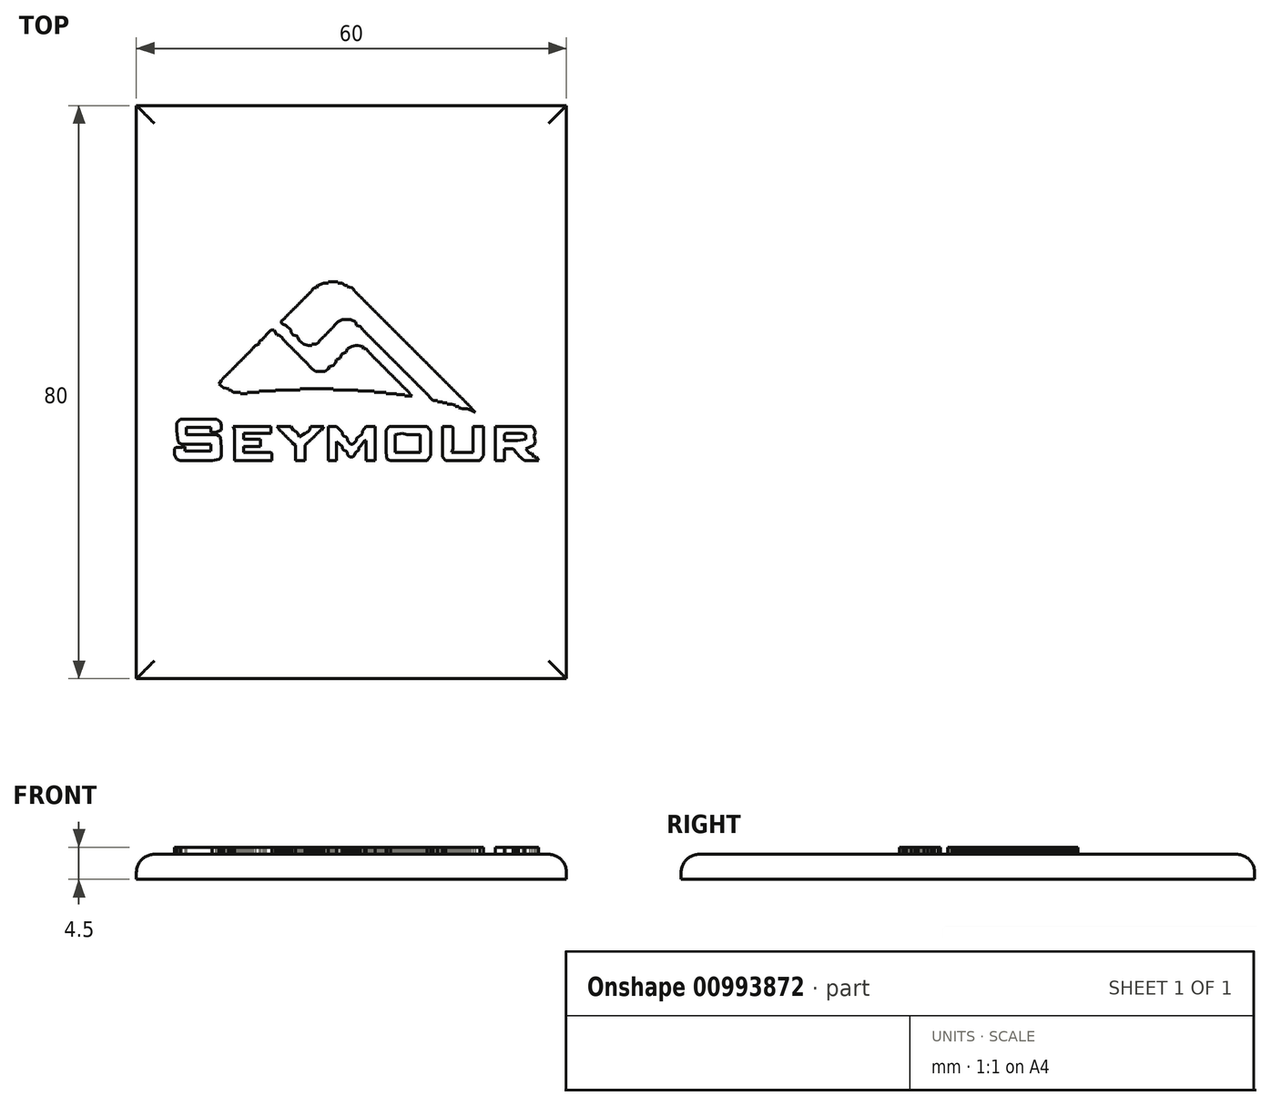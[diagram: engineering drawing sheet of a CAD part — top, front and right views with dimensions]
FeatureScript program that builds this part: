
annotation { "Feature Type Name" : "Feature", "Feature Type Description" : "" }
export const myFeature = defineFeature(function(context is Context, id is Id, definition is map)
    precondition{}
    {
        {
            var Q0;
            Q0=qCreatedBy(makeId("Top.planeOp"),FACE);
            var sketch = newSketch(context, id + "F0", { "sketchPlane" : qUnion([Q0])});
            skLineSegment(sketch, "E0.bottom", {"start": v(-30, 40) * mm, "end": v(30, 40) * mm});
            skLineSegment(sketch, "E0.top", {"start": v(-30, -40) * mm, "end": v(30, -40) * mm});
            skLineSegment(sketch, "E0.left", {"start": v(-30, 40) * mm, "end": v(-30, -40) * mm});
            skLineSegment(sketch, "E0.right", {"start": v(30, 40) * mm, "end": v(30, -40) * mm});
            skLineSegment(sketch, "E1", {"start": v(0, 0) * mm, "end": v(0, 40) * mm});
            skSolve(sketch);
        }
        {
            var Q0;
            Q0 = qSketchRegion(id + "F0", true);
            extrude(context, id + "F1", {"entities" : qUnion([Q0]), "depth" : 3.5 * mm, "offsetDistance" : 25 * mm});
        }
        {
            var Q0;
            Q0=qCreatedBy(makeId("Top.planeOp"),FACE);
            cPlane(context, id + "F2", {"entities" : qUnion([Q0]), "cplaneType" : CPlaneType.OFFSET, "offset" : 3.5 * mm, "width" : 150 * mm, "height" : 150 * mm});
        }
        {
            var Q0;
            Q0=makeQuery(id+"F1.opExtrude","CAP_EDGE",EDGE,{"disambiguationData":[OSD([sQuery(id+"F0.wireOp",EDGE,"E0.left")])],"isStart":false});
            var Q1;
            Q1=makeQuery(id+"F1.opExtrude","CAP_EDGE",EDGE,{"disambiguationData":[OSD([sQuery(id+"F0.wireOp",EDGE,"E0.bottom")])],"isStart":false});
            var Q2;
            Q2=makeQuery(id+"F1.opExtrude","CAP_FACE",FACE,{"disambiguationData":[OSD([sQuery(id+"F0.wireOp",EDGE,"E0.bottom"),sQuery(id+"F0.wireOp",EDGE,"E0.top"),sQuery(id+"F0.wireOp",EDGE,"E0.left"),sQuery(id+"F0.wireOp",EDGE,"E0.right")])],"isStart":false});
            var Q3;
            Q3=makeQuery(id+"F1.opExtrude","CAP_EDGE",EDGE,{"disambiguationData":[OSD([sQuery(id+"F0.wireOp",EDGE,"E0.top")])],"isStart":false});
            fillet(context, id + "F3", {"entities" : qUnion([Q0, Q1, Q2, Q3]), "radius" : 2.5 * mm, "tangentPropagation" : true, "allowEdgeOverflow" : false});
        }
        {
            var Q0;
            Q0=qCreatedBy(id+"F2.planeOp",FACE);
            var sketch = newSketch(context, id + "F4", { "sketchPlane" : qUnion([Q0])});
            skLineSegment(sketch, "E2", {"start": v(-3.22, 15.38) * mm, "end": v(-3.22, 15.21) * mm});
            skLineSegment(sketch, "E3", {"start": v(-3.22, 15.21) * mm, "end": v(-3.87, 15.21) * mm});
            skLineSegment(sketch, "E4", {"start": v(-3.87, 15.21) * mm, "end": v(-4.7, 14.89) * mm});
            skLineSegment(sketch, "E5", {"start": v(-4.7, 14.89) * mm, "end": v(-4.85, 14.56) * mm});
            skLineSegment(sketch, "E6", {"start": v(-4.85, 14.56) * mm, "end": v(-5.18, 14.56) * mm});
            skLineSegment(sketch, "E7", {"start": v(-5.18, 14.56) * mm, "end": v(-5.51, 14.23) * mm});
            skLineSegment(sketch, "E8", {"start": v(-5.51, 14.23) * mm, "end": v(-5.51, 14.07) * mm});
            skLineSegment(sketch, "E9", {"start": v(-5.51, 14.07) * mm, "end": v(-5.67, 14.07) * mm});
            skLineSegment(sketch, "E10", {"start": v(-5.67, 14.07) * mm, "end": v(-5.67, 13.9) * mm});
            skLineSegment(sketch, "E11", {"start": v(-5.67, 13.9) * mm, "end": v(-5.84, 13.9) * mm});
            skLineSegment(sketch, "E12", {"start": v(-5.84, 13.9) * mm, "end": v(-5.84, 13.74) * mm});
            skLineSegment(sketch, "E13", {"start": v(-5.84, 13.74) * mm, "end": v(-6, 13.74) * mm});
            skLineSegment(sketch, "E14", {"start": v(-6, 13.74) * mm, "end": v(-6, 13.57) * mm});
            skLineSegment(sketch, "E15", {"start": v(-6, 13.57) * mm, "end": v(-6.17, 13.57) * mm});
            skLineSegment(sketch, "E16", {"start": v(-6.17, 13.57) * mm, "end": v(-6.17, 13.41) * mm});
            skLineSegment(sketch, "E17", {"start": v(-6.17, 13.41) * mm, "end": v(-6.33, 13.41) * mm});
            skLineSegment(sketch, "E18", {"start": v(-6.33, 13.41) * mm, "end": v(-6.33, 13.25) * mm});
            skLineSegment(sketch, "E19", {"start": v(-6.33, 13.25) * mm, "end": v(-6.5, 13.25) * mm});
            skLineSegment(sketch, "E20", {"start": v(-6.5, 13.25) * mm, "end": v(-6.5, 13.08) * mm});
            skLineSegment(sketch, "E21", {"start": v(-6.5, 13.08) * mm, "end": v(-6.66, 13.08) * mm});
            skLineSegment(sketch, "E22", {"start": v(-6.66, 13.08) * mm, "end": v(-6.66, 12.92) * mm});
            skLineSegment(sketch, "E23", {"start": v(-6.66, 12.92) * mm, "end": v(-6.82, 12.92) * mm});
            skLineSegment(sketch, "E24", {"start": v(-6.82, 12.92) * mm, "end": v(-6.82, 12.76) * mm});
            skLineSegment(sketch, "E25", {"start": v(-6.82, 12.76) * mm, "end": v(-6.99, 12.76) * mm});
            skLineSegment(sketch, "E26", {"start": v(-6.99, 12.76) * mm, "end": v(-6.99, 12.6) * mm});
            skLineSegment(sketch, "E27", {"start": v(-6.99, 12.6) * mm, "end": v(-7.15, 12.6) * mm});
            skLineSegment(sketch, "E28", {"start": v(-7.15, 12.6) * mm, "end": v(-7.15, 12.43) * mm});
            skLineSegment(sketch, "E29", {"start": v(-7.15, 12.43) * mm, "end": v(-7.31, 12.43) * mm});
            skLineSegment(sketch, "E30", {"start": v(-7.31, 12.43) * mm, "end": v(-7.31, 12.26) * mm});
            skLineSegment(sketch, "E31", {"start": v(-7.31, 12.26) * mm, "end": v(-7.48, 12.26) * mm});
            skLineSegment(sketch, "E32", {"start": v(-7.48, 12.26) * mm, "end": v(-7.48, 12.1) * mm});
            skLineSegment(sketch, "E33", {"start": v(-7.48, 12.1) * mm, "end": v(-7.64, 12.1) * mm});
            skLineSegment(sketch, "E34", {"start": v(-7.64, 12.1) * mm, "end": v(-7.64, 11.94) * mm});
            skLineSegment(sketch, "E35", {"start": v(-7.64, 11.94) * mm, "end": v(-7.8, 11.94) * mm});
            skLineSegment(sketch, "E36", {"start": v(-7.8, 11.94) * mm, "end": v(-7.8, 11.77) * mm});
            skLineSegment(sketch, "E37", {"start": v(-7.8, 11.77) * mm, "end": v(-7.97, 11.77) * mm});
            skLineSegment(sketch, "E38", {"start": v(-7.97, 11.77) * mm, "end": v(-7.97, 11.6) * mm});
            skLineSegment(sketch, "E39", {"start": v(-7.97, 11.6) * mm, "end": v(-8.13, 11.6) * mm});
            skLineSegment(sketch, "E40", {"start": v(-8.13, 11.6) * mm, "end": v(-8.13, 11.44) * mm});
            skLineSegment(sketch, "E41", {"start": v(-8.13, 11.44) * mm, "end": v(-8.3, 11.44) * mm});
            skLineSegment(sketch, "E42", {"start": v(-8.3, 11.44) * mm, "end": v(-8.3, 11.28) * mm});
            skLineSegment(sketch, "E43", {"start": v(-8.3, 11.28) * mm, "end": v(-8.46, 11.28) * mm});
            skLineSegment(sketch, "E44", {"start": v(-8.46, 11.28) * mm, "end": v(-8.46, 11.12) * mm});
            skLineSegment(sketch, "E45", {"start": v(-8.46, 11.12) * mm, "end": v(-8.63, 11.12) * mm});
            skLineSegment(sketch, "E46", {"start": v(-8.63, 11.12) * mm, "end": v(-8.63, 10.95) * mm});
            skLineSegment(sketch, "E47", {"start": v(-8.63, 10.95) * mm, "end": v(-8.79, 10.95) * mm});
            skLineSegment(sketch, "E48", {"start": v(-8.79, 10.95) * mm, "end": v(-8.79, 10.79) * mm});
            skLineSegment(sketch, "E49", {"start": v(-8.79, 10.79) * mm, "end": v(-8.95, 10.79) * mm});
            skLineSegment(sketch, "E50", {"start": v(-8.95, 10.79) * mm, "end": v(-8.95, 10.62) * mm});
            skLineSegment(sketch, "E51", {"start": v(-8.95, 10.62) * mm, "end": v(-9.12, 10.62) * mm});
            skLineSegment(sketch, "E52", {"start": v(-9.12, 10.62) * mm, "end": v(-9.12, 10.46) * mm});
            skLineSegment(sketch, "E53", {"start": v(-9.12, 10.46) * mm, "end": v(-9.28, 10.46) * mm});
            skLineSegment(sketch, "E54", {"start": v(-9.28, 10.46) * mm, "end": v(-9.28, 10.3) * mm});
            skLineSegment(sketch, "E55", {"start": v(-9.28, 10.3) * mm, "end": v(-9.77, 9.97) * mm});
            skLineSegment(sketch, "E56", {"start": v(-9.77, 9.97) * mm, "end": v(-9.77, 9.64) * mm});
            skLineSegment(sketch, "E57", {"start": v(-9.77, 9.64) * mm, "end": v(-9.6, 9.48) * mm});
            skLineSegment(sketch, "E58", {"start": v(-9.6, 9.48) * mm, "end": v(-9.12, 9.31) * mm});
            skLineSegment(sketch, "E59", {"start": v(-9.12, 9.31) * mm, "end": v(-8.63, 8.82) * mm});
            skLineSegment(sketch, "E60", {"start": v(-8.63, 8.82) * mm, "end": v(-8.46, 8.66) * mm});
            skLineSegment(sketch, "E61", {"start": v(-8.46, 8.66) * mm, "end": v(-8.46, 8.33) * mm});
            skLineSegment(sketch, "E62", {"start": v(-8.46, 8.33) * mm, "end": v(-8.13, 8) * mm});
            skLineSegment(sketch, "E63", {"start": v(-8.13, 8) * mm, "end": v(-7.64, 7.84) * mm});
            skLineSegment(sketch, "E64", {"start": v(-7.64, 7.84) * mm, "end": v(-7.48, 7.67) * mm});
            skLineSegment(sketch, "E65", {"start": v(-7.48, 7.67) * mm, "end": v(-7.31, 7.18) * mm});
            skLineSegment(sketch, "E66", {"start": v(-7.31, 7.18) * mm, "end": v(-6.66, 6.69) * mm});
            skLineSegment(sketch, "E67", {"start": v(-6.66, 6.69) * mm, "end": v(-6, 6.53) * mm});
            skLineSegment(sketch, "E68", {"start": v(-6, 6.53) * mm, "end": v(-5.51, 6.53) * mm});
            skLineSegment(sketch, "E69", {"start": v(-5.51, 6.53) * mm, "end": v(-5.51, 6.69) * mm});
            skLineSegment(sketch, "E70", {"start": v(-5.51, 6.69) * mm, "end": v(-4.85, 6.69) * mm});
            skLineSegment(sketch, "E71", {"start": v(-4.85, 6.69) * mm, "end": v(-4.53, 7.02) * mm});
            skLineSegment(sketch, "E72", {"start": v(-4.53, 7.02) * mm, "end": v(-4.53, 7.18) * mm});
            skLineSegment(sketch, "E73", {"start": v(-4.53, 7.18) * mm, "end": v(-4.36, 7.18) * mm});
            skLineSegment(sketch, "E74", {"start": v(-4.36, 7.18) * mm, "end": v(-4.36, 7.35) * mm});
            skLineSegment(sketch, "E75", {"start": v(-4.36, 7.35) * mm, "end": v(-4.2, 7.35) * mm});
            skLineSegment(sketch, "E76", {"start": v(-4.2, 7.35) * mm, "end": v(-4.2, 7.5) * mm});
            skLineSegment(sketch, "E77", {"start": v(-4.2, 7.5) * mm, "end": v(-4.04, 7.5) * mm});
            skLineSegment(sketch, "E78", {"start": v(-4.04, 7.5) * mm, "end": v(-4.04, 7.67) * mm});
            skLineSegment(sketch, "E79", {"start": v(-4.04, 7.67) * mm, "end": v(-3.87, 7.67) * mm});
            skLineSegment(sketch, "E80", {"start": v(-3.87, 7.67) * mm, "end": v(-3.87, 7.84) * mm});
            skLineSegment(sketch, "E81", {"start": v(-3.87, 7.84) * mm, "end": v(-3.7, 7.84) * mm});
            skLineSegment(sketch, "E82", {"start": v(-3.7, 7.84) * mm, "end": v(-3.7, 8) * mm});
            skLineSegment(sketch, "E83", {"start": v(-3.7, 8) * mm, "end": v(-3.54, 8) * mm});
            skLineSegment(sketch, "E84", {"start": v(-3.54, 8) * mm, "end": v(-3.54, 8.16) * mm});
            skLineSegment(sketch, "E85", {"start": v(-3.54, 8.16) * mm, "end": v(-3.38, 8.16) * mm});
            skLineSegment(sketch, "E86", {"start": v(-3.38, 8.16) * mm, "end": v(-3.38, 8.33) * mm});
            skLineSegment(sketch, "E87", {"start": v(-3.38, 8.33) * mm, "end": v(-3.22, 8.33) * mm});
            skLineSegment(sketch, "E88", {"start": v(-3.22, 8.33) * mm, "end": v(-3.22, 8.5) * mm});
            skLineSegment(sketch, "E89", {"start": v(-3.22, 8.5) * mm, "end": v(-3.05, 8.5) * mm});
            skLineSegment(sketch, "E90", {"start": v(-3.05, 8.5) * mm, "end": v(-3.05, 8.66) * mm});
            skLineSegment(sketch, "E91", {"start": v(-3.05, 8.66) * mm, "end": v(-2.89, 8.66) * mm});
            skLineSegment(sketch, "E92", {"start": v(-2.89, 8.66) * mm, "end": v(-2.89, 8.82) * mm});
            skLineSegment(sketch, "E93", {"start": v(-2.89, 8.82) * mm, "end": v(-2.72, 8.82) * mm});
            skLineSegment(sketch, "E94", {"start": v(-2.72, 8.82) * mm, "end": v(-2.72, 8.98) * mm});
            skLineSegment(sketch, "E95", {"start": v(-2.72, 8.98) * mm, "end": v(-2.56, 8.98) * mm});
            skLineSegment(sketch, "E96", {"start": v(-2.56, 8.98) * mm, "end": v(-2.56, 9.15) * mm});
            skLineSegment(sketch, "E97", {"start": v(-2.56, 9.15) * mm, "end": v(-2.4, 9.15) * mm});
            skLineSegment(sketch, "E98", {"start": v(-2.4, 9.15) * mm, "end": v(-2.4, 9.31) * mm});
            skLineSegment(sketch, "E99", {"start": v(-2.4, 9.31) * mm, "end": v(-1.9, 9.8) * mm});
            skLineSegment(sketch, "E100", {"start": v(-1.9, 9.8) * mm, "end": v(-1.25, 10.13) * mm});
            skLineSegment(sketch, "E101", {"start": v(-1.25, 10.13) * mm, "end": v(-0.1, 10.13) * mm});
            skLineSegment(sketch, "E102", {"start": v(-0.1, 10.13) * mm, "end": v(0.55, 9.8) * mm});
            skLineSegment(sketch, "E103", {"start": v(0.55, 9.8) * mm, "end": v(0.72, 9.31) * mm});
            skLineSegment(sketch, "E104", {"start": v(0.72, 9.31) * mm, "end": v(1.21, 9.15) * mm});
            skLineSegment(sketch, "E105", {"start": v(1.21, 9.15) * mm, "end": v(1.54, 8.82) * mm});
            skLineSegment(sketch, "E106", {"start": v(1.54, 8.82) * mm, "end": v(1.54, 8.66) * mm});
            skLineSegment(sketch, "E107", {"start": v(1.54, 8.66) * mm, "end": v(1.7, 8.66) * mm});
            skLineSegment(sketch, "E108", {"start": v(1.7, 8.66) * mm, "end": v(1.7, 8.5) * mm});
            skLineSegment(sketch, "E109", {"start": v(1.7, 8.5) * mm, "end": v(1.87, 8.5) * mm});
            skLineSegment(sketch, "E110", {"start": v(1.87, 8.5) * mm, "end": v(1.87, 8.33) * mm});
            skLineSegment(sketch, "E111", {"start": v(1.87, 8.33) * mm, "end": v(2.03, 8.33) * mm});
            skLineSegment(sketch, "E112", {"start": v(2.03, 8.33) * mm, "end": v(2.03, 8.16) * mm});
            skLineSegment(sketch, "E113", {"start": v(2.03, 8.16) * mm, "end": v(2.2, 8.16) * mm});
            skLineSegment(sketch, "E114", {"start": v(2.2, 8.16) * mm, "end": v(2.2, 8) * mm});
            skLineSegment(sketch, "E115", {"start": v(2.2, 8) * mm, "end": v(2.36, 8) * mm});
            skLineSegment(sketch, "E116", {"start": v(2.36, 8) * mm, "end": v(2.36, 7.84) * mm});
            skLineSegment(sketch, "E117", {"start": v(2.36, 7.84) * mm, "end": v(2.52, 7.84) * mm});
            skLineSegment(sketch, "E118", {"start": v(2.52, 7.84) * mm, "end": v(2.52, 7.67) * mm});
            skLineSegment(sketch, "E119", {"start": v(2.52, 7.67) * mm, "end": v(2.69, 7.67) * mm});
            skLineSegment(sketch, "E120", {"start": v(2.69, 7.67) * mm, "end": v(2.69, 7.5) * mm});
            skLineSegment(sketch, "E121", {"start": v(2.69, 7.5) * mm, "end": v(2.85, 7.5) * mm});
            skLineSegment(sketch, "E122", {"start": v(2.85, 7.5) * mm, "end": v(2.85, 7.35) * mm});
            skLineSegment(sketch, "E123", {"start": v(2.85, 7.35) * mm, "end": v(3.01, 7.35) * mm});
            skLineSegment(sketch, "E124", {"start": v(3.01, 7.35) * mm, "end": v(3.01, 7.18) * mm});
            skLineSegment(sketch, "E125", {"start": v(3.01, 7.18) * mm, "end": v(3.18, 7.18) * mm});
            skLineSegment(sketch, "E126", {"start": v(3.18, 7.18) * mm, "end": v(3.18, 7.02) * mm});
            skLineSegment(sketch, "E127", {"start": v(3.18, 7.02) * mm, "end": v(3.34, 7.02) * mm});
            skLineSegment(sketch, "E128", {"start": v(3.34, 7.02) * mm, "end": v(3.34, 6.85) * mm});
            skLineSegment(sketch, "E129", {"start": v(3.34, 6.85) * mm, "end": v(3.5, 6.85) * mm});
            skLineSegment(sketch, "E130", {"start": v(3.5, 6.85) * mm, "end": v(3.5, 6.69) * mm});
            skLineSegment(sketch, "E131", {"start": v(3.5, 6.69) * mm, "end": v(3.67, 6.69) * mm});
            skLineSegment(sketch, "E132", {"start": v(3.67, 6.69) * mm, "end": v(3.67, 6.53) * mm});
            skLineSegment(sketch, "E133", {"start": v(3.67, 6.53) * mm, "end": v(3.83, 6.53) * mm});
            skLineSegment(sketch, "E134", {"start": v(3.83, 6.53) * mm, "end": v(3.83, 6.36) * mm});
            skLineSegment(sketch, "E135", {"start": v(3.83, 6.36) * mm, "end": v(4, 6.36) * mm});
            skLineSegment(sketch, "E136", {"start": v(4, 6.36) * mm, "end": v(4, 6.2) * mm});
            skLineSegment(sketch, "E137", {"start": v(4, 6.2) * mm, "end": v(4.16, 6.2) * mm});
            skLineSegment(sketch, "E138", {"start": v(4.16, 6.2) * mm, "end": v(4.16, 6.03) * mm});
            skLineSegment(sketch, "E139", {"start": v(4.16, 6.03) * mm, "end": v(4.33, 6.03) * mm});
            skLineSegment(sketch, "E140", {"start": v(4.33, 6.03) * mm, "end": v(4.33, 5.87) * mm});
            skLineSegment(sketch, "E141", {"start": v(4.33, 5.87) * mm, "end": v(4.49, 5.87) * mm});
            skLineSegment(sketch, "E142", {"start": v(4.49, 5.87) * mm, "end": v(4.49, 5.7) * mm});
            skLineSegment(sketch, "E143", {"start": v(4.49, 5.7) * mm, "end": v(4.65, 5.7) * mm});
            skLineSegment(sketch, "E144", {"start": v(4.65, 5.7) * mm, "end": v(4.65, 5.54) * mm});
            skLineSegment(sketch, "E145", {"start": v(4.65, 5.54) * mm, "end": v(4.82, 5.54) * mm});
            skLineSegment(sketch, "E146", {"start": v(4.82, 5.54) * mm, "end": v(4.82, 5.38) * mm});
            skLineSegment(sketch, "E147", {"start": v(4.82, 5.38) * mm, "end": v(4.98, 5.38) * mm});
            skLineSegment(sketch, "E148", {"start": v(4.98, 5.38) * mm, "end": v(4.98, 5.21) * mm});
            skLineSegment(sketch, "E149", {"start": v(4.98, 5.21) * mm, "end": v(5.15, 5.21) * mm});
            skLineSegment(sketch, "E150", {"start": v(5.15, 5.21) * mm, "end": v(5.15, 5.05) * mm});
            skLineSegment(sketch, "E151", {"start": v(5.15, 5.05) * mm, "end": v(5.3, 5.05) * mm});
            skLineSegment(sketch, "E152", {"start": v(5.3, 5.05) * mm, "end": v(5.3, 4.89) * mm});
            skLineSegment(sketch, "E153", {"start": v(5.3, 4.89) * mm, "end": v(5.47, 4.89) * mm});
            skLineSegment(sketch, "E154", {"start": v(5.47, 4.89) * mm, "end": v(5.47, 4.72) * mm});
            skLineSegment(sketch, "E155", {"start": v(5.47, 4.72) * mm, "end": v(5.64, 4.72) * mm});
            skLineSegment(sketch, "E156", {"start": v(5.64, 4.72) * mm, "end": v(5.64, 4.56) * mm});
            skLineSegment(sketch, "E157", {"start": v(5.64, 4.56) * mm, "end": v(5.8, 4.56) * mm});
            skLineSegment(sketch, "E158", {"start": v(5.8, 4.56) * mm, "end": v(5.8, 4.4) * mm});
            skLineSegment(sketch, "E159", {"start": v(5.8, 4.4) * mm, "end": v(5.96, 4.4) * mm});
            skLineSegment(sketch, "E160", {"start": v(5.96, 4.4) * mm, "end": v(5.96, 4.23) * mm});
            skLineSegment(sketch, "E161", {"start": v(5.96, 4.23) * mm, "end": v(6.13, 4.23) * mm});
            skLineSegment(sketch, "E162", {"start": v(6.13, 4.23) * mm, "end": v(6.13, 4.07) * mm});
            skLineSegment(sketch, "E163", {"start": v(6.13, 4.07) * mm, "end": v(6.3, 4.07) * mm});
            skLineSegment(sketch, "E164", {"start": v(6.3, 4.07) * mm, "end": v(6.3, 3.9) * mm});
            skLineSegment(sketch, "E165", {"start": v(6.3, 3.9) * mm, "end": v(6.46, 3.9) * mm});
            skLineSegment(sketch, "E166", {"start": v(6.46, 3.9) * mm, "end": v(6.46, 3.74) * mm});
            skLineSegment(sketch, "E167", {"start": v(6.46, 3.74) * mm, "end": v(6.62, 3.74) * mm});
            skLineSegment(sketch, "E168", {"start": v(6.62, 3.74) * mm, "end": v(6.62, 3.57) * mm});
            skLineSegment(sketch, "E169", {"start": v(6.62, 3.57) * mm, "end": v(6.78, 3.57) * mm});
            skLineSegment(sketch, "E170", {"start": v(6.78, 3.57) * mm, "end": v(6.78, 3.41) * mm});
            skLineSegment(sketch, "E171", {"start": v(6.78, 3.41) * mm, "end": v(6.95, 3.41) * mm});
            skLineSegment(sketch, "E172", {"start": v(6.95, 3.41) * mm, "end": v(6.95, 3.25) * mm});
            skLineSegment(sketch, "E173", {"start": v(6.95, 3.25) * mm, "end": v(7.11, 3.25) * mm});
            skLineSegment(sketch, "E174", {"start": v(7.11, 3.25) * mm, "end": v(7.11, 3.08) * mm});
            skLineSegment(sketch, "E175", {"start": v(7.11, 3.08) * mm, "end": v(7.28, 3.08) * mm});
            skLineSegment(sketch, "E176", {"start": v(7.28, 3.08) * mm, "end": v(7.28, 2.92) * mm});
            skLineSegment(sketch, "E177", {"start": v(7.28, 2.92) * mm, "end": v(7.44, 2.92) * mm});
            skLineSegment(sketch, "E178", {"start": v(7.44, 2.92) * mm, "end": v(7.44, 2.76) * mm});
            skLineSegment(sketch, "E179", {"start": v(7.44, 2.76) * mm, "end": v(7.6, 2.76) * mm});
            skLineSegment(sketch, "E180", {"start": v(7.6, 2.76) * mm, "end": v(7.6, 2.6) * mm});
            skLineSegment(sketch, "E181", {"start": v(7.6, 2.6) * mm, "end": v(7.77, 2.6) * mm});
            skLineSegment(sketch, "E182", {"start": v(7.77, 2.6) * mm, "end": v(7.77, 2.43) * mm});
            skLineSegment(sketch, "E183", {"start": v(7.77, 2.43) * mm, "end": v(7.93, 2.43) * mm});
            skLineSegment(sketch, "E184", {"start": v(7.93, 2.43) * mm, "end": v(7.93, 2.26) * mm});
            skLineSegment(sketch, "E185", {"start": v(7.93, 2.26) * mm, "end": v(8.1, 2.26) * mm});
            skLineSegment(sketch, "E186", {"start": v(8.1, 2.26) * mm, "end": v(8.1, 2.1) * mm});
            skLineSegment(sketch, "E187", {"start": v(8.1, 2.1) * mm, "end": v(8.26, 2.1) * mm});
            skLineSegment(sketch, "E188", {"start": v(8.26, 2.1) * mm, "end": v(8.26, 1.94) * mm});
            skLineSegment(sketch, "E189", {"start": v(8.26, 1.94) * mm, "end": v(8.42, 1.94) * mm});
            skLineSegment(sketch, "E190", {"start": v(8.42, 1.94) * mm, "end": v(8.42, 1.77) * mm});
            skLineSegment(sketch, "E191", {"start": v(8.42, 1.77) * mm, "end": v(8.59, 1.77) * mm});
            skLineSegment(sketch, "E192", {"start": v(8.59, 1.77) * mm, "end": v(8.59, 1.6) * mm});
            skLineSegment(sketch, "E193", {"start": v(8.59, 1.6) * mm, "end": v(8.75, 1.6) * mm});
            skLineSegment(sketch, "E194", {"start": v(8.75, 1.6) * mm, "end": v(8.75, 1.44) * mm});
            skLineSegment(sketch, "E195", {"start": v(8.75, 1.44) * mm, "end": v(8.92, 1.44) * mm});
            skLineSegment(sketch, "E196", {"start": v(8.92, 1.44) * mm, "end": v(8.92, 1.28) * mm});
            skLineSegment(sketch, "E197", {"start": v(8.92, 1.28) * mm, "end": v(9.08, 1.28) * mm});
            skLineSegment(sketch, "E198", {"start": v(9.08, 1.28) * mm, "end": v(9.08, 1.12) * mm});
            skLineSegment(sketch, "E199", {"start": v(9.08, 1.12) * mm, "end": v(9.24, 1.12) * mm});
            skLineSegment(sketch, "E200", {"start": v(9.24, 1.12) * mm, "end": v(9.24, 0.95) * mm});
            skLineSegment(sketch, "E201", {"start": v(9.24, 0.95) * mm, "end": v(9.4, 0.95) * mm});
            skLineSegment(sketch, "E202", {"start": v(9.4, 0.95) * mm, "end": v(9.4, 0.79) * mm});
            skLineSegment(sketch, "E203", {"start": v(9.4, 0.79) * mm, "end": v(9.57, 0.79) * mm});
            skLineSegment(sketch, "E204", {"start": v(9.57, 0.79) * mm, "end": v(9.57, 0.62) * mm});
            skLineSegment(sketch, "E205", {"start": v(9.57, 0.62) * mm, "end": v(9.74, 0.62) * mm});
            skLineSegment(sketch, "E206", {"start": v(9.74, 0.62) * mm, "end": v(9.74, 0.46) * mm});
            skLineSegment(sketch, "E207", {"start": v(9.74, 0.46) * mm, "end": v(9.9, 0.46) * mm});
            skLineSegment(sketch, "E208", {"start": v(9.9, 0.46) * mm, "end": v(9.9, 0.3) * mm});
            skLineSegment(sketch, "E209", {"start": v(9.9, 0.3) * mm, "end": v(10.06, 0.3) * mm});
            skLineSegment(sketch, "E210", {"start": v(10.06, 0.3) * mm, "end": v(10.06, 0.13) * mm});
            skLineSegment(sketch, "E211", {"start": v(10.06, 0.13) * mm, "end": v(10.23, 0.13) * mm});
            skLineSegment(sketch, "E212", {"start": v(10.23, 0.13) * mm, "end": v(10.23, -0.03) * mm});
            skLineSegment(sketch, "E213", {"start": v(10.23, -0.03) * mm, "end": v(10.4, -0.03) * mm});
            skLineSegment(sketch, "E214", {"start": v(10.4, -0.03) * mm, "end": v(10.4, -0.2) * mm});
            skLineSegment(sketch, "E215", {"start": v(10.4, -0.2) * mm, "end": v(10.55, -0.2) * mm});
            skLineSegment(sketch, "E216", {"start": v(10.55, -0.2) * mm, "end": v(10.55, -0.36) * mm});
            skLineSegment(sketch, "E217", {"start": v(10.55, -0.36) * mm, "end": v(10.72, -0.36) * mm});
            skLineSegment(sketch, "E218", {"start": v(10.72, -0.36) * mm, "end": v(10.72, -0.52) * mm});
            skLineSegment(sketch, "E219", {"start": v(10.72, -0.52) * mm, "end": v(10.88, -0.52) * mm});
            skLineSegment(sketch, "E220", {"start": v(10.88, -0.52) * mm, "end": v(10.88, -0.69) * mm});
            skLineSegment(sketch, "E221", {"start": v(10.88, -0.69) * mm, "end": v(11.37, -1.18) * mm});
            skLineSegment(sketch, "E222", {"start": v(11.37, -1.18) * mm, "end": v(12.03, -1.18) * mm});
            skLineSegment(sketch, "E223", {"start": v(12.03, -1.18) * mm, "end": v(12.03, -1.34) * mm});
            skLineSegment(sketch, "E224", {"start": v(12.03, -1.34) * mm, "end": v(12.69, -1.34) * mm});
            skLineSegment(sketch, "E225", {"start": v(12.69, -1.34) * mm, "end": v(12.69, -1.5) * mm});
            skLineSegment(sketch, "E226", {"start": v(12.69, -1.5) * mm, "end": v(13.34, -1.5) * mm});
            skLineSegment(sketch, "E227", {"start": v(13.34, -1.5) * mm, "end": v(13.34, -1.67) * mm});
            skLineSegment(sketch, "E228", {"start": v(13.34, -1.67) * mm, "end": v(14, -1.67) * mm});
            skLineSegment(sketch, "E229", {"start": v(14, -1.67) * mm, "end": v(14.49, -1.84) * mm});
            skLineSegment(sketch, "E230", {"start": v(14.49, -1.84) * mm, "end": v(14.49, -2) * mm});
            skLineSegment(sketch, "E231", {"start": v(14.49, -2) * mm, "end": v(14.98, -2) * mm});
            skLineSegment(sketch, "E232", {"start": v(14.98, -2) * mm, "end": v(14.98, -2.16) * mm});
            skLineSegment(sketch, "E233", {"start": v(14.98, -2.16) * mm, "end": v(15.47, -2.33) * mm});
            skLineSegment(sketch, "E234", {"start": v(15.47, -2.33) * mm, "end": v(16.13, -2.33) * mm});
            skLineSegment(sketch, "E235", {"start": v(16.13, -2.33) * mm, "end": v(16.62, -2.5) * mm});
            skLineSegment(sketch, "E236", {"start": v(16.62, -2.5) * mm, "end": v(17.28, -2.82) * mm});
            skLineSegment(sketch, "E237", {"start": v(17.28, -2.82) * mm, "end": v(16.95, -2.5) * mm});
            skLineSegment(sketch, "E238", {"start": v(16.95, -2.5) * mm, "end": v(16.78, -2.33) * mm});
            skLineSegment(sketch, "E239", {"start": v(16.78, -2.33) * mm, "end": v(16.62, -2.16) * mm});
            skLineSegment(sketch, "E240", {"start": v(16.62, -2.16) * mm, "end": v(16.62, -2) * mm});
            skLineSegment(sketch, "E241", {"start": v(16.62, -2) * mm, "end": v(16.46, -2) * mm});
            skLineSegment(sketch, "E242", {"start": v(16.46, -2) * mm, "end": v(16.46, -1.84) * mm});
            skLineSegment(sketch, "E243", {"start": v(16.46, -1.84) * mm, "end": v(16.3, -1.84) * mm});
            skLineSegment(sketch, "E244", {"start": v(16.3, -1.84) * mm, "end": v(16.3, -1.67) * mm});
            skLineSegment(sketch, "E245", {"start": v(16.3, -1.67) * mm, "end": v(16.13, -1.67) * mm});
            skLineSegment(sketch, "E246", {"start": v(16.13, -1.67) * mm, "end": v(16.13, -1.5) * mm});
            skLineSegment(sketch, "E247", {"start": v(16.13, -1.5) * mm, "end": v(15.96, -1.5) * mm});
            skLineSegment(sketch, "E248", {"start": v(15.96, -1.5) * mm, "end": v(15.96, -1.34) * mm});
            skLineSegment(sketch, "E249", {"start": v(15.96, -1.34) * mm, "end": v(15.8, -1.34) * mm});
            skLineSegment(sketch, "E250", {"start": v(15.8, -1.34) * mm, "end": v(15.8, -1.18) * mm});
            skLineSegment(sketch, "E251", {"start": v(15.8, -1.18) * mm, "end": v(15.64, -1.18) * mm});
            skLineSegment(sketch, "E252", {"start": v(15.64, -1.18) * mm, "end": v(15.64, -1.02) * mm});
            skLineSegment(sketch, "E253", {"start": v(15.64, -1.02) * mm, "end": v(15.47, -1.02) * mm});
            skLineSegment(sketch, "E254", {"start": v(15.47, -1.02) * mm, "end": v(15.47, -0.85) * mm});
            skLineSegment(sketch, "E255", {"start": v(15.47, -0.85) * mm, "end": v(15.3, -0.85) * mm});
            skLineSegment(sketch, "E256", {"start": v(15.3, -0.85) * mm, "end": v(15.3, -0.69) * mm});
            skLineSegment(sketch, "E257", {"start": v(15.3, -0.69) * mm, "end": v(15.15, -0.69) * mm});
            skLineSegment(sketch, "E258", {"start": v(15.15, -0.69) * mm, "end": v(15.15, -0.52) * mm});
            skLineSegment(sketch, "E259", {"start": v(15.15, -0.52) * mm, "end": v(14.98, -0.52) * mm});
            skLineSegment(sketch, "E260", {"start": v(14.98, -0.52) * mm, "end": v(14.98, -0.36) * mm});
            skLineSegment(sketch, "E261", {"start": v(14.98, -0.36) * mm, "end": v(14.82, -0.36) * mm});
            skLineSegment(sketch, "E262", {"start": v(14.82, -0.36) * mm, "end": v(14.82, -0.2) * mm});
            skLineSegment(sketch, "E263", {"start": v(14.82, -0.2) * mm, "end": v(14.65, -0.2) * mm});
            skLineSegment(sketch, "E264", {"start": v(14.65, -0.2) * mm, "end": v(14.65, -0.03) * mm});
            skLineSegment(sketch, "E265", {"start": v(14.65, -0.03) * mm, "end": v(14.49, -0.03) * mm});
            skLineSegment(sketch, "E266", {"start": v(14.49, -0.03) * mm, "end": v(14.49, 0.13) * mm});
            skLineSegment(sketch, "E267", {"start": v(14.49, 0.13) * mm, "end": v(14.33, 0.13) * mm});
            skLineSegment(sketch, "E268", {"start": v(14.33, 0.13) * mm, "end": v(14.33, 0.3) * mm});
            skLineSegment(sketch, "E269", {"start": v(14.33, 0.3) * mm, "end": v(14.16, 0.3) * mm});
            skLineSegment(sketch, "E270", {"start": v(14.16, 0.3) * mm, "end": v(14.16, 0.46) * mm});
            skLineSegment(sketch, "E271", {"start": v(14.16, 0.46) * mm, "end": v(14, 0.46) * mm});
            skLineSegment(sketch, "E272", {"start": v(14, 0.46) * mm, "end": v(14, 0.62) * mm});
            skLineSegment(sketch, "E273", {"start": v(14, 0.62) * mm, "end": v(13.83, 0.62) * mm});
            skLineSegment(sketch, "E274", {"start": v(13.83, 0.62) * mm, "end": v(13.83, 0.79) * mm});
            skLineSegment(sketch, "E275", {"start": v(13.83, 0.79) * mm, "end": v(13.67, 0.79) * mm});
            skLineSegment(sketch, "E276", {"start": v(13.67, 0.79) * mm, "end": v(13.67, 0.95) * mm});
            skLineSegment(sketch, "E277", {"start": v(13.67, 0.95) * mm, "end": v(13.5, 0.95) * mm});
            skLineSegment(sketch, "E278", {"start": v(13.5, 0.95) * mm, "end": v(13.5, 1.12) * mm});
            skLineSegment(sketch, "E279", {"start": v(13.5, 1.12) * mm, "end": v(13.34, 1.12) * mm});
            skLineSegment(sketch, "E280", {"start": v(13.34, 1.12) * mm, "end": v(13.34, 1.28) * mm});
            skLineSegment(sketch, "E281", {"start": v(13.34, 1.28) * mm, "end": v(13.18, 1.28) * mm});
            skLineSegment(sketch, "E282", {"start": v(13.18, 1.28) * mm, "end": v(13.18, 1.44) * mm});
            skLineSegment(sketch, "E283", {"start": v(13.18, 1.44) * mm, "end": v(13.01, 1.44) * mm});
            skLineSegment(sketch, "E284", {"start": v(13.01, 1.44) * mm, "end": v(13.01, 1.6) * mm});
            skLineSegment(sketch, "E285", {"start": v(13.01, 1.6) * mm, "end": v(12.85, 1.6) * mm});
            skLineSegment(sketch, "E286", {"start": v(12.85, 1.6) * mm, "end": v(12.85, 1.77) * mm});
            skLineSegment(sketch, "E287", {"start": v(12.85, 1.77) * mm, "end": v(12.69, 1.77) * mm});
            skLineSegment(sketch, "E288", {"start": v(12.69, 1.77) * mm, "end": v(12.69, 1.94) * mm});
            skLineSegment(sketch, "E289", {"start": v(12.69, 1.94) * mm, "end": v(12.52, 1.94) * mm});
            skLineSegment(sketch, "E290", {"start": v(12.52, 1.94) * mm, "end": v(12.52, 2.1) * mm});
            skLineSegment(sketch, "E291", {"start": v(12.52, 2.1) * mm, "end": v(12.36, 2.1) * mm});
            skLineSegment(sketch, "E292", {"start": v(12.36, 2.1) * mm, "end": v(12.36, 2.26) * mm});
            skLineSegment(sketch, "E293", {"start": v(12.36, 2.26) * mm, "end": v(12.2, 2.26) * mm});
            skLineSegment(sketch, "E294", {"start": v(12.2, 2.26) * mm, "end": v(12.2, 2.43) * mm});
            skLineSegment(sketch, "E295", {"start": v(12.2, 2.43) * mm, "end": v(12.03, 2.43) * mm});
            skLineSegment(sketch, "E296", {"start": v(12.03, 2.43) * mm, "end": v(12.03, 2.6) * mm});
            skLineSegment(sketch, "E297", {"start": v(12.03, 2.6) * mm, "end": v(11.87, 2.6) * mm});
            skLineSegment(sketch, "E298", {"start": v(11.87, 2.6) * mm, "end": v(11.87, 2.76) * mm});
            skLineSegment(sketch, "E299", {"start": v(11.87, 2.76) * mm, "end": v(11.7, 2.76) * mm});
            skLineSegment(sketch, "E300", {"start": v(11.7, 2.76) * mm, "end": v(11.7, 2.92) * mm});
            skLineSegment(sketch, "E301", {"start": v(11.7, 2.92) * mm, "end": v(11.54, 2.92) * mm});
            skLineSegment(sketch, "E302", {"start": v(11.54, 2.92) * mm, "end": v(11.54, 3.08) * mm});
            skLineSegment(sketch, "E303", {"start": v(11.54, 3.08) * mm, "end": v(11.37, 3.08) * mm});
            skLineSegment(sketch, "E304", {"start": v(11.37, 3.08) * mm, "end": v(11.37, 3.25) * mm});
            skLineSegment(sketch, "E305", {"start": v(11.37, 3.25) * mm, "end": v(11.21, 3.25) * mm});
            skLineSegment(sketch, "E306", {"start": v(11.21, 3.25) * mm, "end": v(11.21, 3.41) * mm});
            skLineSegment(sketch, "E307", {"start": v(11.21, 3.41) * mm, "end": v(11.05, 3.41) * mm});
            skLineSegment(sketch, "E308", {"start": v(11.05, 3.41) * mm, "end": v(11.05, 3.57) * mm});
            skLineSegment(sketch, "E309", {"start": v(11.05, 3.57) * mm, "end": v(10.88, 3.57) * mm});
            skLineSegment(sketch, "E310", {"start": v(10.88, 3.57) * mm, "end": v(10.88, 3.74) * mm});
            skLineSegment(sketch, "E311", {"start": v(10.88, 3.74) * mm, "end": v(10.72, 3.74) * mm});
            skLineSegment(sketch, "E312", {"start": v(10.72, 3.74) * mm, "end": v(10.72, 3.9) * mm});
            skLineSegment(sketch, "E313", {"start": v(10.72, 3.9) * mm, "end": v(10.55, 3.9) * mm});
            skLineSegment(sketch, "E314", {"start": v(10.55, 3.9) * mm, "end": v(10.55, 4.07) * mm});
            skLineSegment(sketch, "E315", {"start": v(10.55, 4.07) * mm, "end": v(10.4, 4.07) * mm});
            skLineSegment(sketch, "E316", {"start": v(10.4, 4.07) * mm, "end": v(10.4, 4.23) * mm});
            skLineSegment(sketch, "E317", {"start": v(10.4, 4.23) * mm, "end": v(10.23, 4.23) * mm});
            skLineSegment(sketch, "E318", {"start": v(10.23, 4.23) * mm, "end": v(10.23, 4.4) * mm});
            skLineSegment(sketch, "E319", {"start": v(10.23, 4.4) * mm, "end": v(10.06, 4.4) * mm});
            skLineSegment(sketch, "E320", {"start": v(10.06, 4.4) * mm, "end": v(10.06, 4.56) * mm});
            skLineSegment(sketch, "E321", {"start": v(10.06, 4.56) * mm, "end": v(9.9, 4.56) * mm});
            skLineSegment(sketch, "E322", {"start": v(9.9, 4.56) * mm, "end": v(9.9, 4.72) * mm});
            skLineSegment(sketch, "E323", {"start": v(9.9, 4.72) * mm, "end": v(9.74, 4.72) * mm});
            skLineSegment(sketch, "E324", {"start": v(9.74, 4.72) * mm, "end": v(9.74, 4.89) * mm});
            skLineSegment(sketch, "E325", {"start": v(9.74, 4.89) * mm, "end": v(9.57, 4.89) * mm});
            skLineSegment(sketch, "E326", {"start": v(9.57, 4.89) * mm, "end": v(9.57, 5.05) * mm});
            skLineSegment(sketch, "E327", {"start": v(9.57, 5.05) * mm, "end": v(9.4, 5.05) * mm});
            skLineSegment(sketch, "E328", {"start": v(9.4, 5.05) * mm, "end": v(9.4, 5.21) * mm});
            skLineSegment(sketch, "E329", {"start": v(9.4, 5.21) * mm, "end": v(9.24, 5.21) * mm});
            skLineSegment(sketch, "E330", {"start": v(9.24, 5.21) * mm, "end": v(9.24, 5.38) * mm});
            skLineSegment(sketch, "E331", {"start": v(9.24, 5.38) * mm, "end": v(9.08, 5.38) * mm});
            skLineSegment(sketch, "E332", {"start": v(9.08, 5.38) * mm, "end": v(9.08, 5.54) * mm});
            skLineSegment(sketch, "E333", {"start": v(9.08, 5.54) * mm, "end": v(8.92, 5.54) * mm});
            skLineSegment(sketch, "E334", {"start": v(8.92, 5.54) * mm, "end": v(8.92, 5.7) * mm});
            skLineSegment(sketch, "E335", {"start": v(8.92, 5.7) * mm, "end": v(8.75, 5.7) * mm});
            skLineSegment(sketch, "E336", {"start": v(8.75, 5.7) * mm, "end": v(8.75, 5.87) * mm});
            skLineSegment(sketch, "E337", {"start": v(8.75, 5.87) * mm, "end": v(8.59, 5.87) * mm});
            skLineSegment(sketch, "E338", {"start": v(8.59, 5.87) * mm, "end": v(8.59, 6.03) * mm});
            skLineSegment(sketch, "E339", {"start": v(8.59, 6.03) * mm, "end": v(8.42, 6.03) * mm});
            skLineSegment(sketch, "E340", {"start": v(8.42, 6.03) * mm, "end": v(8.42, 6.2) * mm});
            skLineSegment(sketch, "E341", {"start": v(8.42, 6.2) * mm, "end": v(8.26, 6.2) * mm});
            skLineSegment(sketch, "E342", {"start": v(8.26, 6.2) * mm, "end": v(8.26, 6.36) * mm});
            skLineSegment(sketch, "E343", {"start": v(8.26, 6.36) * mm, "end": v(8.1, 6.36) * mm});
            skLineSegment(sketch, "E344", {"start": v(8.1, 6.36) * mm, "end": v(8.1, 6.53) * mm});
            skLineSegment(sketch, "E345", {"start": v(8.1, 6.53) * mm, "end": v(7.93, 6.53) * mm});
            skLineSegment(sketch, "E346", {"start": v(7.93, 6.53) * mm, "end": v(7.93, 6.69) * mm});
            skLineSegment(sketch, "E347", {"start": v(7.93, 6.69) * mm, "end": v(7.77, 6.69) * mm});
            skLineSegment(sketch, "E348", {"start": v(7.77, 6.69) * mm, "end": v(7.77, 6.85) * mm});
            skLineSegment(sketch, "E349", {"start": v(7.77, 6.85) * mm, "end": v(7.6, 6.85) * mm});
            skLineSegment(sketch, "E350", {"start": v(7.6, 6.85) * mm, "end": v(7.6, 7.02) * mm});
            skLineSegment(sketch, "E351", {"start": v(7.6, 7.02) * mm, "end": v(7.44, 7.02) * mm});
            skLineSegment(sketch, "E352", {"start": v(7.44, 7.02) * mm, "end": v(7.44, 7.18) * mm});
            skLineSegment(sketch, "E353", {"start": v(7.44, 7.18) * mm, "end": v(7.28, 7.18) * mm});
            skLineSegment(sketch, "E354", {"start": v(7.28, 7.18) * mm, "end": v(7.28, 7.35) * mm});
            skLineSegment(sketch, "E355", {"start": v(7.28, 7.35) * mm, "end": v(7.11, 7.35) * mm});
            skLineSegment(sketch, "E356", {"start": v(7.11, 7.35) * mm, "end": v(7.11, 7.5) * mm});
            skLineSegment(sketch, "E357", {"start": v(7.11, 7.5) * mm, "end": v(6.95, 7.5) * mm});
            skLineSegment(sketch, "E358", {"start": v(6.95, 7.5) * mm, "end": v(6.95, 7.67) * mm});
            skLineSegment(sketch, "E359", {"start": v(6.95, 7.67) * mm, "end": v(6.78, 7.67) * mm});
            skLineSegment(sketch, "E360", {"start": v(6.78, 7.67) * mm, "end": v(6.78, 7.84) * mm});
            skLineSegment(sketch, "E361", {"start": v(6.78, 7.84) * mm, "end": v(6.62, 7.84) * mm});
            skLineSegment(sketch, "E362", {"start": v(6.62, 7.84) * mm, "end": v(6.62, 8) * mm});
            skLineSegment(sketch, "E363", {"start": v(6.62, 8) * mm, "end": v(6.46, 8) * mm});
            skLineSegment(sketch, "E364", {"start": v(6.46, 8) * mm, "end": v(6.46, 8.16) * mm});
            skLineSegment(sketch, "E365", {"start": v(6.46, 8.16) * mm, "end": v(6.3, 8.16) * mm});
            skLineSegment(sketch, "E366", {"start": v(6.3, 8.16) * mm, "end": v(6.3, 8.33) * mm});
            skLineSegment(sketch, "E367", {"start": v(6.3, 8.33) * mm, "end": v(6.13, 8.33) * mm});
            skLineSegment(sketch, "E368", {"start": v(6.13, 8.33) * mm, "end": v(6.13, 8.5) * mm});
            skLineSegment(sketch, "E369", {"start": v(6.13, 8.5) * mm, "end": v(5.96, 8.5) * mm});
            skLineSegment(sketch, "E370", {"start": v(5.96, 8.5) * mm, "end": v(5.96, 8.66) * mm});
            skLineSegment(sketch, "E371", {"start": v(5.96, 8.66) * mm, "end": v(5.8, 8.66) * mm});
            skLineSegment(sketch, "E372", {"start": v(5.8, 8.66) * mm, "end": v(5.8, 8.82) * mm});
            skLineSegment(sketch, "E373", {"start": v(5.8, 8.82) * mm, "end": v(5.64, 8.82) * mm});
            skLineSegment(sketch, "E374", {"start": v(5.64, 8.82) * mm, "end": v(5.64, 8.98) * mm});
            skLineSegment(sketch, "E375", {"start": v(5.64, 8.98) * mm, "end": v(5.47, 8.98) * mm});
            skLineSegment(sketch, "E376", {"start": v(5.47, 8.98) * mm, "end": v(5.47, 9.15) * mm});
            skLineSegment(sketch, "E377", {"start": v(5.47, 9.15) * mm, "end": v(5.3, 9.15) * mm});
            skLineSegment(sketch, "E378", {"start": v(5.3, 9.15) * mm, "end": v(5.3, 9.31) * mm});
            skLineSegment(sketch, "E379", {"start": v(5.3, 9.31) * mm, "end": v(5.15, 9.31) * mm});
            skLineSegment(sketch, "E380", {"start": v(5.15, 9.31) * mm, "end": v(5.15, 9.48) * mm});
            skLineSegment(sketch, "E381", {"start": v(5.15, 9.48) * mm, "end": v(4.98, 9.48) * mm});
            skLineSegment(sketch, "E382", {"start": v(4.98, 9.48) * mm, "end": v(4.98, 9.64) * mm});
            skLineSegment(sketch, "E383", {"start": v(4.98, 9.64) * mm, "end": v(4.82, 9.64) * mm});
            skLineSegment(sketch, "E384", {"start": v(4.82, 9.64) * mm, "end": v(4.82, 9.8) * mm});
            skLineSegment(sketch, "E385", {"start": v(4.82, 9.8) * mm, "end": v(4.65, 9.8) * mm});
            skLineSegment(sketch, "E386", {"start": v(4.65, 9.8) * mm, "end": v(4.65, 9.97) * mm});
            skLineSegment(sketch, "E387", {"start": v(4.65, 9.97) * mm, "end": v(4.49, 9.97) * mm});
            skLineSegment(sketch, "E388", {"start": v(4.49, 9.97) * mm, "end": v(4.49, 10.13) * mm});
            skLineSegment(sketch, "E389", {"start": v(4.49, 10.13) * mm, "end": v(4.33, 10.13) * mm});
            skLineSegment(sketch, "E390", {"start": v(4.33, 10.13) * mm, "end": v(4.33, 10.3) * mm});
            skLineSegment(sketch, "E391", {"start": v(4.33, 10.3) * mm, "end": v(4.16, 10.3) * mm});
            skLineSegment(sketch, "E392", {"start": v(4.16, 10.3) * mm, "end": v(4.16, 10.46) * mm});
            skLineSegment(sketch, "E393", {"start": v(4.16, 10.46) * mm, "end": v(4, 10.46) * mm});
            skLineSegment(sketch, "E394", {"start": v(4, 10.46) * mm, "end": v(4, 10.62) * mm});
            skLineSegment(sketch, "E395", {"start": v(4, 10.62) * mm, "end": v(3.83, 10.62) * mm});
            skLineSegment(sketch, "E396", {"start": v(3.83, 10.62) * mm, "end": v(3.83, 10.79) * mm});
            skLineSegment(sketch, "E397", {"start": v(3.83, 10.79) * mm, "end": v(3.67, 10.79) * mm});
            skLineSegment(sketch, "E398", {"start": v(3.67, 10.79) * mm, "end": v(3.67, 10.95) * mm});
            skLineSegment(sketch, "E399", {"start": v(3.67, 10.95) * mm, "end": v(3.5, 10.95) * mm});
            skLineSegment(sketch, "E400", {"start": v(3.5, 10.95) * mm, "end": v(3.5, 11.12) * mm});
            skLineSegment(sketch, "E401", {"start": v(3.5, 11.12) * mm, "end": v(3.34, 11.12) * mm});
            skLineSegment(sketch, "E402", {"start": v(3.34, 11.12) * mm, "end": v(3.34, 11.28) * mm});
            skLineSegment(sketch, "E403", {"start": v(3.34, 11.28) * mm, "end": v(3.18, 11.28) * mm});
            skLineSegment(sketch, "E404", {"start": v(3.18, 11.28) * mm, "end": v(3.18, 11.44) * mm});
            skLineSegment(sketch, "E405", {"start": v(3.18, 11.44) * mm, "end": v(3.01, 11.44) * mm});
            skLineSegment(sketch, "E406", {"start": v(3.01, 11.44) * mm, "end": v(3.01, 11.6) * mm});
            skLineSegment(sketch, "E407", {"start": v(3.01, 11.6) * mm, "end": v(2.85, 11.6) * mm});
            skLineSegment(sketch, "E408", {"start": v(2.85, 11.6) * mm, "end": v(2.85, 11.77) * mm});
            skLineSegment(sketch, "E409", {"start": v(2.85, 11.77) * mm, "end": v(2.69, 11.77) * mm});
            skLineSegment(sketch, "E410", {"start": v(2.69, 11.77) * mm, "end": v(2.69, 11.94) * mm});
            skLineSegment(sketch, "E411", {"start": v(2.69, 11.94) * mm, "end": v(2.52, 11.94) * mm});
            skLineSegment(sketch, "E412", {"start": v(2.52, 11.94) * mm, "end": v(2.52, 12.1) * mm});
            skLineSegment(sketch, "E413", {"start": v(2.52, 12.1) * mm, "end": v(2.36, 12.1) * mm});
            skLineSegment(sketch, "E414", {"start": v(2.36, 12.1) * mm, "end": v(2.36, 12.26) * mm});
            skLineSegment(sketch, "E415", {"start": v(2.36, 12.26) * mm, "end": v(2.2, 12.26) * mm});
            skLineSegment(sketch, "E416", {"start": v(2.2, 12.26) * mm, "end": v(2.2, 12.43) * mm});
            skLineSegment(sketch, "E417", {"start": v(2.2, 12.43) * mm, "end": v(2.03, 12.43) * mm});
            skLineSegment(sketch, "E418", {"start": v(2.03, 12.43) * mm, "end": v(2.03, 12.6) * mm});
            skLineSegment(sketch, "E419", {"start": v(2.03, 12.6) * mm, "end": v(1.87, 12.6) * mm});
            skLineSegment(sketch, "E420", {"start": v(1.87, 12.6) * mm, "end": v(1.87, 12.76) * mm});
            skLineSegment(sketch, "E421", {"start": v(1.87, 12.76) * mm, "end": v(1.7, 12.76) * mm});
            skLineSegment(sketch, "E422", {"start": v(1.7, 12.76) * mm, "end": v(1.7, 12.92) * mm});
            skLineSegment(sketch, "E423", {"start": v(1.7, 12.92) * mm, "end": v(1.54, 12.92) * mm});
            skLineSegment(sketch, "E424", {"start": v(1.54, 12.92) * mm, "end": v(1.54, 13.08) * mm});
            skLineSegment(sketch, "E425", {"start": v(1.54, 13.08) * mm, "end": v(1.37, 13.08) * mm});
            skLineSegment(sketch, "E426", {"start": v(1.37, 13.08) * mm, "end": v(1.37, 13.25) * mm});
            skLineSegment(sketch, "E427", {"start": v(1.37, 13.25) * mm, "end": v(1.21, 13.25) * mm});
            skLineSegment(sketch, "E428", {"start": v(1.21, 13.25) * mm, "end": v(1.21, 13.41) * mm});
            skLineSegment(sketch, "E429", {"start": v(1.21, 13.41) * mm, "end": v(1.05, 13.41) * mm});
            skLineSegment(sketch, "E430", {"start": v(1.05, 13.41) * mm, "end": v(1.05, 13.57) * mm});
            skLineSegment(sketch, "E431", {"start": v(1.05, 13.57) * mm, "end": v(0.88, 13.57) * mm});
            skLineSegment(sketch, "E432", {"start": v(0.88, 13.57) * mm, "end": v(0.88, 13.74) * mm});
            skLineSegment(sketch, "E433", {"start": v(0.88, 13.74) * mm, "end": v(0.72, 13.74) * mm});
            skLineSegment(sketch, "E434", {"start": v(0.72, 13.74) * mm, "end": v(0.72, 13.9) * mm});
            skLineSegment(sketch, "E435", {"start": v(0.72, 13.9) * mm, "end": v(0.55, 13.9) * mm});
            skLineSegment(sketch, "E436", {"start": v(0.55, 13.9) * mm, "end": v(0.55, 14.07) * mm});
            skLineSegment(sketch, "E437", {"start": v(0.55, 14.07) * mm, "end": v(0.4, 14.07) * mm});
            skLineSegment(sketch, "E438", {"start": v(0.4, 14.07) * mm, "end": v(0.4, 14.23) * mm});
            skLineSegment(sketch, "E439", {"start": v(0.4, 14.23) * mm, "end": v(0.06, 14.56) * mm});
            skLineSegment(sketch, "E440", {"start": v(0.06, 14.56) * mm, "end": v(-0.6, 14.72) * mm});
            skLineSegment(sketch, "E441", {"start": v(-0.6, 14.72) * mm, "end": v(-0.6, 14.89) * mm});
            skLineSegment(sketch, "E442", {"start": v(-0.6, 14.89) * mm, "end": v(-0.92, 14.89) * mm});
            skLineSegment(sketch, "E443", {"start": v(-0.92, 14.89) * mm, "end": v(-1.25, 15.21) * mm});
            skLineSegment(sketch, "E444", {"start": v(-1.25, 15.21) * mm, "end": v(-1.9, 15.21) * mm});
            skLineSegment(sketch, "E445", {"start": v(-1.9, 15.21) * mm, "end": v(-1.9, 15.38) * mm});
            skLineSegment(sketch, "E446", {"start": v(-1.9, 15.38) * mm, "end": v(-3.22, 15.38) * mm});
            skLineSegment(sketch, "E447", {"start": v(-11.25, 8.66) * mm, "end": v(-11.58, 8.33) * mm});
            skLineSegment(sketch, "E448", {"start": v(-11.58, 8.33) * mm, "end": v(-11.74, 8.16) * mm});
            skLineSegment(sketch, "E449", {"start": v(-11.74, 8.16) * mm, "end": v(-11.9, 8) * mm});
            skLineSegment(sketch, "E450", {"start": v(-11.9, 8) * mm, "end": v(-11.9, 7.84) * mm});
            skLineSegment(sketch, "E451", {"start": v(-11.9, 7.84) * mm, "end": v(-12.07, 7.84) * mm});
            skLineSegment(sketch, "E452", {"start": v(-12.07, 7.84) * mm, "end": v(-12.07, 7.67) * mm});
            skLineSegment(sketch, "E453", {"start": v(-12.07, 7.67) * mm, "end": v(-12.23, 7.67) * mm});
            skLineSegment(sketch, "E454", {"start": v(-12.23, 7.67) * mm, "end": v(-12.23, 7.5) * mm});
            skLineSegment(sketch, "E455", {"start": v(-12.23, 7.5) * mm, "end": v(-12.4, 7.5) * mm});
            skLineSegment(sketch, "E456", {"start": v(-12.4, 7.5) * mm, "end": v(-12.4, 7.35) * mm});
            skLineSegment(sketch, "E457", {"start": v(-12.4, 7.35) * mm, "end": v(-12.72, 7.18) * mm});
            skLineSegment(sketch, "E458", {"start": v(-12.72, 7.18) * mm, "end": v(-12.89, 7.02) * mm});
            skLineSegment(sketch, "E459", {"start": v(-12.89, 7.02) * mm, "end": v(-12.89, 6.69) * mm});
            skLineSegment(sketch, "E460", {"start": v(-12.89, 6.69) * mm, "end": v(-13.38, 6.53) * mm});
            skLineSegment(sketch, "E461", {"start": v(-13.38, 6.53) * mm, "end": v(-13.7, 6.2) * mm});
            skLineSegment(sketch, "E462", {"start": v(-13.7, 6.2) * mm, "end": v(-13.7, 6.03) * mm});
            skLineSegment(sketch, "E463", {"start": v(-13.7, 6.03) * mm, "end": v(-13.87, 6.03) * mm});
            skLineSegment(sketch, "E464", {"start": v(-13.87, 6.03) * mm, "end": v(-13.87, 5.87) * mm});
            skLineSegment(sketch, "E465", {"start": v(-13.87, 5.87) * mm, "end": v(-14.04, 5.87) * mm});
            skLineSegment(sketch, "E466", {"start": v(-14.04, 5.87) * mm, "end": v(-14.04, 5.7) * mm});
            skLineSegment(sketch, "E467", {"start": v(-14.04, 5.7) * mm, "end": v(-14.2, 5.7) * mm});
            skLineSegment(sketch, "E468", {"start": v(-14.2, 5.7) * mm, "end": v(-14.2, 5.54) * mm});
            skLineSegment(sketch, "E469", {"start": v(-14.2, 5.54) * mm, "end": v(-14.36, 5.54) * mm});
            skLineSegment(sketch, "E470", {"start": v(-14.36, 5.54) * mm, "end": v(-14.36, 5.38) * mm});
            skLineSegment(sketch, "E471", {"start": v(-14.36, 5.38) * mm, "end": v(-14.53, 5.38) * mm});
            skLineSegment(sketch, "E472", {"start": v(-14.53, 5.38) * mm, "end": v(-14.53, 5.21) * mm});
            skLineSegment(sketch, "E473", {"start": v(-14.53, 5.21) * mm, "end": v(-14.7, 5.21) * mm});
            skLineSegment(sketch, "E474", {"start": v(-14.7, 5.21) * mm, "end": v(-14.7, 5.05) * mm});
            skLineSegment(sketch, "E475", {"start": v(-14.7, 5.05) * mm, "end": v(-14.85, 5.05) * mm});
            skLineSegment(sketch, "E476", {"start": v(-14.85, 5.05) * mm, "end": v(-14.85, 4.89) * mm});
            skLineSegment(sketch, "E477", {"start": v(-14.85, 4.89) * mm, "end": v(-15.02, 4.89) * mm});
            skLineSegment(sketch, "E478", {"start": v(-15.02, 4.89) * mm, "end": v(-15.02, 4.72) * mm});
            skLineSegment(sketch, "E479", {"start": v(-15.02, 4.72) * mm, "end": v(-15.18, 4.72) * mm});
            skLineSegment(sketch, "E480", {"start": v(-15.18, 4.72) * mm, "end": v(-15.18, 4.56) * mm});
            skLineSegment(sketch, "E481", {"start": v(-15.18, 4.56) * mm, "end": v(-15.35, 4.56) * mm});
            skLineSegment(sketch, "E482", {"start": v(-15.35, 4.56) * mm, "end": v(-15.35, 4.4) * mm});
            skLineSegment(sketch, "E483", {"start": v(-15.35, 4.4) * mm, "end": v(-15.51, 4.4) * mm});
            skLineSegment(sketch, "E484", {"start": v(-15.51, 4.4) * mm, "end": v(-15.51, 4.23) * mm});
            skLineSegment(sketch, "E485", {"start": v(-15.51, 4.23) * mm, "end": v(-15.67, 4.23) * mm});
            skLineSegment(sketch, "E486", {"start": v(-15.67, 4.23) * mm, "end": v(-15.67, 4.07) * mm});
            skLineSegment(sketch, "E487", {"start": v(-15.67, 4.07) * mm, "end": v(-15.84, 4.07) * mm});
            skLineSegment(sketch, "E488", {"start": v(-15.84, 4.07) * mm, "end": v(-15.84, 3.9) * mm});
            skLineSegment(sketch, "E489", {"start": v(-15.84, 3.9) * mm, "end": v(-16, 3.9) * mm});
            skLineSegment(sketch, "E490", {"start": v(-16, 3.9) * mm, "end": v(-16, 3.74) * mm});
            skLineSegment(sketch, "E491", {"start": v(-16, 3.74) * mm, "end": v(-16.17, 3.74) * mm});
            skLineSegment(sketch, "E492", {"start": v(-16.17, 3.74) * mm, "end": v(-16.17, 3.57) * mm});
            skLineSegment(sketch, "E493", {"start": v(-16.17, 3.57) * mm, "end": v(-16.33, 3.57) * mm});
            skLineSegment(sketch, "E494", {"start": v(-16.33, 3.57) * mm, "end": v(-16.33, 3.41) * mm});
            skLineSegment(sketch, "E495", {"start": v(-16.33, 3.41) * mm, "end": v(-16.5, 3.41) * mm});
            skLineSegment(sketch, "E496", {"start": v(-16.5, 3.41) * mm, "end": v(-16.5, 3.25) * mm});
            skLineSegment(sketch, "E497", {"start": v(-16.5, 3.25) * mm, "end": v(-16.66, 3.25) * mm});
            skLineSegment(sketch, "E498", {"start": v(-16.66, 3.25) * mm, "end": v(-16.66, 3.08) * mm});
            skLineSegment(sketch, "E499", {"start": v(-16.66, 3.08) * mm, "end": v(-16.82, 3.08) * mm});
            skLineSegment(sketch, "E500", {"start": v(-16.82, 3.08) * mm, "end": v(-16.82, 2.92) * mm});
            skLineSegment(sketch, "E501", {"start": v(-16.82, 2.92) * mm, "end": v(-16.99, 2.92) * mm});
            skLineSegment(sketch, "E502", {"start": v(-16.99, 2.92) * mm, "end": v(-16.99, 2.76) * mm});
            skLineSegment(sketch, "E503", {"start": v(-16.99, 2.76) * mm, "end": v(-17.15, 2.76) * mm});
            skLineSegment(sketch, "E504", {"start": v(-17.15, 2.76) * mm, "end": v(-17.15, 2.6) * mm});
            skLineSegment(sketch, "E505", {"start": v(-17.15, 2.6) * mm, "end": v(-17.31, 2.6) * mm});
            skLineSegment(sketch, "E506", {"start": v(-17.31, 2.6) * mm, "end": v(-17.31, 2.43) * mm});
            skLineSegment(sketch, "E507", {"start": v(-17.31, 2.43) * mm, "end": v(-17.48, 2.43) * mm});
            skLineSegment(sketch, "E508", {"start": v(-17.48, 2.43) * mm, "end": v(-17.48, 2.26) * mm});
            skLineSegment(sketch, "E509", {"start": v(-17.48, 2.26) * mm, "end": v(-17.64, 2.26) * mm});
            skLineSegment(sketch, "E510", {"start": v(-17.64, 2.26) * mm, "end": v(-17.64, 2.1) * mm});
            skLineSegment(sketch, "E511", {"start": v(-17.64, 2.1) * mm, "end": v(-17.8, 2.1) * mm});
            skLineSegment(sketch, "E512", {"start": v(-17.8, 2.1) * mm, "end": v(-17.8, 1.94) * mm});
            skLineSegment(sketch, "E513", {"start": v(-17.8, 1.94) * mm, "end": v(-17.97, 1.94) * mm});
            skLineSegment(sketch, "E514", {"start": v(-17.97, 1.94) * mm, "end": v(-17.97, 1.77) * mm});
            skLineSegment(sketch, "E515", {"start": v(-17.97, 1.77) * mm, "end": v(-18.13, 1.77) * mm});
            skLineSegment(sketch, "E516", {"start": v(-18.13, 1.77) * mm, "end": v(-18.13, 1.6) * mm});
            skLineSegment(sketch, "E517", {"start": v(-18.13, 1.6) * mm, "end": v(-18.46, 1.12) * mm});
            skLineSegment(sketch, "E518", {"start": v(-18.46, 1.12) * mm, "end": v(-17.8, 0.62) * mm});
            skLineSegment(sketch, "E519", {"start": v(-17.8, 0.62) * mm, "end": v(-17.15, 0.46) * mm});
            skLineSegment(sketch, "E520", {"start": v(-17.15, 0.46) * mm, "end": v(-17.15, 0.3) * mm});
            skLineSegment(sketch, "E521", {"start": v(-17.15, 0.3) * mm, "end": v(-16.82, 0.3) * mm});
            skLineSegment(sketch, "E522", {"start": v(-16.82, 0.3) * mm, "end": v(-16.5, -0.03) * mm});
            skLineSegment(sketch, "E523", {"start": v(-16.5, -0.03) * mm, "end": v(-15.51, -0.03) * mm});
            skLineSegment(sketch, "E524", {"start": v(-15.51, -0.03) * mm, "end": v(-15.51, -0.2) * mm});
            skLineSegment(sketch, "E525", {"start": v(-15.51, -0.2) * mm, "end": v(-14.53, -0.2) * mm});
            skLineSegment(sketch, "E526", {"start": v(-14.53, -0.2) * mm, "end": v(-14.53, -0.03) * mm});
            skLineSegment(sketch, "E527", {"start": v(-14.53, -0.03) * mm, "end": v(-14.04, -0.03) * mm});
            skLineSegment(sketch, "E528", {"start": v(-14.04, -0.03) * mm, "end": v(-12.89, -0.03) * mm});
            skLineSegment(sketch, "E529", {"start": v(-12.89, -0.03) * mm, "end": v(-12.89, 0.13) * mm});
            skLineSegment(sketch, "E530", {"start": v(-12.89, 0.13) * mm, "end": v(-12.4, 0.13) * mm});
            skLineSegment(sketch, "E531", {"start": v(-12.4, 0.13) * mm, "end": v(-11.74, 0.13) * mm});
            skLineSegment(sketch, "E532", {"start": v(-11.74, 0.13) * mm, "end": v(-11.58, 0.13) * mm});
            skLineSegment(sketch, "E533", {"start": v(-11.58, 0.13) * mm, "end": v(-11.41, 0.13) * mm});
            skLineSegment(sketch, "E534", {"start": v(-11.41, 0.13) * mm, "end": v(-11.25, 0.13) * mm});
            skLineSegment(sketch, "E535", {"start": v(-11.25, 0.13) * mm, "end": v(-10.6, 0.13) * mm});
            skLineSegment(sketch, "E536", {"start": v(-10.6, 0.13) * mm, "end": v(-10.6, 0.3) * mm});
            skLineSegment(sketch, "E537", {"start": v(-10.6, 0.3) * mm, "end": v(-10.1, 0.3) * mm});
            skLineSegment(sketch, "E538", {"start": v(-10.1, 0.3) * mm, "end": v(-9.45, 0.3) * mm});
            skLineSegment(sketch, "E539", {"start": v(-9.45, 0.3) * mm, "end": v(-9.28, 0.3) * mm});
            skLineSegment(sketch, "E540", {"start": v(-9.28, 0.3) * mm, "end": v(-9.12, 0.3) * mm});
            skLineSegment(sketch, "E541", {"start": v(-9.12, 0.3) * mm, "end": v(-8.95, 0.3) * mm});
            skLineSegment(sketch, "E542", {"start": v(-8.95, 0.3) * mm, "end": v(-8.79, 0.3) * mm});
            skLineSegment(sketch, "E543", {"start": v(-8.79, 0.3) * mm, "end": v(-8.63, 0.3) * mm});
            skLineSegment(sketch, "E544", {"start": v(-8.63, 0.3) * mm, "end": v(-8.46, 0.3) * mm});
            skLineSegment(sketch, "E545", {"start": v(-8.46, 0.3) * mm, "end": v(-8.3, 0.3) * mm});
            skLineSegment(sketch, "E546", {"start": v(-8.3, 0.3) * mm, "end": v(-7.15, 0.3) * mm});
            skLineSegment(sketch, "E547", {"start": v(-7.15, 0.3) * mm, "end": v(-7.15, 0.46) * mm});
            skLineSegment(sketch, "E548", {"start": v(-7.15, 0.46) * mm, "end": v(-6.66, 0.46) * mm});
            skLineSegment(sketch, "E549", {"start": v(-6.66, 0.46) * mm, "end": v(-6, 0.46) * mm});
            skLineSegment(sketch, "E550", {"start": v(-6, 0.46) * mm, "end": v(-5.84, 0.46) * mm});
            skLineSegment(sketch, "E551", {"start": v(-5.84, 0.46) * mm, "end": v(-5.67, 0.46) * mm});
            skLineSegment(sketch, "E552", {"start": v(-5.67, 0.46) * mm, "end": v(-5.51, 0.46) * mm});
            skLineSegment(sketch, "E553", {"start": v(-5.51, 0.46) * mm, "end": v(-5.35, 0.46) * mm});
            skLineSegment(sketch, "E554", {"start": v(-5.35, 0.46) * mm, "end": v(-5.18, 0.46) * mm});
            skLineSegment(sketch, "E555", {"start": v(-5.18, 0.46) * mm, "end": v(-5.02, 0.46) * mm});
            skLineSegment(sketch, "E556", {"start": v(-5.02, 0.46) * mm, "end": v(-4.85, 0.46) * mm});
            skLineSegment(sketch, "E557", {"start": v(-4.85, 0.46) * mm, "end": v(-4.7, 0.46) * mm});
            skLineSegment(sketch, "E558", {"start": v(-4.7, 0.46) * mm, "end": v(-4.53, 0.46) * mm});
            skLineSegment(sketch, "E559", {"start": v(-4.53, 0.46) * mm, "end": v(-4.36, 0.46) * mm});
            skLineSegment(sketch, "E560", {"start": v(-4.36, 0.46) * mm, "end": v(-4.2, 0.46) * mm});
            skLineSegment(sketch, "E561", {"start": v(-4.2, 0.46) * mm, "end": v(-4.04, 0.46) * mm});
            skLineSegment(sketch, "E562", {"start": v(-4.04, 0.46) * mm, "end": v(-3.87, 0.46) * mm});
            skLineSegment(sketch, "E563", {"start": v(-3.87, 0.46) * mm, "end": v(-3.7, 0.46) * mm});
            skLineSegment(sketch, "E564", {"start": v(-3.7, 0.46) * mm, "end": v(-3.54, 0.46) * mm});
            skLineSegment(sketch, "E565", {"start": v(-3.54, 0.46) * mm, "end": v(-2.56, 0.46) * mm});
            skLineSegment(sketch, "E566", {"start": v(-2.56, 0.46) * mm, "end": v(-2.56, 0.3) * mm});
            skLineSegment(sketch, "E567", {"start": v(-2.56, 0.3) * mm, "end": v(-2.07, 0.3) * mm});
            skLineSegment(sketch, "E568", {"start": v(-2.07, 0.3) * mm, "end": v(-1.41, 0.3) * mm});
            skLineSegment(sketch, "E569", {"start": v(-1.41, 0.3) * mm, "end": v(-1.25, 0.3) * mm});
            skLineSegment(sketch, "E570", {"start": v(-1.25, 0.3) * mm, "end": v(-1.08, 0.3) * mm});
            skLineSegment(sketch, "E571", {"start": v(-1.08, 0.3) * mm, "end": v(-0.92, 0.3) * mm});
            skLineSegment(sketch, "E572", {"start": v(-0.92, 0.3) * mm, "end": v(-0.76, 0.3) * mm});
            skLineSegment(sketch, "E573", {"start": v(-0.76, 0.3) * mm, "end": v(-0.6, 0.3) * mm});
            skLineSegment(sketch, "E574", {"start": v(-0.6, 0.3) * mm, "end": v(-0.43, 0.3) * mm});
            skLineSegment(sketch, "E575", {"start": v(-0.43, 0.3) * mm, "end": v(-0.26, 0.3) * mm});
            skLineSegment(sketch, "E576", {"start": v(-0.26, 0.3) * mm, "end": v(0.88, 0.3) * mm});
            skLineSegment(sketch, "E577", {"start": v(0.88, 0.3) * mm, "end": v(0.88, 0.13) * mm});
            skLineSegment(sketch, "E578", {"start": v(0.88, 0.13) * mm, "end": v(1.37, 0.13) * mm});
            skLineSegment(sketch, "E579", {"start": v(1.37, 0.13) * mm, "end": v(2.03, 0.13) * mm});
            skLineSegment(sketch, "E580", {"start": v(2.03, 0.13) * mm, "end": v(2.2, 0.13) * mm});
            skLineSegment(sketch, "E581", {"start": v(2.2, 0.13) * mm, "end": v(2.36, 0.13) * mm});
            skLineSegment(sketch, "E582", {"start": v(2.36, 0.13) * mm, "end": v(2.52, 0.13) * mm});
            skLineSegment(sketch, "E583", {"start": v(2.52, 0.13) * mm, "end": v(3.18, 0.13) * mm});
            skLineSegment(sketch, "E584", {"start": v(3.18, 0.13) * mm, "end": v(3.18, -0.03) * mm});
            skLineSegment(sketch, "E585", {"start": v(3.18, -0.03) * mm, "end": v(3.67, -0.03) * mm});
            skLineSegment(sketch, "E586", {"start": v(3.67, -0.03) * mm, "end": v(4.82, -0.03) * mm});
            skLineSegment(sketch, "E587", {"start": v(4.82, -0.03) * mm, "end": v(4.82, -0.2) * mm});
            skLineSegment(sketch, "E588", {"start": v(4.82, -0.2) * mm, "end": v(5.3, -0.2) * mm});
            skLineSegment(sketch, "E589", {"start": v(5.3, -0.2) * mm, "end": v(5.8, -0.2) * mm});
            skLineSegment(sketch, "E590", {"start": v(5.8, -0.2) * mm, "end": v(6.3, -0.2) * mm});
            skLineSegment(sketch, "E591", {"start": v(6.3, -0.2) * mm, "end": v(6.3, -0.36) * mm});
            skLineSegment(sketch, "E592", {"start": v(6.3, -0.36) * mm, "end": v(7.44, -0.36) * mm});
            skLineSegment(sketch, "E593", {"start": v(7.44, -0.36) * mm, "end": v(7.44, -0.52) * mm});
            skLineSegment(sketch, "E594", {"start": v(7.44, -0.52) * mm, "end": v(8.42, -0.52) * mm});
            skLineSegment(sketch, "E595", {"start": v(8.42, -0.52) * mm, "end": v(8.1, -0.2) * mm});
            skLineSegment(sketch, "E596", {"start": v(8.1, -0.2) * mm, "end": v(8.1, -0.03) * mm});
            skLineSegment(sketch, "E597", {"start": v(8.1, -0.03) * mm, "end": v(7.93, -0.03) * mm});
            skLineSegment(sketch, "E598", {"start": v(7.93, -0.03) * mm, "end": v(7.93, 0.13) * mm});
            skLineSegment(sketch, "E599", {"start": v(7.93, 0.13) * mm, "end": v(7.77, 0.13) * mm});
            skLineSegment(sketch, "E600", {"start": v(7.77, 0.13) * mm, "end": v(7.77, 0.3) * mm});
            skLineSegment(sketch, "E601", {"start": v(7.77, 0.3) * mm, "end": v(7.6, 0.3) * mm});
            skLineSegment(sketch, "E602", {"start": v(7.6, 0.3) * mm, "end": v(7.6, 0.46) * mm});
            skLineSegment(sketch, "E603", {"start": v(7.6, 0.46) * mm, "end": v(7.44, 0.46) * mm});
            skLineSegment(sketch, "E604", {"start": v(7.44, 0.46) * mm, "end": v(7.44, 0.62) * mm});
            skLineSegment(sketch, "E605", {"start": v(7.44, 0.62) * mm, "end": v(7.28, 0.62) * mm});
            skLineSegment(sketch, "E606", {"start": v(7.28, 0.62) * mm, "end": v(7.28, 0.79) * mm});
            skLineSegment(sketch, "E607", {"start": v(7.28, 0.79) * mm, "end": v(7.11, 0.79) * mm});
            skLineSegment(sketch, "E608", {"start": v(7.11, 0.79) * mm, "end": v(7.11, 0.95) * mm});
            skLineSegment(sketch, "E609", {"start": v(7.11, 0.95) * mm, "end": v(6.95, 0.95) * mm});
            skLineSegment(sketch, "E610", {"start": v(6.95, 0.95) * mm, "end": v(6.95, 1.12) * mm});
            skLineSegment(sketch, "E611", {"start": v(6.95, 1.12) * mm, "end": v(6.78, 1.12) * mm});
            skLineSegment(sketch, "E612", {"start": v(6.78, 1.12) * mm, "end": v(6.78, 1.28) * mm});
            skLineSegment(sketch, "E613", {"start": v(6.78, 1.28) * mm, "end": v(6.62, 1.28) * mm});
            skLineSegment(sketch, "E614", {"start": v(6.62, 1.28) * mm, "end": v(6.62, 1.44) * mm});
            skLineSegment(sketch, "E615", {"start": v(6.62, 1.44) * mm, "end": v(6.46, 1.44) * mm});
            skLineSegment(sketch, "E616", {"start": v(6.46, 1.44) * mm, "end": v(6.46, 1.6) * mm});
            skLineSegment(sketch, "E617", {"start": v(6.46, 1.6) * mm, "end": v(6.3, 1.6) * mm});
            skLineSegment(sketch, "E618", {"start": v(6.3, 1.6) * mm, "end": v(6.3, 1.77) * mm});
            skLineSegment(sketch, "E619", {"start": v(6.3, 1.77) * mm, "end": v(6.13, 1.77) * mm});
            skLineSegment(sketch, "E620", {"start": v(6.13, 1.77) * mm, "end": v(6.13, 1.94) * mm});
            skLineSegment(sketch, "E621", {"start": v(6.13, 1.94) * mm, "end": v(5.96, 1.94) * mm});
            skLineSegment(sketch, "E622", {"start": v(5.96, 1.94) * mm, "end": v(5.96, 2.1) * mm});
            skLineSegment(sketch, "E623", {"start": v(5.96, 2.1) * mm, "end": v(5.8, 2.1) * mm});
            skLineSegment(sketch, "E624", {"start": v(5.8, 2.1) * mm, "end": v(5.8, 2.26) * mm});
            skLineSegment(sketch, "E625", {"start": v(5.8, 2.26) * mm, "end": v(5.64, 2.26) * mm});
            skLineSegment(sketch, "E626", {"start": v(5.64, 2.26) * mm, "end": v(5.64, 2.43) * mm});
            skLineSegment(sketch, "E627", {"start": v(5.64, 2.43) * mm, "end": v(5.47, 2.43) * mm});
            skLineSegment(sketch, "E628", {"start": v(5.47, 2.43) * mm, "end": v(5.47, 2.6) * mm});
            skLineSegment(sketch, "E629", {"start": v(5.47, 2.6) * mm, "end": v(5.3, 2.6) * mm});
            skLineSegment(sketch, "E630", {"start": v(5.3, 2.6) * mm, "end": v(5.3, 2.76) * mm});
            skLineSegment(sketch, "E631", {"start": v(5.3, 2.76) * mm, "end": v(5.15, 2.76) * mm});
            skLineSegment(sketch, "E632", {"start": v(5.15, 2.76) * mm, "end": v(5.15, 2.92) * mm});
            skLineSegment(sketch, "E633", {"start": v(5.15, 2.92) * mm, "end": v(4.98, 2.92) * mm});
            skLineSegment(sketch, "E634", {"start": v(4.98, 2.92) * mm, "end": v(4.98, 3.08) * mm});
            skLineSegment(sketch, "E635", {"start": v(4.98, 3.08) * mm, "end": v(4.82, 3.08) * mm});
            skLineSegment(sketch, "E636", {"start": v(4.82, 3.08) * mm, "end": v(4.82, 3.25) * mm});
            skLineSegment(sketch, "E637", {"start": v(4.82, 3.25) * mm, "end": v(4.65, 3.25) * mm});
            skLineSegment(sketch, "E638", {"start": v(4.65, 3.25) * mm, "end": v(4.65, 3.41) * mm});
            skLineSegment(sketch, "E639", {"start": v(4.65, 3.41) * mm, "end": v(4.49, 3.41) * mm});
            skLineSegment(sketch, "E640", {"start": v(4.49, 3.41) * mm, "end": v(4.49, 3.57) * mm});
            skLineSegment(sketch, "E641", {"start": v(4.49, 3.57) * mm, "end": v(4.33, 3.57) * mm});
            skLineSegment(sketch, "E642", {"start": v(4.33, 3.57) * mm, "end": v(4.33, 3.74) * mm});
            skLineSegment(sketch, "E643", {"start": v(4.33, 3.74) * mm, "end": v(4.16, 3.74) * mm});
            skLineSegment(sketch, "E644", {"start": v(4.16, 3.74) * mm, "end": v(4.16, 3.9) * mm});
            skLineSegment(sketch, "E645", {"start": v(4.16, 3.9) * mm, "end": v(4, 3.9) * mm});
            skLineSegment(sketch, "E646", {"start": v(4, 3.9) * mm, "end": v(4, 4.07) * mm});
            skLineSegment(sketch, "E647", {"start": v(4, 4.07) * mm, "end": v(3.83, 4.07) * mm});
            skLineSegment(sketch, "E648", {"start": v(3.83, 4.07) * mm, "end": v(3.83, 4.23) * mm});
            skLineSegment(sketch, "E649", {"start": v(3.83, 4.23) * mm, "end": v(3.67, 4.23) * mm});
            skLineSegment(sketch, "E650", {"start": v(3.67, 4.23) * mm, "end": v(3.67, 4.4) * mm});
            skLineSegment(sketch, "E651", {"start": v(3.67, 4.4) * mm, "end": v(3.5, 4.4) * mm});
            skLineSegment(sketch, "E652", {"start": v(3.5, 4.4) * mm, "end": v(3.5, 4.56) * mm});
            skLineSegment(sketch, "E653", {"start": v(3.5, 4.56) * mm, "end": v(3.34, 4.56) * mm});
            skLineSegment(sketch, "E654", {"start": v(3.34, 4.56) * mm, "end": v(3.34, 4.72) * mm});
            skLineSegment(sketch, "E655", {"start": v(3.34, 4.72) * mm, "end": v(3.18, 4.72) * mm});
            skLineSegment(sketch, "E656", {"start": v(3.18, 4.72) * mm, "end": v(3.18, 4.89) * mm});
            skLineSegment(sketch, "E657", {"start": v(3.18, 4.89) * mm, "end": v(3.01, 4.89) * mm});
            skLineSegment(sketch, "E658", {"start": v(3.01, 4.89) * mm, "end": v(3.01, 5.05) * mm});
            skLineSegment(sketch, "E659", {"start": v(3.01, 5.05) * mm, "end": v(2.85, 5.05) * mm});
            skLineSegment(sketch, "E660", {"start": v(2.85, 5.05) * mm, "end": v(2.85, 5.21) * mm});
            skLineSegment(sketch, "E661", {"start": v(2.85, 5.21) * mm, "end": v(2.69, 5.21) * mm});
            skLineSegment(sketch, "E662", {"start": v(2.69, 5.21) * mm, "end": v(2.69, 5.38) * mm});
            skLineSegment(sketch, "E663", {"start": v(2.69, 5.38) * mm, "end": v(2.52, 5.38) * mm});
            skLineSegment(sketch, "E664", {"start": v(2.52, 5.38) * mm, "end": v(2.52, 5.54) * mm});
            skLineSegment(sketch, "E665", {"start": v(2.52, 5.54) * mm, "end": v(2.36, 5.54) * mm});
            skLineSegment(sketch, "E666", {"start": v(2.36, 5.54) * mm, "end": v(2.36, 5.7) * mm});
            skLineSegment(sketch, "E667", {"start": v(2.36, 5.7) * mm, "end": v(2.03, 6.03) * mm});
            skLineSegment(sketch, "E668", {"start": v(2.03, 6.03) * mm, "end": v(1.7, 6.03) * mm});
            skLineSegment(sketch, "E669", {"start": v(1.7, 6.03) * mm, "end": v(1.54, 6.36) * mm});
            skLineSegment(sketch, "E670", {"start": v(1.54, 6.36) * mm, "end": v(0.88, 6.53) * mm});
            skLineSegment(sketch, "E671", {"start": v(0.88, 6.53) * mm, "end": v(0.55, 6.53) * mm});
            skLineSegment(sketch, "E672", {"start": v(0.55, 6.53) * mm, "end": v(0.06, 6.36) * mm});
            skLineSegment(sketch, "E673", {"start": v(0.06, 6.36) * mm, "end": v(-0.6, 6.03) * mm});
            skLineSegment(sketch, "E674", {"start": v(-0.6, 6.03) * mm, "end": v(-0.76, 5.54) * mm});
            skLineSegment(sketch, "E675", {"start": v(-0.76, 5.54) * mm, "end": v(-1.25, 5.38) * mm});
            skLineSegment(sketch, "E676", {"start": v(-1.25, 5.38) * mm, "end": v(-1.41, 5.21) * mm});
            skLineSegment(sketch, "E677", {"start": v(-1.41, 5.21) * mm, "end": v(-1.58, 4.72) * mm});
            skLineSegment(sketch, "E678", {"start": v(-1.58, 4.72) * mm, "end": v(-2.07, 4.56) * mm});
            skLineSegment(sketch, "E679", {"start": v(-2.07, 4.56) * mm, "end": v(-2.23, 4.07) * mm});
            skLineSegment(sketch, "E680", {"start": v(-2.23, 4.07) * mm, "end": v(-2.56, 3.74) * mm});
            skLineSegment(sketch, "E681", {"start": v(-2.56, 3.74) * mm, "end": v(-3.05, 3.57) * mm});
            skLineSegment(sketch, "E682", {"start": v(-3.05, 3.57) * mm, "end": v(-3.22, 3.25) * mm});
            skLineSegment(sketch, "E683", {"start": v(-3.22, 3.25) * mm, "end": v(-3.7, 2.92) * mm});
            skLineSegment(sketch, "E684", {"start": v(-3.7, 2.92) * mm, "end": v(-5.02, 2.92) * mm});
            skLineSegment(sketch, "E685", {"start": v(-5.02, 2.92) * mm, "end": v(-5.51, 3.25) * mm});
            skLineSegment(sketch, "E686", {"start": v(-5.51, 3.25) * mm, "end": v(-5.84, 3.57) * mm});
            skLineSegment(sketch, "E687", {"start": v(-5.84, 3.57) * mm, "end": v(-5.84, 3.74) * mm});
            skLineSegment(sketch, "E688", {"start": v(-5.84, 3.74) * mm, "end": v(-6, 3.74) * mm});
            skLineSegment(sketch, "E689", {"start": v(-6, 3.74) * mm, "end": v(-6, 3.9) * mm});
            skLineSegment(sketch, "E690", {"start": v(-6, 3.9) * mm, "end": v(-6.17, 3.9) * mm});
            skLineSegment(sketch, "E691", {"start": v(-6.17, 3.9) * mm, "end": v(-6.17, 4.07) * mm});
            skLineSegment(sketch, "E692", {"start": v(-6.17, 4.07) * mm, "end": v(-6.33, 4.07) * mm});
            skLineSegment(sketch, "E693", {"start": v(-6.33, 4.07) * mm, "end": v(-6.33, 4.23) * mm});
            skLineSegment(sketch, "E694", {"start": v(-6.33, 4.23) * mm, "end": v(-6.5, 4.23) * mm});
            skLineSegment(sketch, "E695", {"start": v(-6.5, 4.23) * mm, "end": v(-6.5, 4.4) * mm});
            skLineSegment(sketch, "E696", {"start": v(-6.5, 4.4) * mm, "end": v(-6.66, 4.4) * mm});
            skLineSegment(sketch, "E697", {"start": v(-6.66, 4.4) * mm, "end": v(-6.66, 4.56) * mm});
            skLineSegment(sketch, "E698", {"start": v(-6.66, 4.56) * mm, "end": v(-6.82, 4.56) * mm});
            skLineSegment(sketch, "E699", {"start": v(-6.82, 4.56) * mm, "end": v(-6.82, 4.72) * mm});
            skLineSegment(sketch, "E700", {"start": v(-6.82, 4.72) * mm, "end": v(-6.99, 4.72) * mm});
            skLineSegment(sketch, "E701", {"start": v(-6.99, 4.72) * mm, "end": v(-6.99, 4.89) * mm});
            skLineSegment(sketch, "E702", {"start": v(-6.99, 4.89) * mm, "end": v(-7.15, 4.89) * mm});
            skLineSegment(sketch, "E703", {"start": v(-7.15, 4.89) * mm, "end": v(-7.15, 5.05) * mm});
            skLineSegment(sketch, "E704", {"start": v(-7.15, 5.05) * mm, "end": v(-7.31, 5.05) * mm});
            skLineSegment(sketch, "E705", {"start": v(-7.31, 5.05) * mm, "end": v(-7.31, 5.21) * mm});
            skLineSegment(sketch, "E706", {"start": v(-7.31, 5.21) * mm, "end": v(-7.48, 5.21) * mm});
            skLineSegment(sketch, "E707", {"start": v(-7.48, 5.21) * mm, "end": v(-7.48, 5.38) * mm});
            skLineSegment(sketch, "E708", {"start": v(-7.48, 5.38) * mm, "end": v(-7.64, 5.38) * mm});
            skLineSegment(sketch, "E709", {"start": v(-7.64, 5.38) * mm, "end": v(-7.64, 5.54) * mm});
            skLineSegment(sketch, "E710", {"start": v(-7.64, 5.54) * mm, "end": v(-7.8, 5.54) * mm});
            skLineSegment(sketch, "E711", {"start": v(-7.8, 5.54) * mm, "end": v(-7.8, 5.7) * mm});
            skLineSegment(sketch, "E712", {"start": v(-7.8, 5.7) * mm, "end": v(-7.97, 5.7) * mm});
            skLineSegment(sketch, "E713", {"start": v(-7.97, 5.7) * mm, "end": v(-7.97, 5.87) * mm});
            skLineSegment(sketch, "E714", {"start": v(-7.97, 5.87) * mm, "end": v(-8.13, 5.87) * mm});
            skLineSegment(sketch, "E715", {"start": v(-8.13, 5.87) * mm, "end": v(-8.13, 6.03) * mm});
            skLineSegment(sketch, "E716", {"start": v(-8.13, 6.03) * mm, "end": v(-8.3, 6.03) * mm});
            skLineSegment(sketch, "E717", {"start": v(-8.3, 6.03) * mm, "end": v(-8.3, 6.2) * mm});
            skLineSegment(sketch, "E718", {"start": v(-8.3, 6.2) * mm, "end": v(-8.46, 6.2) * mm});
            skLineSegment(sketch, "E719", {"start": v(-8.46, 6.2) * mm, "end": v(-8.46, 6.36) * mm});
            skLineSegment(sketch, "E720", {"start": v(-8.46, 6.36) * mm, "end": v(-8.63, 6.36) * mm});
            skLineSegment(sketch, "E721", {"start": v(-8.63, 6.36) * mm, "end": v(-8.63, 6.53) * mm});
            skLineSegment(sketch, "E722", {"start": v(-8.63, 6.53) * mm, "end": v(-8.79, 6.53) * mm});
            skLineSegment(sketch, "E723", {"start": v(-8.79, 6.53) * mm, "end": v(-8.79, 6.69) * mm});
            skLineSegment(sketch, "E724", {"start": v(-8.79, 6.69) * mm, "end": v(-8.95, 6.69) * mm});
            skLineSegment(sketch, "E725", {"start": v(-8.95, 6.69) * mm, "end": v(-8.95, 6.85) * mm});
            skLineSegment(sketch, "E726", {"start": v(-8.95, 6.85) * mm, "end": v(-9.12, 6.85) * mm});
            skLineSegment(sketch, "E727", {"start": v(-9.12, 6.85) * mm, "end": v(-9.12, 7.02) * mm});
            skLineSegment(sketch, "E728", {"start": v(-9.12, 7.02) * mm, "end": v(-9.28, 7.02) * mm});
            skLineSegment(sketch, "E729", {"start": v(-9.28, 7.02) * mm, "end": v(-9.28, 7.18) * mm});
            skLineSegment(sketch, "E730", {"start": v(-9.28, 7.18) * mm, "end": v(-9.45, 7.18) * mm});
            skLineSegment(sketch, "E731", {"start": v(-9.45, 7.18) * mm, "end": v(-9.45, 7.35) * mm});
            skLineSegment(sketch, "E732", {"start": v(-9.45, 7.35) * mm, "end": v(-9.6, 7.35) * mm});
            skLineSegment(sketch, "E733", {"start": v(-9.6, 7.35) * mm, "end": v(-9.6, 7.5) * mm});
            skLineSegment(sketch, "E734", {"start": v(-9.6, 7.5) * mm, "end": v(-9.94, 7.84) * mm});
            skLineSegment(sketch, "E735", {"start": v(-9.94, 7.84) * mm, "end": v(-10.1, 8) * mm});
            skLineSegment(sketch, "E736", {"start": v(-10.1, 8) * mm, "end": v(-10.43, 8) * mm});
            skLineSegment(sketch, "E737", {"start": v(-10.43, 8) * mm, "end": v(-10.76, 8.66) * mm});
            skLineSegment(sketch, "E738", {"start": v(-10.76, 8.66) * mm, "end": v(-11.25, 8.66) * mm});
            skLineSegment(sketch, "E739", {"start": v(-23.87, -3.8) * mm, "end": v(-24.36, -4.3) * mm});
            skLineSegment(sketch, "E740", {"start": v(-24.36, -4.3) * mm, "end": v(-24.36, -4.95) * mm});
            skLineSegment(sketch, "E741", {"start": v(-24.36, -4.95) * mm, "end": v(-24.36, -5.11) * mm});
            skLineSegment(sketch, "E742", {"start": v(-24.36, -5.11) * mm, "end": v(-24.36, -5.28) * mm});
            skLineSegment(sketch, "E743", {"start": v(-24.36, -5.28) * mm, "end": v(-24.36, -5.44) * mm});
            skLineSegment(sketch, "E744", {"start": v(-24.36, -5.44) * mm, "end": v(-24.2, -6.92) * mm});
            skLineSegment(sketch, "E745", {"start": v(-24.2, -6.92) * mm, "end": v(-24.04, -7.08) * mm});
            skLineSegment(sketch, "E746", {"start": v(-24.04, -7.08) * mm, "end": v(-23.7, -7.24) * mm});
            skLineSegment(sketch, "E747", {"start": v(-23.7, -7.24) * mm, "end": v(-23.05, -7.24) * mm});
            skLineSegment(sketch, "E748", {"start": v(-23.05, -7.24) * mm, "end": v(-22.89, -7.24) * mm});
            skLineSegment(sketch, "E749", {"start": v(-22.89, -7.24) * mm, "end": v(-22.72, -7.24) * mm});
            skLineSegment(sketch, "E750", {"start": v(-22.72, -7.24) * mm, "end": v(-22.56, -7.24) * mm});
            skLineSegment(sketch, "E751", {"start": v(-22.56, -7.24) * mm, "end": v(-22.4, -7.24) * mm});
            skLineSegment(sketch, "E752", {"start": v(-22.4, -7.24) * mm, "end": v(-22.23, -7.24) * mm});
            skLineSegment(sketch, "E753", {"start": v(-22.23, -7.24) * mm, "end": v(-22.07, -7.24) * mm});
            skLineSegment(sketch, "E754", {"start": v(-22.07, -7.24) * mm, "end": v(-21.9, -7.24) * mm});
            skLineSegment(sketch, "E755", {"start": v(-21.9, -7.24) * mm, "end": v(-21.74, -7.24) * mm});
            skLineSegment(sketch, "E756", {"start": v(-21.74, -7.24) * mm, "end": v(-21.58, -7.24) * mm});
            skLineSegment(sketch, "E757", {"start": v(-21.58, -7.24) * mm, "end": v(-21.41, -7.24) * mm});
            skLineSegment(sketch, "E758", {"start": v(-21.41, -7.24) * mm, "end": v(-21.25, -7.24) * mm});
            skLineSegment(sketch, "E759", {"start": v(-21.25, -7.24) * mm, "end": v(-21.08, -7.24) * mm});
            skLineSegment(sketch, "E760", {"start": v(-21.08, -7.24) * mm, "end": v(-20.92, -7.24) * mm});
            skLineSegment(sketch, "E761", {"start": v(-20.92, -7.24) * mm, "end": v(-20.76, -7.24) * mm});
            skLineSegment(sketch, "E762", {"start": v(-20.76, -7.24) * mm, "end": v(-20.6, -7.24) * mm});
            skLineSegment(sketch, "E763", {"start": v(-20.6, -7.24) * mm, "end": v(-19.6, -7.24) * mm});
            skLineSegment(sketch, "E764", {"start": v(-19.6, -7.24) * mm, "end": v(-19.6, -8.23) * mm});
            skLineSegment(sketch, "E765", {"start": v(-19.6, -8.23) * mm, "end": v(-20.26, -8.23) * mm});
            skLineSegment(sketch, "E766", {"start": v(-20.26, -8.23) * mm, "end": v(-20.43, -8.23) * mm});
            skLineSegment(sketch, "E767", {"start": v(-20.43, -8.23) * mm, "end": v(-20.6, -8.23) * mm});
            skLineSegment(sketch, "E768", {"start": v(-20.6, -8.23) * mm, "end": v(-20.76, -8.23) * mm});
            skLineSegment(sketch, "E769", {"start": v(-20.76, -8.23) * mm, "end": v(-20.92, -8.23) * mm});
            skLineSegment(sketch, "E770", {"start": v(-20.92, -8.23) * mm, "end": v(-21.08, -8.23) * mm});
            skLineSegment(sketch, "E771", {"start": v(-21.08, -8.23) * mm, "end": v(-21.25, -8.23) * mm});
            skLineSegment(sketch, "E772", {"start": v(-21.25, -8.23) * mm, "end": v(-21.41, -8.23) * mm});
            skLineSegment(sketch, "E773", {"start": v(-21.41, -8.23) * mm, "end": v(-21.58, -8.23) * mm});
            skLineSegment(sketch, "E774", {"start": v(-21.58, -8.23) * mm, "end": v(-21.74, -8.23) * mm});
            skLineSegment(sketch, "E775", {"start": v(-21.74, -8.23) * mm, "end": v(-21.9, -8.23) * mm});
            skLineSegment(sketch, "E776", {"start": v(-21.9, -8.23) * mm, "end": v(-22.07, -8.23) * mm});
            skLineSegment(sketch, "E777", {"start": v(-22.07, -8.23) * mm, "end": v(-23.22, -8.23) * mm});
            skLineSegment(sketch, "E778", {"start": v(-23.22, -8.23) * mm, "end": v(-23.22, -7.57) * mm});
            skLineSegment(sketch, "E779", {"start": v(-23.22, -7.57) * mm, "end": v(-23.7, -7.74) * mm});
            skLineSegment(sketch, "E780", {"start": v(-23.7, -7.74) * mm, "end": v(-24.53, -7.74) * mm});
            skLineSegment(sketch, "E781", {"start": v(-24.53, -7.74) * mm, "end": v(-24.7, -7.9) * mm});
            skLineSegment(sketch, "E782", {"start": v(-24.7, -7.9) * mm, "end": v(-24.7, -8.72) * mm});
            skLineSegment(sketch, "E783", {"start": v(-24.7, -8.72) * mm, "end": v(-24.36, -9.38) * mm});
            skLineSegment(sketch, "E784", {"start": v(-24.36, -9.38) * mm, "end": v(-23.87, -9.54) * mm});
            skLineSegment(sketch, "E785", {"start": v(-23.87, -9.54) * mm, "end": v(-23.22, -9.54) * mm});
            skLineSegment(sketch, "E786", {"start": v(-23.22, -9.54) * mm, "end": v(-23.05, -9.54) * mm});
            skLineSegment(sketch, "E787", {"start": v(-23.05, -9.54) * mm, "end": v(-22.89, -9.54) * mm});
            skLineSegment(sketch, "E788", {"start": v(-22.89, -9.54) * mm, "end": v(-22.72, -9.54) * mm});
            skLineSegment(sketch, "E789", {"start": v(-22.72, -9.54) * mm, "end": v(-22.56, -9.54) * mm});
            skLineSegment(sketch, "E790", {"start": v(-22.56, -9.54) * mm, "end": v(-22.4, -9.54) * mm});
            skLineSegment(sketch, "E791", {"start": v(-22.4, -9.54) * mm, "end": v(-22.23, -9.54) * mm});
            skLineSegment(sketch, "E792", {"start": v(-22.23, -9.54) * mm, "end": v(-22.07, -9.54) * mm});
            skLineSegment(sketch, "E793", {"start": v(-22.07, -9.54) * mm, "end": v(-21.9, -9.54) * mm});
            skLineSegment(sketch, "E794", {"start": v(-21.9, -9.54) * mm, "end": v(-21.74, -9.54) * mm});
            skLineSegment(sketch, "E795", {"start": v(-21.74, -9.54) * mm, "end": v(-21.58, -9.54) * mm});
            skLineSegment(sketch, "E796", {"start": v(-21.58, -9.54) * mm, "end": v(-21.41, -9.54) * mm});
            skLineSegment(sketch, "E797", {"start": v(-21.41, -9.54) * mm, "end": v(-21.25, -9.54) * mm});
            skLineSegment(sketch, "E798", {"start": v(-21.25, -9.54) * mm, "end": v(-21.08, -9.54) * mm});
            skLineSegment(sketch, "E799", {"start": v(-21.08, -9.54) * mm, "end": v(-20.92, -9.54) * mm});
            skLineSegment(sketch, "E800", {"start": v(-20.92, -9.54) * mm, "end": v(-20.76, -9.54) * mm});
            skLineSegment(sketch, "E801", {"start": v(-20.76, -9.54) * mm, "end": v(-20.6, -9.54) * mm});
            skLineSegment(sketch, "E802", {"start": v(-20.6, -9.54) * mm, "end": v(-20.43, -9.54) * mm});
            skLineSegment(sketch, "E803", {"start": v(-20.43, -9.54) * mm, "end": v(-20.26, -9.54) * mm});
            skLineSegment(sketch, "E804", {"start": v(-20.26, -9.54) * mm, "end": v(-20.1, -9.54) * mm});
            skLineSegment(sketch, "E805", {"start": v(-20.1, -9.54) * mm, "end": v(-19.94, -9.54) * mm});
            skLineSegment(sketch, "E806", {"start": v(-19.94, -9.54) * mm, "end": v(-19.77, -9.54) * mm});
            skLineSegment(sketch, "E807", {"start": v(-19.77, -9.54) * mm, "end": v(-19.6, -9.54) * mm});
            skLineSegment(sketch, "E808", {"start": v(-19.6, -9.54) * mm, "end": v(-19.45, -9.54) * mm});
            skLineSegment(sketch, "E809", {"start": v(-19.45, -9.54) * mm, "end": v(-18.46, -9.38) * mm});
            skLineSegment(sketch, "E810", {"start": v(-18.46, -9.38) * mm, "end": v(-18.3, -9.21) * mm});
            skLineSegment(sketch, "E811", {"start": v(-18.3, -9.21) * mm, "end": v(-18.13, -8.88) * mm});
            skLineSegment(sketch, "E812", {"start": v(-18.13, -8.88) * mm, "end": v(-18.13, -8.23) * mm});
            skLineSegment(sketch, "E813", {"start": v(-18.13, -8.23) * mm, "end": v(-18.13, -8.06) * mm});
            skLineSegment(sketch, "E814", {"start": v(-18.13, -8.06) * mm, "end": v(-18.13, -7.9) * mm});
            skLineSegment(sketch, "E815", {"start": v(-18.13, -7.9) * mm, "end": v(-18.13, -7.74) * mm});
            skLineSegment(sketch, "E816", {"start": v(-18.13, -7.74) * mm, "end": v(-18.3, -6.26) * mm});
            skLineSegment(sketch, "E817", {"start": v(-18.3, -6.26) * mm, "end": v(-18.46, -6.1) * mm});
            skLineSegment(sketch, "E818", {"start": v(-18.46, -6.1) * mm, "end": v(-18.79, -5.93) * mm});
            skLineSegment(sketch, "E819", {"start": v(-18.79, -5.93) * mm, "end": v(-19.45, -5.93) * mm});
            skLineSegment(sketch, "E820", {"start": v(-19.45, -5.93) * mm, "end": v(-19.6, -5.93) * mm});
            skLineSegment(sketch, "E821", {"start": v(-19.6, -5.93) * mm, "end": v(-19.77, -5.93) * mm});
            skLineSegment(sketch, "E822", {"start": v(-19.77, -5.93) * mm, "end": v(-19.94, -5.93) * mm});
            skLineSegment(sketch, "E823", {"start": v(-19.94, -5.93) * mm, "end": v(-20.1, -5.93) * mm});
            skLineSegment(sketch, "E824", {"start": v(-20.1, -5.93) * mm, "end": v(-20.26, -5.93) * mm});
            skLineSegment(sketch, "E825", {"start": v(-20.26, -5.93) * mm, "end": v(-20.43, -5.93) * mm});
            skLineSegment(sketch, "E826", {"start": v(-20.43, -5.93) * mm, "end": v(-20.6, -5.93) * mm});
            skLineSegment(sketch, "E827", {"start": v(-20.6, -5.93) * mm, "end": v(-20.76, -5.93) * mm});
            skLineSegment(sketch, "E828", {"start": v(-20.76, -5.93) * mm, "end": v(-20.92, -5.93) * mm});
            skLineSegment(sketch, "E829", {"start": v(-20.92, -5.93) * mm, "end": v(-21.08, -5.93) * mm});
            skLineSegment(sketch, "E830", {"start": v(-21.08, -5.93) * mm, "end": v(-21.25, -5.93) * mm});
            skLineSegment(sketch, "E831", {"start": v(-21.25, -5.93) * mm, "end": v(-21.41, -5.93) * mm});
            skLineSegment(sketch, "E832", {"start": v(-21.41, -5.93) * mm, "end": v(-21.58, -5.93) * mm});
            skLineSegment(sketch, "E833", {"start": v(-21.58, -5.93) * mm, "end": v(-21.74, -5.93) * mm});
            skLineSegment(sketch, "E834", {"start": v(-21.74, -5.93) * mm, "end": v(-21.9, -5.93) * mm});
            skLineSegment(sketch, "E835", {"start": v(-21.9, -5.93) * mm, "end": v(-23.05, -5.93) * mm});
            skLineSegment(sketch, "E836", {"start": v(-23.05, -5.93) * mm, "end": v(-23.05, -4.95) * mm});
            skLineSegment(sketch, "E837", {"start": v(-23.05, -4.95) * mm, "end": v(-22.4, -4.95) * mm});
            skLineSegment(sketch, "E838", {"start": v(-22.4, -4.95) * mm, "end": v(-22.23, -4.95) * mm});
            skLineSegment(sketch, "E839", {"start": v(-22.23, -4.95) * mm, "end": v(-22.07, -4.95) * mm});
            skLineSegment(sketch, "E840", {"start": v(-22.07, -4.95) * mm, "end": v(-21.9, -4.95) * mm});
            skLineSegment(sketch, "E841", {"start": v(-21.9, -4.95) * mm, "end": v(-21.74, -4.95) * mm});
            skLineSegment(sketch, "E842", {"start": v(-21.74, -4.95) * mm, "end": v(-21.58, -4.95) * mm});
            skLineSegment(sketch, "E843", {"start": v(-21.58, -4.95) * mm, "end": v(-21.41, -4.95) * mm});
            skLineSegment(sketch, "E844", {"start": v(-21.41, -4.95) * mm, "end": v(-21.25, -4.95) * mm});
            skLineSegment(sketch, "E845", {"start": v(-21.25, -4.95) * mm, "end": v(-21.08, -4.95) * mm});
            skLineSegment(sketch, "E846", {"start": v(-21.08, -4.95) * mm, "end": v(-20.92, -4.95) * mm});
            skLineSegment(sketch, "E847", {"start": v(-20.92, -4.95) * mm, "end": v(-20.76, -4.95) * mm});
            skLineSegment(sketch, "E848", {"start": v(-20.76, -4.95) * mm, "end": v(-20.6, -4.95) * mm});
            skLineSegment(sketch, "E849", {"start": v(-20.6, -4.95) * mm, "end": v(-19.6, -4.95) * mm});
            skLineSegment(sketch, "E850", {"start": v(-19.6, -4.95) * mm, "end": v(-19.6, -5.6) * mm});
            skLineSegment(sketch, "E851", {"start": v(-19.6, -5.6) * mm, "end": v(-18.95, -5.6) * mm});
            skLineSegment(sketch, "E852", {"start": v(-18.95, -5.6) * mm, "end": v(-18.13, -5.28) * mm});
            skLineSegment(sketch, "E853", {"start": v(-18.13, -5.28) * mm, "end": v(-18.13, -4.62) * mm});
            skLineSegment(sketch, "E854", {"start": v(-18.13, -4.62) * mm, "end": v(-18.3, -4.13) * mm});
            skLineSegment(sketch, "E855", {"start": v(-18.3, -4.13) * mm, "end": v(-18.79, -3.8) * mm});
            skLineSegment(sketch, "E856", {"start": v(-18.79, -3.8) * mm, "end": v(-19.45, -3.8) * mm});
            skLineSegment(sketch, "E857", {"start": v(-19.45, -3.8) * mm, "end": v(-19.6, -3.8) * mm});
            skLineSegment(sketch, "E858", {"start": v(-19.6, -3.8) * mm, "end": v(-19.77, -3.8) * mm});
            skLineSegment(sketch, "E859", {"start": v(-19.77, -3.8) * mm, "end": v(-19.94, -3.8) * mm});
            skLineSegment(sketch, "E860", {"start": v(-19.94, -3.8) * mm, "end": v(-20.1, -3.8) * mm});
            skLineSegment(sketch, "E861", {"start": v(-20.1, -3.8) * mm, "end": v(-20.26, -3.8) * mm});
            skLineSegment(sketch, "E862", {"start": v(-20.26, -3.8) * mm, "end": v(-20.43, -3.8) * mm});
            skLineSegment(sketch, "E863", {"start": v(-20.43, -3.8) * mm, "end": v(-20.6, -3.8) * mm});
            skLineSegment(sketch, "E864", {"start": v(-20.6, -3.8) * mm, "end": v(-20.76, -3.8) * mm});
            skLineSegment(sketch, "E865", {"start": v(-20.76, -3.8) * mm, "end": v(-20.92, -3.8) * mm});
            skLineSegment(sketch, "E866", {"start": v(-20.92, -3.8) * mm, "end": v(-21.08, -3.8) * mm});
            skLineSegment(sketch, "E867", {"start": v(-21.08, -3.8) * mm, "end": v(-21.25, -3.8) * mm});
            skLineSegment(sketch, "E868", {"start": v(-21.25, -3.8) * mm, "end": v(-21.41, -3.8) * mm});
            skLineSegment(sketch, "E869", {"start": v(-21.41, -3.8) * mm, "end": v(-21.58, -3.8) * mm});
            skLineSegment(sketch, "E870", {"start": v(-21.58, -3.8) * mm, "end": v(-21.74, -3.8) * mm});
            skLineSegment(sketch, "E871", {"start": v(-21.74, -3.8) * mm, "end": v(-21.9, -3.8) * mm});
            skLineSegment(sketch, "E872", {"start": v(-21.9, -3.8) * mm, "end": v(-22.07, -3.8) * mm});
            skLineSegment(sketch, "E873", {"start": v(-22.07, -3.8) * mm, "end": v(-22.23, -3.8) * mm});
            skLineSegment(sketch, "E874", {"start": v(-22.23, -3.8) * mm, "end": v(-22.4, -3.8) * mm});
            skLineSegment(sketch, "E875", {"start": v(-22.4, -3.8) * mm, "end": v(-22.56, -3.8) * mm});
            skLineSegment(sketch, "E876", {"start": v(-22.56, -3.8) * mm, "end": v(-22.72, -3.8) * mm});
            skLineSegment(sketch, "E877", {"start": v(-22.72, -3.8) * mm, "end": v(-22.89, -3.8) * mm});
            skLineSegment(sketch, "E878", {"start": v(-22.89, -3.8) * mm, "end": v(-23.05, -3.8) * mm});
            skLineSegment(sketch, "E879", {"start": v(-23.05, -3.8) * mm, "end": v(-23.22, -3.8) * mm});
            skLineSegment(sketch, "E880", {"start": v(-23.22, -3.8) * mm, "end": v(-23.87, -3.8) * mm});
            skLineSegment(sketch, "E881", {"start": v(-16.5, -4.79) * mm, "end": v(-16.33, -5.28) * mm});
            skLineSegment(sketch, "E882", {"start": v(-16.33, -5.28) * mm, "end": v(-16.33, -5.93) * mm});
            skLineSegment(sketch, "E883", {"start": v(-16.33, -5.93) * mm, "end": v(-16.33, -6.1) * mm});
            skLineSegment(sketch, "E884", {"start": v(-16.33, -6.1) * mm, "end": v(-16.33, -6.26) * mm});
            skLineSegment(sketch, "E885", {"start": v(-16.33, -6.26) * mm, "end": v(-16.33, -6.43) * mm});
            skLineSegment(sketch, "E886", {"start": v(-16.33, -6.43) * mm, "end": v(-16.33, -6.59) * mm});
            skLineSegment(sketch, "E887", {"start": v(-16.33, -6.59) * mm, "end": v(-16.33, -6.75) * mm});
            skLineSegment(sketch, "E888", {"start": v(-16.33, -6.75) * mm, "end": v(-16.33, -6.92) * mm});
            skLineSegment(sketch, "E889", {"start": v(-16.33, -6.92) * mm, "end": v(-16.33, -7.08) * mm});
            skLineSegment(sketch, "E890", {"start": v(-16.33, -7.08) * mm, "end": v(-16.33, -7.24) * mm});
            skLineSegment(sketch, "E891", {"start": v(-16.33, -7.24) * mm, "end": v(-16.33, -7.4) * mm});
            skLineSegment(sketch, "E892", {"start": v(-16.33, -7.4) * mm, "end": v(-16.33, -7.57) * mm});
            skLineSegment(sketch, "E893", {"start": v(-16.33, -7.57) * mm, "end": v(-16.33, -7.74) * mm});
            skLineSegment(sketch, "E894", {"start": v(-16.33, -7.74) * mm, "end": v(-16.33, -7.9) * mm});
            skLineSegment(sketch, "E895", {"start": v(-16.33, -7.9) * mm, "end": v(-16.33, -8.06) * mm});
            skLineSegment(sketch, "E896", {"start": v(-16.33, -8.06) * mm, "end": v(-16.33, -8.23) * mm});
            skLineSegment(sketch, "E897", {"start": v(-16.33, -8.23) * mm, "end": v(-16.33, -8.4) * mm});
            skLineSegment(sketch, "E898", {"start": v(-16.33, -8.4) * mm, "end": v(-16.33, -9.54) * mm});
            skLineSegment(sketch, "E899", {"start": v(-16.33, -9.54) * mm, "end": v(-15.67, -9.54) * mm});
            skLineSegment(sketch, "E900", {"start": v(-15.67, -9.54) * mm, "end": v(-15.51, -9.54) * mm});
            skLineSegment(sketch, "E901", {"start": v(-15.51, -9.54) * mm, "end": v(-15.35, -9.54) * mm});
            skLineSegment(sketch, "E902", {"start": v(-15.35, -9.54) * mm, "end": v(-15.18, -9.54) * mm});
            skLineSegment(sketch, "E903", {"start": v(-15.18, -9.54) * mm, "end": v(-15.02, -9.54) * mm});
            skLineSegment(sketch, "E904", {"start": v(-15.02, -9.54) * mm, "end": v(-14.85, -9.54) * mm});
            skLineSegment(sketch, "E905", {"start": v(-14.85, -9.54) * mm, "end": v(-14.7, -9.54) * mm});
            skLineSegment(sketch, "E906", {"start": v(-14.7, -9.54) * mm, "end": v(-14.53, -9.54) * mm});
            skLineSegment(sketch, "E907", {"start": v(-14.53, -9.54) * mm, "end": v(-14.36, -9.54) * mm});
            skLineSegment(sketch, "E908", {"start": v(-14.36, -9.54) * mm, "end": v(-14.2, -9.54) * mm});
            skLineSegment(sketch, "E909", {"start": v(-14.2, -9.54) * mm, "end": v(-14.04, -9.54) * mm});
            skLineSegment(sketch, "E910", {"start": v(-14.04, -9.54) * mm, "end": v(-13.87, -9.54) * mm});
            skLineSegment(sketch, "E911", {"start": v(-13.87, -9.54) * mm, "end": v(-13.7, -9.54) * mm});
            skLineSegment(sketch, "E912", {"start": v(-13.7, -9.54) * mm, "end": v(-13.54, -9.54) * mm});
            skLineSegment(sketch, "E913", {"start": v(-13.54, -9.54) * mm, "end": v(-13.38, -9.54) * mm});
            skLineSegment(sketch, "E914", {"start": v(-13.38, -9.54) * mm, "end": v(-13.22, -9.54) * mm});
            skLineSegment(sketch, "E915", {"start": v(-13.22, -9.54) * mm, "end": v(-13.05, -9.54) * mm});
            skLineSegment(sketch, "E916", {"start": v(-13.05, -9.54) * mm, "end": v(-12.89, -9.54) * mm});
            skLineSegment(sketch, "E917", {"start": v(-12.89, -9.54) * mm, "end": v(-12.72, -9.54) * mm});
            skLineSegment(sketch, "E918", {"start": v(-12.72, -9.54) * mm, "end": v(-12.56, -9.54) * mm});
            skLineSegment(sketch, "E919", {"start": v(-12.56, -9.54) * mm, "end": v(-12.4, -9.54) * mm});
            skLineSegment(sketch, "E920", {"start": v(-12.4, -9.54) * mm, "end": v(-12.23, -9.54) * mm});
            skLineSegment(sketch, "E921", {"start": v(-12.23, -9.54) * mm, "end": v(-12.07, -9.54) * mm});
            skLineSegment(sketch, "E922", {"start": v(-12.07, -9.54) * mm, "end": v(-11.9, -9.54) * mm});
            skLineSegment(sketch, "E923", {"start": v(-11.9, -9.54) * mm, "end": v(-11.08, -9.54) * mm});
            skLineSegment(sketch, "E924", {"start": v(-11.08, -9.54) * mm, "end": v(-11.08, -8.56) * mm});
            skLineSegment(sketch, "E925", {"start": v(-11.08, -8.56) * mm, "end": v(-11.25, -8.4) * mm});
            skLineSegment(sketch, "E926", {"start": v(-11.25, -8.4) * mm, "end": v(-11.58, -8.4) * mm});
            skLineSegment(sketch, "E927", {"start": v(-11.58, -8.4) * mm, "end": v(-12.23, -8.4) * mm});
            skLineSegment(sketch, "E928", {"start": v(-12.23, -8.4) * mm, "end": v(-12.4, -8.4) * mm});
            skLineSegment(sketch, "E929", {"start": v(-12.4, -8.4) * mm, "end": v(-12.56, -8.4) * mm});
            skLineSegment(sketch, "E930", {"start": v(-12.56, -8.4) * mm, "end": v(-12.72, -8.4) * mm});
            skLineSegment(sketch, "E931", {"start": v(-12.72, -8.4) * mm, "end": v(-12.89, -8.4) * mm});
            skLineSegment(sketch, "E932", {"start": v(-12.89, -8.4) * mm, "end": v(-13.05, -8.4) * mm});
            skLineSegment(sketch, "E933", {"start": v(-13.05, -8.4) * mm, "end": v(-13.22, -8.4) * mm});
            skLineSegment(sketch, "E934", {"start": v(-13.22, -8.4) * mm, "end": v(-13.38, -8.4) * mm});
            skLineSegment(sketch, "E935", {"start": v(-13.38, -8.4) * mm, "end": v(-13.54, -8.4) * mm});
            skLineSegment(sketch, "E936", {"start": v(-13.54, -8.4) * mm, "end": v(-13.7, -8.4) * mm});
            skLineSegment(sketch, "E937", {"start": v(-13.7, -8.4) * mm, "end": v(-13.87, -8.4) * mm});
            skLineSegment(sketch, "E938", {"start": v(-13.87, -8.4) * mm, "end": v(-14.04, -8.4) * mm});
            skLineSegment(sketch, "E939", {"start": v(-14.04, -8.4) * mm, "end": v(-15.02, -8.4) * mm});
            skLineSegment(sketch, "E940", {"start": v(-15.02, -8.4) * mm, "end": v(-15.02, -7.57) * mm});
            skLineSegment(sketch, "E941", {"start": v(-15.02, -7.57) * mm, "end": v(-14.36, -7.57) * mm});
            skLineSegment(sketch, "E942", {"start": v(-14.36, -7.57) * mm, "end": v(-14.2, -7.57) * mm});
            skLineSegment(sketch, "E943", {"start": v(-14.2, -7.57) * mm, "end": v(-14.04, -7.57) * mm});
            skLineSegment(sketch, "E944", {"start": v(-14.04, -7.57) * mm, "end": v(-13.87, -7.57) * mm});
            skLineSegment(sketch, "E945", {"start": v(-13.87, -7.57) * mm, "end": v(-12.72, -7.57) * mm});
            skLineSegment(sketch, "E946", {"start": v(-12.72, -7.57) * mm, "end": v(-12.72, -6.59) * mm});
            skLineSegment(sketch, "E947", {"start": v(-12.72, -6.59) * mm, "end": v(-13.38, -6.59) * mm});
            skLineSegment(sketch, "E948", {"start": v(-13.38, -6.59) * mm, "end": v(-13.54, -6.59) * mm});
            skLineSegment(sketch, "E949", {"start": v(-13.54, -6.59) * mm, "end": v(-13.7, -6.59) * mm});
            skLineSegment(sketch, "E950", {"start": v(-13.7, -6.59) * mm, "end": v(-13.87, -6.59) * mm});
            skLineSegment(sketch, "E951", {"start": v(-13.87, -6.59) * mm, "end": v(-15.02, -6.59) * mm});
            skLineSegment(sketch, "E952", {"start": v(-15.02, -6.59) * mm, "end": v(-15.02, -5.77) * mm});
            skLineSegment(sketch, "E953", {"start": v(-15.02, -5.77) * mm, "end": v(-14.36, -5.77) * mm});
            skLineSegment(sketch, "E954", {"start": v(-14.36, -5.77) * mm, "end": v(-14.2, -5.77) * mm});
            skLineSegment(sketch, "E955", {"start": v(-14.2, -5.77) * mm, "end": v(-14.04, -5.77) * mm});
            skLineSegment(sketch, "E956", {"start": v(-14.04, -5.77) * mm, "end": v(-13.87, -5.77) * mm});
            skLineSegment(sketch, "E957", {"start": v(-13.87, -5.77) * mm, "end": v(-13.7, -5.77) * mm});
            skLineSegment(sketch, "E958", {"start": v(-13.7, -5.77) * mm, "end": v(-13.54, -5.77) * mm});
            skLineSegment(sketch, "E959", {"start": v(-13.54, -5.77) * mm, "end": v(-13.38, -5.77) * mm});
            skLineSegment(sketch, "E960", {"start": v(-13.38, -5.77) * mm, "end": v(-13.22, -5.77) * mm});
            skLineSegment(sketch, "E961", {"start": v(-13.22, -5.77) * mm, "end": v(-13.05, -5.77) * mm});
            skLineSegment(sketch, "E962", {"start": v(-13.05, -5.77) * mm, "end": v(-12.89, -5.77) * mm});
            skLineSegment(sketch, "E963", {"start": v(-12.89, -5.77) * mm, "end": v(-12.72, -5.77) * mm});
            skLineSegment(sketch, "E964", {"start": v(-12.72, -5.77) * mm, "end": v(-12.56, -5.77) * mm});
            skLineSegment(sketch, "E965", {"start": v(-12.56, -5.77) * mm, "end": v(-12.4, -5.77) * mm});
            skLineSegment(sketch, "E966", {"start": v(-12.4, -5.77) * mm, "end": v(-12.23, -5.77) * mm});
            skLineSegment(sketch, "E967", {"start": v(-12.23, -5.77) * mm, "end": v(-12.07, -5.77) * mm});
            skLineSegment(sketch, "E968", {"start": v(-12.07, -5.77) * mm, "end": v(-11.9, -5.77) * mm});
            skLineSegment(sketch, "E969", {"start": v(-11.9, -5.77) * mm, "end": v(-11.25, -5.77) * mm});
            skLineSegment(sketch, "E970", {"start": v(-11.25, -5.77) * mm, "end": v(-11.25, -4.79) * mm});
            skLineSegment(sketch, "E971", {"start": v(-11.25, -4.79) * mm, "end": v(-11.9, -4.79) * mm});
            skLineSegment(sketch, "E972", {"start": v(-11.9, -4.79) * mm, "end": v(-12.07, -4.79) * mm});
            skLineSegment(sketch, "E973", {"start": v(-12.07, -4.79) * mm, "end": v(-12.23, -4.79) * mm});
            skLineSegment(sketch, "E974", {"start": v(-12.23, -4.79) * mm, "end": v(-12.4, -4.79) * mm});
            skLineSegment(sketch, "E975", {"start": v(-12.4, -4.79) * mm, "end": v(-12.56, -4.79) * mm});
            skLineSegment(sketch, "E976", {"start": v(-12.56, -4.79) * mm, "end": v(-12.72, -4.79) * mm});
            skLineSegment(sketch, "E977", {"start": v(-12.72, -4.79) * mm, "end": v(-12.89, -4.79) * mm});
            skLineSegment(sketch, "E978", {"start": v(-12.89, -4.79) * mm, "end": v(-13.05, -4.79) * mm});
            skLineSegment(sketch, "E979", {"start": v(-13.05, -4.79) * mm, "end": v(-13.22, -4.79) * mm});
            skLineSegment(sketch, "E980", {"start": v(-13.22, -4.79) * mm, "end": v(-13.38, -4.79) * mm});
            skLineSegment(sketch, "E981", {"start": v(-13.38, -4.79) * mm, "end": v(-13.54, -4.79) * mm});
            skLineSegment(sketch, "E982", {"start": v(-13.54, -4.79) * mm, "end": v(-13.7, -4.79) * mm});
            skLineSegment(sketch, "E983", {"start": v(-13.7, -4.79) * mm, "end": v(-13.87, -4.79) * mm});
            skLineSegment(sketch, "E984", {"start": v(-13.87, -4.79) * mm, "end": v(-14.04, -4.79) * mm});
            skLineSegment(sketch, "E985", {"start": v(-14.04, -4.79) * mm, "end": v(-14.2, -4.79) * mm});
            skLineSegment(sketch, "E986", {"start": v(-14.2, -4.79) * mm, "end": v(-14.36, -4.79) * mm});
            skLineSegment(sketch, "E987", {"start": v(-14.36, -4.79) * mm, "end": v(-14.53, -4.79) * mm});
            skLineSegment(sketch, "E988", {"start": v(-14.53, -4.79) * mm, "end": v(-14.7, -4.79) * mm});
            skLineSegment(sketch, "E989", {"start": v(-14.7, -4.79) * mm, "end": v(-14.85, -4.79) * mm});
            skLineSegment(sketch, "E990", {"start": v(-14.85, -4.79) * mm, "end": v(-15.02, -4.79) * mm});
            skLineSegment(sketch, "E991", {"start": v(-15.02, -4.79) * mm, "end": v(-15.18, -4.79) * mm});
            skLineSegment(sketch, "E992", {"start": v(-15.18, -4.79) * mm, "end": v(-15.35, -4.79) * mm});
            skLineSegment(sketch, "E993", {"start": v(-15.35, -4.79) * mm, "end": v(-15.51, -4.79) * mm});
            skLineSegment(sketch, "E994", {"start": v(-15.51, -4.79) * mm, "end": v(-15.67, -4.79) * mm});
            skLineSegment(sketch, "E995", {"start": v(-15.67, -4.79) * mm, "end": v(-16.5, -4.79) * mm});
            skLineSegment(sketch, "E996", {"start": v(-10.43, -4.79) * mm, "end": v(-10.1, -5.11) * mm});
            skLineSegment(sketch, "E997", {"start": v(-10.1, -5.11) * mm, "end": v(-10.1, -5.28) * mm});
            skLineSegment(sketch, "E998", {"start": v(-10.1, -5.28) * mm, "end": v(-9.94, -5.28) * mm});
            skLineSegment(sketch, "E999", {"start": v(-9.94, -5.28) * mm, "end": v(-9.94, -5.44) * mm});
            skLineSegment(sketch, "E1000", {"start": v(-9.94, -5.44) * mm, "end": v(-9.77, -5.44) * mm});
            skLineSegment(sketch, "E1001", {"start": v(-9.77, -5.44) * mm, "end": v(-9.77, -5.6) * mm});
            skLineSegment(sketch, "E1002", {"start": v(-9.77, -5.6) * mm, "end": v(-9.6, -5.6) * mm});
            skLineSegment(sketch, "E1003", {"start": v(-9.6, -5.6) * mm, "end": v(-9.6, -5.77) * mm});
            skLineSegment(sketch, "E1004", {"start": v(-9.6, -5.77) * mm, "end": v(-9.45, -5.77) * mm});
            skLineSegment(sketch, "E1005", {"start": v(-9.45, -5.77) * mm, "end": v(-9.45, -5.93) * mm});
            skLineSegment(sketch, "E1006", {"start": v(-9.45, -5.93) * mm, "end": v(-9.28, -5.93) * mm});
            skLineSegment(sketch, "E1007", {"start": v(-9.28, -5.93) * mm, "end": v(-9.28, -6.1) * mm});
            skLineSegment(sketch, "E1008", {"start": v(-9.28, -6.1) * mm, "end": v(-9.12, -6.1) * mm});
            skLineSegment(sketch, "E1009", {"start": v(-9.12, -6.1) * mm, "end": v(-9.12, -6.26) * mm});
            skLineSegment(sketch, "E1010", {"start": v(-9.12, -6.26) * mm, "end": v(-8.95, -6.26) * mm});
            skLineSegment(sketch, "E1011", {"start": v(-8.95, -6.26) * mm, "end": v(-8.95, -6.43) * mm});
            skLineSegment(sketch, "E1012", {"start": v(-8.95, -6.43) * mm, "end": v(-8.79, -6.43) * mm});
            skLineSegment(sketch, "E1013", {"start": v(-8.79, -6.43) * mm, "end": v(-8.79, -6.59) * mm});
            skLineSegment(sketch, "E1014", {"start": v(-8.79, -6.59) * mm, "end": v(-8.63, -6.59) * mm});
            skLineSegment(sketch, "E1015", {"start": v(-8.63, -6.59) * mm, "end": v(-8.63, -6.75) * mm});
            skLineSegment(sketch, "E1016", {"start": v(-8.63, -6.75) * mm, "end": v(-8.46, -6.75) * mm});
            skLineSegment(sketch, "E1017", {"start": v(-8.46, -6.75) * mm, "end": v(-8.46, -6.92) * mm});
            skLineSegment(sketch, "E1018", {"start": v(-8.46, -6.92) * mm, "end": v(-8.3, -6.92) * mm});
            skLineSegment(sketch, "E1019", {"start": v(-8.3, -6.92) * mm, "end": v(-8.3, -7.08) * mm});
            skLineSegment(sketch, "E1020", {"start": v(-8.3, -7.08) * mm, "end": v(-7.8, -7.4) * mm});
            skLineSegment(sketch, "E1021", {"start": v(-7.8, -7.4) * mm, "end": v(-7.8, -8.06) * mm});
            skLineSegment(sketch, "E1022", {"start": v(-7.8, -8.06) * mm, "end": v(-7.8, -8.23) * mm});
            skLineSegment(sketch, "E1023", {"start": v(-7.8, -8.23) * mm, "end": v(-7.8, -8.4) * mm});
            skLineSegment(sketch, "E1024", {"start": v(-7.8, -8.4) * mm, "end": v(-7.8, -8.56) * mm});
            skLineSegment(sketch, "E1025", {"start": v(-7.8, -8.56) * mm, "end": v(-7.8, -9.54) * mm});
            skLineSegment(sketch, "E1026", {"start": v(-7.8, -9.54) * mm, "end": v(-6.5, -9.54) * mm});
            skLineSegment(sketch, "E1027", {"start": v(-6.5, -9.54) * mm, "end": v(-6.5, -8.88) * mm});
            skLineSegment(sketch, "E1028", {"start": v(-6.5, -8.88) * mm, "end": v(-6.5, -8.72) * mm});
            skLineSegment(sketch, "E1029", {"start": v(-6.5, -8.72) * mm, "end": v(-6.5, -8.56) * mm});
            skLineSegment(sketch, "E1030", {"start": v(-6.5, -8.56) * mm, "end": v(-6.5, -8.4) * mm});
            skLineSegment(sketch, "E1031", {"start": v(-6.5, -8.4) * mm, "end": v(-6.5, -7.4) * mm});
            skLineSegment(sketch, "E1032", {"start": v(-6.5, -7.4) * mm, "end": v(-6.17, -7.08) * mm});
            skLineSegment(sketch, "E1033", {"start": v(-6.17, -7.08) * mm, "end": v(-6, -7.08) * mm});
            skLineSegment(sketch, "E1034", {"start": v(-6, -7.08) * mm, "end": v(-6, -6.92) * mm});
            skLineSegment(sketch, "E1035", {"start": v(-6, -6.92) * mm, "end": v(-5.84, -6.92) * mm});
            skLineSegment(sketch, "E1036", {"start": v(-5.84, -6.92) * mm, "end": v(-5.84, -6.75) * mm});
            skLineSegment(sketch, "E1037", {"start": v(-5.84, -6.75) * mm, "end": v(-5.67, -6.75) * mm});
            skLineSegment(sketch, "E1038", {"start": v(-5.67, -6.75) * mm, "end": v(-5.67, -6.59) * mm});
            skLineSegment(sketch, "E1039", {"start": v(-5.67, -6.59) * mm, "end": v(-5.51, -6.59) * mm});
            skLineSegment(sketch, "E1040", {"start": v(-5.51, -6.59) * mm, "end": v(-5.51, -6.43) * mm});
            skLineSegment(sketch, "E1041", {"start": v(-5.51, -6.43) * mm, "end": v(-5.35, -6.43) * mm});
            skLineSegment(sketch, "E1042", {"start": v(-5.35, -6.43) * mm, "end": v(-5.35, -6.26) * mm});
            skLineSegment(sketch, "E1043", {"start": v(-5.35, -6.26) * mm, "end": v(-5.18, -6.26) * mm});
            skLineSegment(sketch, "E1044", {"start": v(-5.18, -6.26) * mm, "end": v(-5.18, -6.1) * mm});
            skLineSegment(sketch, "E1045", {"start": v(-5.18, -6.1) * mm, "end": v(-5.02, -6.1) * mm});
            skLineSegment(sketch, "E1046", {"start": v(-5.02, -6.1) * mm, "end": v(-5.02, -5.93) * mm});
            skLineSegment(sketch, "E1047", {"start": v(-5.02, -5.93) * mm, "end": v(-4.85, -5.93) * mm});
            skLineSegment(sketch, "E1048", {"start": v(-4.85, -5.93) * mm, "end": v(-4.85, -5.77) * mm});
            skLineSegment(sketch, "E1049", {"start": v(-4.85, -5.77) * mm, "end": v(-4.7, -5.77) * mm});
            skLineSegment(sketch, "E1050", {"start": v(-4.7, -5.77) * mm, "end": v(-4.7, -5.6) * mm});
            skLineSegment(sketch, "E1051", {"start": v(-4.7, -5.6) * mm, "end": v(-4.53, -5.6) * mm});
            skLineSegment(sketch, "E1052", {"start": v(-4.53, -5.6) * mm, "end": v(-4.53, -5.44) * mm});
            skLineSegment(sketch, "E1053", {"start": v(-4.53, -5.44) * mm, "end": v(-4.36, -5.44) * mm});
            skLineSegment(sketch, "E1054", {"start": v(-4.36, -5.44) * mm, "end": v(-4.36, -5.28) * mm});
            skLineSegment(sketch, "E1055", {"start": v(-4.36, -5.28) * mm, "end": v(-4.2, -5.28) * mm});
            skLineSegment(sketch, "E1056", {"start": v(-4.2, -5.28) * mm, "end": v(-3.87, -4.79) * mm});
            skLineSegment(sketch, "E1057", {"start": v(-3.87, -4.79) * mm, "end": v(-4.53, -4.79) * mm});
            skLineSegment(sketch, "E1058", {"start": v(-4.53, -4.79) * mm, "end": v(-4.7, -4.79) * mm});
            skLineSegment(sketch, "E1059", {"start": v(-4.7, -4.79) * mm, "end": v(-4.85, -4.79) * mm});
            skLineSegment(sketch, "E1060", {"start": v(-4.85, -4.79) * mm, "end": v(-5.02, -4.79) * mm});
            skLineSegment(sketch, "E1061", {"start": v(-5.02, -4.79) * mm, "end": v(-5.67, -4.79) * mm});
            skLineSegment(sketch, "E1062", {"start": v(-5.67, -4.79) * mm, "end": v(-5.84, -5.28) * mm});
            skLineSegment(sketch, "E1063", {"start": v(-5.84, -5.28) * mm, "end": v(-6.17, -5.6) * mm});
            skLineSegment(sketch, "E1064", {"start": v(-6.17, -5.6) * mm, "end": v(-6.33, -5.6) * mm});
            skLineSegment(sketch, "E1065", {"start": v(-6.33, -5.6) * mm, "end": v(-6.33, -5.77) * mm});
            skLineSegment(sketch, "E1066", {"start": v(-6.33, -5.77) * mm, "end": v(-6.5, -5.77) * mm});
            skLineSegment(sketch, "E1067", {"start": v(-6.5, -5.77) * mm, "end": v(-7.31, -6.26) * mm});
            skLineSegment(sketch, "E1068", {"start": v(-7.31, -6.26) * mm, "end": v(-7.48, -5.77) * mm});
            skLineSegment(sketch, "E1069", {"start": v(-7.48, -5.77) * mm, "end": v(-7.8, -5.44) * mm});
            skLineSegment(sketch, "E1070", {"start": v(-7.8, -5.44) * mm, "end": v(-7.97, -5.44) * mm});
            skLineSegment(sketch, "E1071", {"start": v(-7.97, -5.44) * mm, "end": v(-7.97, -5.28) * mm});
            skLineSegment(sketch, "E1072", {"start": v(-7.97, -5.28) * mm, "end": v(-8.13, -5.28) * mm});
            skLineSegment(sketch, "E1073", {"start": v(-8.13, -5.28) * mm, "end": v(-8.46, -4.79) * mm});
            skLineSegment(sketch, "E1074", {"start": v(-8.46, -4.79) * mm, "end": v(-9.12, -4.79) * mm});
            skLineSegment(sketch, "E1075", {"start": v(-9.12, -4.79) * mm, "end": v(-9.28, -4.79) * mm});
            skLineSegment(sketch, "E1076", {"start": v(-9.28, -4.79) * mm, "end": v(-9.45, -4.79) * mm});
            skLineSegment(sketch, "E1077", {"start": v(-9.45, -4.79) * mm, "end": v(-9.6, -4.79) * mm});
            skLineSegment(sketch, "E1078", {"start": v(-9.6, -4.79) * mm, "end": v(-10.43, -4.79) * mm});
            skLineSegment(sketch, "E1079", {"start": v(-3.22, -4.79) * mm, "end": v(-3.22, -5.44) * mm});
            skLineSegment(sketch, "E1080", {"start": v(-3.22, -5.44) * mm, "end": v(-3.22, -5.6) * mm});
            skLineSegment(sketch, "E1081", {"start": v(-3.22, -5.6) * mm, "end": v(-3.22, -5.77) * mm});
            skLineSegment(sketch, "E1082", {"start": v(-3.22, -5.77) * mm, "end": v(-3.22, -5.93) * mm});
            skLineSegment(sketch, "E1083", {"start": v(-3.22, -5.93) * mm, "end": v(-3.22, -6.1) * mm});
            skLineSegment(sketch, "E1084", {"start": v(-3.22, -6.1) * mm, "end": v(-3.22, -6.26) * mm});
            skLineSegment(sketch, "E1085", {"start": v(-3.22, -6.26) * mm, "end": v(-3.22, -6.43) * mm});
            skLineSegment(sketch, "E1086", {"start": v(-3.22, -6.43) * mm, "end": v(-3.22, -6.59) * mm});
            skLineSegment(sketch, "E1087", {"start": v(-3.22, -6.59) * mm, "end": v(-3.22, -6.75) * mm});
            skLineSegment(sketch, "E1088", {"start": v(-3.22, -6.75) * mm, "end": v(-3.22, -6.92) * mm});
            skLineSegment(sketch, "E1089", {"start": v(-3.22, -6.92) * mm, "end": v(-3.22, -7.08) * mm});
            skLineSegment(sketch, "E1090", {"start": v(-3.22, -7.08) * mm, "end": v(-3.22, -7.24) * mm});
            skLineSegment(sketch, "E1091", {"start": v(-3.22, -7.24) * mm, "end": v(-3.22, -7.4) * mm});
            skLineSegment(sketch, "E1092", {"start": v(-3.22, -7.4) * mm, "end": v(-3.22, -7.57) * mm});
            skLineSegment(sketch, "E1093", {"start": v(-3.22, -7.57) * mm, "end": v(-3.22, -7.74) * mm});
            skLineSegment(sketch, "E1094", {"start": v(-3.22, -7.74) * mm, "end": v(-3.22, -7.9) * mm});
            skLineSegment(sketch, "E1095", {"start": v(-3.22, -7.9) * mm, "end": v(-3.22, -8.06) * mm});
            skLineSegment(sketch, "E1096", {"start": v(-3.22, -8.06) * mm, "end": v(-3.22, -8.23) * mm});
            skLineSegment(sketch, "E1097", {"start": v(-3.22, -8.23) * mm, "end": v(-3.22, -8.4) * mm});
            skLineSegment(sketch, "E1098", {"start": v(-3.22, -8.4) * mm, "end": v(-3.22, -8.56) * mm});
            skLineSegment(sketch, "E1099", {"start": v(-3.22, -8.56) * mm, "end": v(-3.22, -9.54) * mm});
            skLineSegment(sketch, "E1100", {"start": v(-3.22, -9.54) * mm, "end": v(-2.07, -9.54) * mm});
            skLineSegment(sketch, "E1101", {"start": v(-2.07, -9.54) * mm, "end": v(-2.07, -8.88) * mm});
            skLineSegment(sketch, "E1102", {"start": v(-2.07, -8.88) * mm, "end": v(-2.07, -8.72) * mm});
            skLineSegment(sketch, "E1103", {"start": v(-2.07, -8.72) * mm, "end": v(-2.07, -8.56) * mm});
            skLineSegment(sketch, "E1104", {"start": v(-2.07, -8.56) * mm, "end": v(-2.07, -8.4) * mm});
            skLineSegment(sketch, "E1105", {"start": v(-2.07, -8.4) * mm, "end": v(-2.07, -8.23) * mm});
            skLineSegment(sketch, "E1106", {"start": v(-2.07, -8.23) * mm, "end": v(-2.07, -8.06) * mm});
            skLineSegment(sketch, "E1107", {"start": v(-2.07, -8.06) * mm, "end": v(-2.07, -7.9) * mm});
            skLineSegment(sketch, "E1108", {"start": v(-2.07, -7.9) * mm, "end": v(-2.07, -7.74) * mm});
            skLineSegment(sketch, "E1109", {"start": v(-2.07, -7.74) * mm, "end": v(-2.07, -6.92) * mm});
            skLineSegment(sketch, "E1110", {"start": v(-2.07, -6.92) * mm, "end": v(-1.25, -7.57) * mm});
            skLineSegment(sketch, "E1111", {"start": v(-1.25, -7.57) * mm, "end": v(-1.25, -7.9) * mm});
            skLineSegment(sketch, "E1112", {"start": v(-1.25, -7.9) * mm, "end": v(-1.08, -8.06) * mm});
            skLineSegment(sketch, "E1113", {"start": v(-1.08, -8.06) * mm, "end": v(-0.76, -8.23) * mm});
            skLineSegment(sketch, "E1114", {"start": v(-0.76, -8.23) * mm, "end": v(-0.6, -8.4) * mm});
            skLineSegment(sketch, "E1115", {"start": v(-0.6, -8.4) * mm, "end": v(-0.6, -8.72) * mm});
            skLineSegment(sketch, "E1116", {"start": v(-0.6, -8.72) * mm, "end": v(-0.26, -9.05) * mm});
            skLineSegment(sketch, "E1117", {"start": v(-0.26, -9.05) * mm, "end": v(0.23, -9.05) * mm});
            skLineSegment(sketch, "E1118", {"start": v(0.23, -9.05) * mm, "end": v(0.4, -8.88) * mm});
            skLineSegment(sketch, "E1119", {"start": v(0.4, -8.88) * mm, "end": v(0.55, -8.4) * mm});
            skLineSegment(sketch, "E1120", {"start": v(0.55, -8.4) * mm, "end": v(1.05, -8.06) * mm});
            skLineSegment(sketch, "E1121", {"start": v(1.05, -8.06) * mm, "end": v(1.05, -7.74) * mm});
            skLineSegment(sketch, "E1122", {"start": v(1.05, -7.74) * mm, "end": v(1.21, -7.57) * mm});
            skLineSegment(sketch, "E1123", {"start": v(1.21, -7.57) * mm, "end": v(1.87, -6.75) * mm});
            skLineSegment(sketch, "E1124", {"start": v(1.87, -6.75) * mm, "end": v(2.03, -6.75) * mm});
            skLineSegment(sketch, "E1125", {"start": v(2.03, -6.75) * mm, "end": v(2.03, -7.4) * mm});
            skLineSegment(sketch, "E1126", {"start": v(2.03, -7.4) * mm, "end": v(2.03, -7.57) * mm});
            skLineSegment(sketch, "E1127", {"start": v(2.03, -7.57) * mm, "end": v(2.03, -7.74) * mm});
            skLineSegment(sketch, "E1128", {"start": v(2.03, -7.74) * mm, "end": v(2.03, -7.9) * mm});
            skLineSegment(sketch, "E1129", {"start": v(2.03, -7.9) * mm, "end": v(2.03, -8.06) * mm});
            skLineSegment(sketch, "E1130", {"start": v(2.03, -8.06) * mm, "end": v(2.03, -8.23) * mm});
            skLineSegment(sketch, "E1131", {"start": v(2.03, -8.23) * mm, "end": v(2.03, -8.4) * mm});
            skLineSegment(sketch, "E1132", {"start": v(2.03, -8.4) * mm, "end": v(2.03, -8.56) * mm});
            skLineSegment(sketch, "E1133", {"start": v(2.03, -8.56) * mm, "end": v(2.03, -9.54) * mm});
            skLineSegment(sketch, "E1134", {"start": v(2.03, -9.54) * mm, "end": v(3.34, -9.54) * mm});
            skLineSegment(sketch, "E1135", {"start": v(3.34, -9.54) * mm, "end": v(3.34, -8.88) * mm});
            skLineSegment(sketch, "E1136", {"start": v(3.34, -8.88) * mm, "end": v(3.34, -8.72) * mm});
            skLineSegment(sketch, "E1137", {"start": v(3.34, -8.72) * mm, "end": v(3.34, -8.56) * mm});
            skLineSegment(sketch, "E1138", {"start": v(3.34, -8.56) * mm, "end": v(3.34, -8.4) * mm});
            skLineSegment(sketch, "E1139", {"start": v(3.34, -8.4) * mm, "end": v(3.34, -8.23) * mm});
            skLineSegment(sketch, "E1140", {"start": v(3.34, -8.23) * mm, "end": v(3.34, -8.06) * mm});
            skLineSegment(sketch, "E1141", {"start": v(3.34, -8.06) * mm, "end": v(3.34, -7.9) * mm});
            skLineSegment(sketch, "E1142", {"start": v(3.34, -7.9) * mm, "end": v(3.34, -7.74) * mm});
            skLineSegment(sketch, "E1143", {"start": v(3.34, -7.74) * mm, "end": v(3.34, -7.57) * mm});
            skLineSegment(sketch, "E1144", {"start": v(3.34, -7.57) * mm, "end": v(3.34, -7.4) * mm});
            skLineSegment(sketch, "E1145", {"start": v(3.34, -7.4) * mm, "end": v(3.34, -7.24) * mm});
            skLineSegment(sketch, "E1146", {"start": v(3.34, -7.24) * mm, "end": v(3.34, -7.08) * mm});
            skLineSegment(sketch, "E1147", {"start": v(3.34, -7.08) * mm, "end": v(3.34, -6.92) * mm});
            skLineSegment(sketch, "E1148", {"start": v(3.34, -6.92) * mm, "end": v(3.34, -6.75) * mm});
            skLineSegment(sketch, "E1149", {"start": v(3.34, -6.75) * mm, "end": v(3.34, -6.59) * mm});
            skLineSegment(sketch, "E1150", {"start": v(3.34, -6.59) * mm, "end": v(3.34, -6.43) * mm});
            skLineSegment(sketch, "E1151", {"start": v(3.34, -6.43) * mm, "end": v(3.34, -6.26) * mm});
            skLineSegment(sketch, "E1152", {"start": v(3.34, -6.26) * mm, "end": v(3.34, -6.1) * mm});
            skLineSegment(sketch, "E1153", {"start": v(3.34, -6.1) * mm, "end": v(3.34, -5.93) * mm});
            skLineSegment(sketch, "E1154", {"start": v(3.34, -5.93) * mm, "end": v(3.34, -5.77) * mm});
            skLineSegment(sketch, "E1155", {"start": v(3.34, -5.77) * mm, "end": v(3.34, -4.79) * mm});
            skLineSegment(sketch, "E1156", {"start": v(3.34, -4.79) * mm, "end": v(2.03, -4.79) * mm});
            skLineSegment(sketch, "E1157", {"start": v(2.03, -4.79) * mm, "end": v(1.54, -5.44) * mm});
            skLineSegment(sketch, "E1158", {"start": v(1.54, -5.44) * mm, "end": v(1.54, -5.77) * mm});
            skLineSegment(sketch, "E1159", {"start": v(1.54, -5.77) * mm, "end": v(1.37, -5.93) * mm});
            skLineSegment(sketch, "E1160", {"start": v(1.37, -5.93) * mm, "end": v(0.72, -6.43) * mm});
            skLineSegment(sketch, "E1161", {"start": v(0.72, -6.43) * mm, "end": v(0.72, -6.75) * mm});
            skLineSegment(sketch, "E1162", {"start": v(0.72, -6.75) * mm, "end": v(0.55, -6.92) * mm});
            skLineSegment(sketch, "E1163", {"start": v(0.55, -6.92) * mm, "end": v(0.4, -7.08) * mm});
            skLineSegment(sketch, "E1164", {"start": v(0.4, -7.08) * mm, "end": v(0.23, -7.24) * mm});
            skLineSegment(sketch, "E1165", {"start": v(0.23, -7.24) * mm, "end": v(-0.1, -7.24) * mm});
            skLineSegment(sketch, "E1166", {"start": v(-0.1, -7.24) * mm, "end": v(-0.26, -7.08) * mm});
            skLineSegment(sketch, "E1167", {"start": v(-0.26, -7.08) * mm, "end": v(-0.43, -6.92) * mm});
            skLineSegment(sketch, "E1168", {"start": v(-0.43, -6.92) * mm, "end": v(-0.6, -6.75) * mm});
            skLineSegment(sketch, "E1169", {"start": v(-0.6, -6.75) * mm, "end": v(-0.6, -6.43) * mm});
            skLineSegment(sketch, "E1170", {"start": v(-0.6, -6.43) * mm, "end": v(-0.76, -6.26) * mm});
            skLineSegment(sketch, "E1171", {"start": v(-0.76, -6.26) * mm, "end": v(-1.08, -6.1) * mm});
            skLineSegment(sketch, "E1172", {"start": v(-1.08, -6.1) * mm, "end": v(-1.25, -5.93) * mm});
            skLineSegment(sketch, "E1173", {"start": v(-1.25, -5.93) * mm, "end": v(-1.25, -5.6) * mm});
            skLineSegment(sketch, "E1174", {"start": v(-1.25, -5.6) * mm, "end": v(-1.41, -5.44) * mm});
            skLineSegment(sketch, "E1175", {"start": v(-1.41, -5.44) * mm, "end": v(-2.07, -4.79) * mm});
            skLineSegment(sketch, "E1176", {"start": v(-2.07, -4.79) * mm, "end": v(-3.22, -4.79) * mm});
            skLineSegment(sketch, "E1177", {"start": v(5.3, -4.79) * mm, "end": v(4.82, -5.28) * mm});
            skLineSegment(sketch, "E1178", {"start": v(4.82, -5.28) * mm, "end": v(4.82, -5.93) * mm});
            skLineSegment(sketch, "E1179", {"start": v(4.82, -5.93) * mm, "end": v(4.82, -6.1) * mm});
            skLineSegment(sketch, "E1180", {"start": v(4.82, -6.1) * mm, "end": v(4.82, -6.26) * mm});
            skLineSegment(sketch, "E1181", {"start": v(4.82, -6.26) * mm, "end": v(4.82, -6.43) * mm});
            skLineSegment(sketch, "E1182", {"start": v(4.82, -6.43) * mm, "end": v(4.82, -6.59) * mm});
            skLineSegment(sketch, "E1183", {"start": v(4.82, -6.59) * mm, "end": v(4.82, -6.75) * mm});
            skLineSegment(sketch, "E1184", {"start": v(4.82, -6.75) * mm, "end": v(4.82, -6.92) * mm});
            skLineSegment(sketch, "E1185", {"start": v(4.82, -6.92) * mm, "end": v(4.82, -7.08) * mm});
            skLineSegment(sketch, "E1186", {"start": v(4.82, -7.08) * mm, "end": v(4.82, -7.24) * mm});
            skLineSegment(sketch, "E1187", {"start": v(4.82, -7.24) * mm, "end": v(4.82, -7.4) * mm});
            skLineSegment(sketch, "E1188", {"start": v(4.82, -7.4) * mm, "end": v(4.82, -7.57) * mm});
            skLineSegment(sketch, "E1189", {"start": v(4.82, -7.57) * mm, "end": v(4.82, -7.74) * mm});
            skLineSegment(sketch, "E1190", {"start": v(4.82, -7.74) * mm, "end": v(4.82, -7.9) * mm});
            skLineSegment(sketch, "E1191", {"start": v(4.82, -7.9) * mm, "end": v(4.82, -8.06) * mm});
            skLineSegment(sketch, "E1192", {"start": v(4.82, -8.06) * mm, "end": v(4.82, -8.23) * mm});
            skLineSegment(sketch, "E1193", {"start": v(4.82, -8.23) * mm, "end": v(4.82, -8.4) * mm});
            skLineSegment(sketch, "E1194", {"start": v(4.82, -8.4) * mm, "end": v(4.98, -9.38) * mm});
            skLineSegment(sketch, "E1195", {"start": v(4.98, -9.38) * mm, "end": v(5.47, -9.54) * mm});
            skLineSegment(sketch, "E1196", {"start": v(5.47, -9.54) * mm, "end": v(6.13, -9.54) * mm});
            skLineSegment(sketch, "E1197", {"start": v(6.13, -9.54) * mm, "end": v(6.3, -9.54) * mm});
            skLineSegment(sketch, "E1198", {"start": v(6.3, -9.54) * mm, "end": v(6.46, -9.54) * mm});
            skLineSegment(sketch, "E1199", {"start": v(6.46, -9.54) * mm, "end": v(6.62, -9.54) * mm});
            skLineSegment(sketch, "E1200", {"start": v(6.62, -9.54) * mm, "end": v(6.78, -9.54) * mm});
            skLineSegment(sketch, "E1201", {"start": v(6.78, -9.54) * mm, "end": v(6.95, -9.54) * mm});
            skLineSegment(sketch, "E1202", {"start": v(6.95, -9.54) * mm, "end": v(7.11, -9.54) * mm});
            skLineSegment(sketch, "E1203", {"start": v(7.11, -9.54) * mm, "end": v(7.28, -9.54) * mm});
            skLineSegment(sketch, "E1204", {"start": v(7.28, -9.54) * mm, "end": v(7.44, -9.54) * mm});
            skLineSegment(sketch, "E1205", {"start": v(7.44, -9.54) * mm, "end": v(7.6, -9.54) * mm});
            skLineSegment(sketch, "E1206", {"start": v(7.6, -9.54) * mm, "end": v(7.77, -9.54) * mm});
            skLineSegment(sketch, "E1207", {"start": v(7.77, -9.54) * mm, "end": v(7.93, -9.54) * mm});
            skLineSegment(sketch, "E1208", {"start": v(7.93, -9.54) * mm, "end": v(8.1, -9.54) * mm});
            skLineSegment(sketch, "E1209", {"start": v(8.1, -9.54) * mm, "end": v(8.26, -9.54) * mm});
            skLineSegment(sketch, "E1210", {"start": v(8.26, -9.54) * mm, "end": v(8.42, -9.54) * mm});
            skLineSegment(sketch, "E1211", {"start": v(8.42, -9.54) * mm, "end": v(8.59, -9.54) * mm});
            skLineSegment(sketch, "E1212", {"start": v(8.59, -9.54) * mm, "end": v(8.75, -9.54) * mm});
            skLineSegment(sketch, "E1213", {"start": v(8.75, -9.54) * mm, "end": v(8.92, -9.54) * mm});
            skLineSegment(sketch, "E1214", {"start": v(8.92, -9.54) * mm, "end": v(9.08, -9.54) * mm});
            skLineSegment(sketch, "E1215", {"start": v(9.08, -9.54) * mm, "end": v(9.24, -9.54) * mm});
            skLineSegment(sketch, "E1216", {"start": v(9.24, -9.54) * mm, "end": v(9.4, -9.54) * mm});
            skLineSegment(sketch, "E1217", {"start": v(9.4, -9.54) * mm, "end": v(9.57, -9.54) * mm});
            skLineSegment(sketch, "E1218", {"start": v(9.57, -9.54) * mm, "end": v(9.74, -9.54) * mm});
            skLineSegment(sketch, "E1219", {"start": v(9.74, -9.54) * mm, "end": v(9.9, -9.54) * mm});
            skLineSegment(sketch, "E1220", {"start": v(9.9, -9.54) * mm, "end": v(10.55, -9.54) * mm});
            skLineSegment(sketch, "E1221", {"start": v(10.55, -9.54) * mm, "end": v(11.05, -8.88) * mm});
            skLineSegment(sketch, "E1222", {"start": v(11.05, -8.88) * mm, "end": v(11.05, -8.23) * mm});
            skLineSegment(sketch, "E1223", {"start": v(11.05, -8.23) * mm, "end": v(11.05, -8.06) * mm});
            skLineSegment(sketch, "E1224", {"start": v(11.05, -8.06) * mm, "end": v(11.05, -7.9) * mm});
            skLineSegment(sketch, "E1225", {"start": v(11.05, -7.9) * mm, "end": v(11.05, -7.74) * mm});
            skLineSegment(sketch, "E1226", {"start": v(11.05, -7.74) * mm, "end": v(11.05, -7.57) * mm});
            skLineSegment(sketch, "E1227", {"start": v(11.05, -7.57) * mm, "end": v(11.05, -7.4) * mm});
            skLineSegment(sketch, "E1228", {"start": v(11.05, -7.4) * mm, "end": v(11.05, -7.24) * mm});
            skLineSegment(sketch, "E1229", {"start": v(11.05, -7.24) * mm, "end": v(11.05, -7.08) * mm});
            skLineSegment(sketch, "E1230", {"start": v(11.05, -7.08) * mm, "end": v(11.05, -6.92) * mm});
            skLineSegment(sketch, "E1231", {"start": v(11.05, -6.92) * mm, "end": v(11.05, -6.75) * mm});
            skLineSegment(sketch, "E1232", {"start": v(11.05, -6.75) * mm, "end": v(11.05, -6.59) * mm});
            skLineSegment(sketch, "E1233", {"start": v(11.05, -6.59) * mm, "end": v(11.05, -6.43) * mm});
            skLineSegment(sketch, "E1234", {"start": v(11.05, -6.43) * mm, "end": v(11.05, -5.44) * mm});
            skLineSegment(sketch, "E1235", {"start": v(11.05, -5.44) * mm, "end": v(10.55, -4.79) * mm});
            skLineSegment(sketch, "E1236", {"start": v(10.55, -4.79) * mm, "end": v(9.9, -4.79) * mm});
            skLineSegment(sketch, "E1237", {"start": v(9.9, -4.79) * mm, "end": v(9.74, -4.79) * mm});
            skLineSegment(sketch, "E1238", {"start": v(9.74, -4.79) * mm, "end": v(9.57, -4.79) * mm});
            skLineSegment(sketch, "E1239", {"start": v(9.57, -4.79) * mm, "end": v(9.4, -4.79) * mm});
            skLineSegment(sketch, "E1240", {"start": v(9.4, -4.79) * mm, "end": v(9.24, -4.79) * mm});
            skLineSegment(sketch, "E1241", {"start": v(9.24, -4.79) * mm, "end": v(9.08, -4.79) * mm});
            skLineSegment(sketch, "E1242", {"start": v(9.08, -4.79) * mm, "end": v(8.92, -4.79) * mm});
            skLineSegment(sketch, "E1243", {"start": v(8.92, -4.79) * mm, "end": v(8.75, -4.79) * mm});
            skLineSegment(sketch, "E1244", {"start": v(8.75, -4.79) * mm, "end": v(8.59, -4.79) * mm});
            skLineSegment(sketch, "E1245", {"start": v(8.59, -4.79) * mm, "end": v(8.42, -4.79) * mm});
            skLineSegment(sketch, "E1246", {"start": v(8.42, -4.79) * mm, "end": v(8.26, -4.79) * mm});
            skLineSegment(sketch, "E1247", {"start": v(8.26, -4.79) * mm, "end": v(8.1, -4.79) * mm});
            skLineSegment(sketch, "E1248", {"start": v(8.1, -4.79) * mm, "end": v(7.93, -4.79) * mm});
            skLineSegment(sketch, "E1249", {"start": v(7.93, -4.79) * mm, "end": v(7.77, -4.79) * mm});
            skLineSegment(sketch, "E1250", {"start": v(7.77, -4.79) * mm, "end": v(7.6, -4.79) * mm});
            skLineSegment(sketch, "E1251", {"start": v(7.6, -4.79) * mm, "end": v(7.44, -4.79) * mm});
            skLineSegment(sketch, "E1252", {"start": v(7.44, -4.79) * mm, "end": v(7.28, -4.79) * mm});
            skLineSegment(sketch, "E1253", {"start": v(7.28, -4.79) * mm, "end": v(7.11, -4.79) * mm});
            skLineSegment(sketch, "E1254", {"start": v(7.11, -4.79) * mm, "end": v(6.95, -4.79) * mm});
            skLineSegment(sketch, "E1255", {"start": v(6.95, -4.79) * mm, "end": v(6.78, -4.79) * mm});
            skLineSegment(sketch, "E1256", {"start": v(6.78, -4.79) * mm, "end": v(6.62, -4.79) * mm});
            skLineSegment(sketch, "E1257", {"start": v(6.62, -4.79) * mm, "end": v(6.46, -4.79) * mm});
            skLineSegment(sketch, "E1258", {"start": v(6.46, -4.79) * mm, "end": v(6.3, -4.79) * mm});
            skLineSegment(sketch, "E1259", {"start": v(6.3, -4.79) * mm, "end": v(6.13, -4.79) * mm});
            skLineSegment(sketch, "E1260", {"start": v(6.13, -4.79) * mm, "end": v(5.3, -4.79) * mm});
            skLineSegment(sketch, "E1261", {"start": v(12.69, -4.79) * mm, "end": v(12.69, -5.44) * mm});
            skLineSegment(sketch, "E1262", {"start": v(12.69, -5.44) * mm, "end": v(12.69, -5.6) * mm});
            skLineSegment(sketch, "E1263", {"start": v(12.69, -5.6) * mm, "end": v(12.69, -5.77) * mm});
            skLineSegment(sketch, "E1264", {"start": v(12.69, -5.77) * mm, "end": v(12.69, -5.93) * mm});
            skLineSegment(sketch, "E1265", {"start": v(12.69, -5.93) * mm, "end": v(12.69, -6.1) * mm});
            skLineSegment(sketch, "E1266", {"start": v(12.69, -6.1) * mm, "end": v(12.69, -6.26) * mm});
            skLineSegment(sketch, "E1267", {"start": v(12.69, -6.26) * mm, "end": v(12.69, -6.43) * mm});
            skLineSegment(sketch, "E1268", {"start": v(12.69, -6.43) * mm, "end": v(12.69, -6.59) * mm});
            skLineSegment(sketch, "E1269", {"start": v(12.69, -6.59) * mm, "end": v(12.69, -6.75) * mm});
            skLineSegment(sketch, "E1270", {"start": v(12.69, -6.75) * mm, "end": v(12.69, -6.92) * mm});
            skLineSegment(sketch, "E1271", {"start": v(12.69, -6.92) * mm, "end": v(12.69, -7.08) * mm});
            skLineSegment(sketch, "E1272", {"start": v(12.69, -7.08) * mm, "end": v(12.69, -7.24) * mm});
            skLineSegment(sketch, "E1273", {"start": v(12.69, -7.24) * mm, "end": v(12.69, -7.4) * mm});
            skLineSegment(sketch, "E1274", {"start": v(12.69, -7.4) * mm, "end": v(12.69, -7.57) * mm});
            skLineSegment(sketch, "E1275", {"start": v(12.69, -7.57) * mm, "end": v(12.69, -7.74) * mm});
            skLineSegment(sketch, "E1276", {"start": v(12.69, -7.74) * mm, "end": v(12.69, -7.9) * mm});
            skLineSegment(sketch, "E1277", {"start": v(12.69, -7.9) * mm, "end": v(12.69, -9.05) * mm});
            skLineSegment(sketch, "E1278", {"start": v(12.69, -9.05) * mm, "end": v(13.18, -9.54) * mm});
            skLineSegment(sketch, "E1279", {"start": v(13.18, -9.54) * mm, "end": v(13.83, -9.54) * mm});
            skLineSegment(sketch, "E1280", {"start": v(13.83, -9.54) * mm, "end": v(14, -9.54) * mm});
            skLineSegment(sketch, "E1281", {"start": v(14, -9.54) * mm, "end": v(14.16, -9.54) * mm});
            skLineSegment(sketch, "E1282", {"start": v(14.16, -9.54) * mm, "end": v(14.33, -9.54) * mm});
            skLineSegment(sketch, "E1283", {"start": v(14.33, -9.54) * mm, "end": v(14.49, -9.54) * mm});
            skLineSegment(sketch, "E1284", {"start": v(14.49, -9.54) * mm, "end": v(14.65, -9.54) * mm});
            skLineSegment(sketch, "E1285", {"start": v(14.65, -9.54) * mm, "end": v(14.82, -9.54) * mm});
            skLineSegment(sketch, "E1286", {"start": v(14.82, -9.54) * mm, "end": v(14.98, -9.54) * mm});
            skLineSegment(sketch, "E1287", {"start": v(14.98, -9.54) * mm, "end": v(15.15, -9.54) * mm});
            skLineSegment(sketch, "E1288", {"start": v(15.15, -9.54) * mm, "end": v(15.3, -9.54) * mm});
            skLineSegment(sketch, "E1289", {"start": v(15.3, -9.54) * mm, "end": v(15.47, -9.54) * mm});
            skLineSegment(sketch, "E1290", {"start": v(15.47, -9.54) * mm, "end": v(15.64, -9.54) * mm});
            skLineSegment(sketch, "E1291", {"start": v(15.64, -9.54) * mm, "end": v(15.8, -9.54) * mm});
            skLineSegment(sketch, "E1292", {"start": v(15.8, -9.54) * mm, "end": v(15.96, -9.54) * mm});
            skLineSegment(sketch, "E1293", {"start": v(15.96, -9.54) * mm, "end": v(16.13, -9.54) * mm});
            skLineSegment(sketch, "E1294", {"start": v(16.13, -9.54) * mm, "end": v(16.3, -9.54) * mm});
            skLineSegment(sketch, "E1295", {"start": v(16.3, -9.54) * mm, "end": v(16.46, -9.54) * mm});
            skLineSegment(sketch, "E1296", {"start": v(16.46, -9.54) * mm, "end": v(16.62, -9.54) * mm});
            skLineSegment(sketch, "E1297", {"start": v(16.62, -9.54) * mm, "end": v(16.78, -9.54) * mm});
            skLineSegment(sketch, "E1298", {"start": v(16.78, -9.54) * mm, "end": v(16.95, -9.54) * mm});
            skLineSegment(sketch, "E1299", {"start": v(16.95, -9.54) * mm, "end": v(17.93, -9.54) * mm});
            skLineSegment(sketch, "E1300", {"start": v(17.93, -9.54) * mm, "end": v(18.42, -8.88) * mm});
            skLineSegment(sketch, "E1301", {"start": v(18.42, -8.88) * mm, "end": v(18.42, -8.23) * mm});
            skLineSegment(sketch, "E1302", {"start": v(18.42, -8.23) * mm, "end": v(18.42, -8.06) * mm});
            skLineSegment(sketch, "E1303", {"start": v(18.42, -8.06) * mm, "end": v(18.42, -7.9) * mm});
            skLineSegment(sketch, "E1304", {"start": v(18.42, -7.9) * mm, "end": v(18.42, -7.74) * mm});
            skLineSegment(sketch, "E1305", {"start": v(18.42, -7.74) * mm, "end": v(18.42, -7.57) * mm});
            skLineSegment(sketch, "E1306", {"start": v(18.42, -7.57) * mm, "end": v(18.42, -7.4) * mm});
            skLineSegment(sketch, "E1307", {"start": v(18.42, -7.4) * mm, "end": v(18.42, -7.24) * mm});
            skLineSegment(sketch, "E1308", {"start": v(18.42, -7.24) * mm, "end": v(18.42, -7.08) * mm});
            skLineSegment(sketch, "E1309", {"start": v(18.42, -7.08) * mm, "end": v(18.42, -6.92) * mm});
            skLineSegment(sketch, "E1310", {"start": v(18.42, -6.92) * mm, "end": v(18.42, -6.75) * mm});
            skLineSegment(sketch, "E1311", {"start": v(18.42, -6.75) * mm, "end": v(18.42, -6.59) * mm});
            skLineSegment(sketch, "E1312", {"start": v(18.42, -6.59) * mm, "end": v(18.42, -6.43) * mm});
            skLineSegment(sketch, "E1313", {"start": v(18.42, -6.43) * mm, "end": v(18.42, -6.26) * mm});
            skLineSegment(sketch, "E1314", {"start": v(18.42, -6.26) * mm, "end": v(18.42, -6.1) * mm});
            skLineSegment(sketch, "E1315", {"start": v(18.42, -6.1) * mm, "end": v(18.42, -5.93) * mm});
            skLineSegment(sketch, "E1316", {"start": v(18.42, -5.93) * mm, "end": v(18.42, -5.77) * mm});
            skLineSegment(sketch, "E1317", {"start": v(18.42, -5.77) * mm, "end": v(18.42, -4.79) * mm});
            skLineSegment(sketch, "E1318", {"start": v(18.42, -4.79) * mm, "end": v(16.95, -4.79) * mm});
            skLineSegment(sketch, "E1319", {"start": v(16.95, -4.79) * mm, "end": v(16.95, -5.44) * mm});
            skLineSegment(sketch, "E1320", {"start": v(16.95, -5.44) * mm, "end": v(16.95, -5.6) * mm});
            skLineSegment(sketch, "E1321", {"start": v(16.95, -5.6) * mm, "end": v(16.95, -5.77) * mm});
            skLineSegment(sketch, "E1322", {"start": v(16.95, -5.77) * mm, "end": v(16.95, -5.93) * mm});
            skLineSegment(sketch, "E1323", {"start": v(16.95, -5.93) * mm, "end": v(16.95, -6.1) * mm});
            skLineSegment(sketch, "E1324", {"start": v(16.95, -6.1) * mm, "end": v(16.95, -6.26) * mm});
            skLineSegment(sketch, "E1325", {"start": v(16.95, -6.26) * mm, "end": v(16.95, -6.43) * mm});
            skLineSegment(sketch, "E1326", {"start": v(16.95, -6.43) * mm, "end": v(16.95, -6.59) * mm});
            skLineSegment(sketch, "E1327", {"start": v(16.95, -6.59) * mm, "end": v(16.95, -6.75) * mm});
            skLineSegment(sketch, "E1328", {"start": v(16.95, -6.75) * mm, "end": v(16.95, -6.92) * mm});
            skLineSegment(sketch, "E1329", {"start": v(16.95, -6.92) * mm, "end": v(16.95, -7.08) * mm});
            skLineSegment(sketch, "E1330", {"start": v(16.95, -7.08) * mm, "end": v(16.95, -7.24) * mm});
            skLineSegment(sketch, "E1331", {"start": v(16.95, -7.24) * mm, "end": v(16.95, -8.4) * mm});
            skLineSegment(sketch, "E1332", {"start": v(16.95, -8.4) * mm, "end": v(16.3, -8.4) * mm});
            skLineSegment(sketch, "E1333", {"start": v(16.3, -8.4) * mm, "end": v(16.13, -8.4) * mm});
            skLineSegment(sketch, "E1334", {"start": v(16.13, -8.4) * mm, "end": v(15.96, -8.4) * mm});
            skLineSegment(sketch, "E1335", {"start": v(15.96, -8.4) * mm, "end": v(15.8, -8.4) * mm});
            skLineSegment(sketch, "E1336", {"start": v(15.8, -8.4) * mm, "end": v(15.64, -8.4) * mm});
            skLineSegment(sketch, "E1337", {"start": v(15.64, -8.4) * mm, "end": v(15.47, -8.4) * mm});
            skLineSegment(sketch, "E1338", {"start": v(15.47, -8.4) * mm, "end": v(15.3, -8.4) * mm});
            skLineSegment(sketch, "E1339", {"start": v(15.3, -8.4) * mm, "end": v(15.15, -8.4) * mm});
            skLineSegment(sketch, "E1340", {"start": v(15.15, -8.4) * mm, "end": v(14, -8.4) * mm});
            skLineSegment(sketch, "E1341", {"start": v(14, -8.4) * mm, "end": v(14.16, -7.9) * mm});
            skLineSegment(sketch, "E1342", {"start": v(14.16, -7.9) * mm, "end": v(14.16, -7.24) * mm});
            skLineSegment(sketch, "E1343", {"start": v(14.16, -7.24) * mm, "end": v(14.16, -7.08) * mm});
            skLineSegment(sketch, "E1344", {"start": v(14.16, -7.08) * mm, "end": v(14.16, -6.92) * mm});
            skLineSegment(sketch, "E1345", {"start": v(14.16, -6.92) * mm, "end": v(14.16, -6.75) * mm});
            skLineSegment(sketch, "E1346", {"start": v(14.16, -6.75) * mm, "end": v(14.16, -6.59) * mm});
            skLineSegment(sketch, "E1347", {"start": v(14.16, -6.59) * mm, "end": v(14.16, -6.43) * mm});
            skLineSegment(sketch, "E1348", {"start": v(14.16, -6.43) * mm, "end": v(14.16, -6.26) * mm});
            skLineSegment(sketch, "E1349", {"start": v(14.16, -6.26) * mm, "end": v(14.16, -6.1) * mm});
            skLineSegment(sketch, "E1350", {"start": v(14.16, -6.1) * mm, "end": v(14.16, -4.95) * mm});
            skLineSegment(sketch, "E1351", {"start": v(14.16, -4.95) * mm, "end": v(14, -4.79) * mm});
            skLineSegment(sketch, "E1352", {"start": v(14, -4.79) * mm, "end": v(13.67, -4.79) * mm});
            skLineSegment(sketch, "E1353", {"start": v(13.67, -4.79) * mm, "end": v(12.69, -4.79) * mm});
            skLineSegment(sketch, "E1354", {"start": v(20.06, -4.79) * mm, "end": v(20.06, -5.44) * mm});
            skLineSegment(sketch, "E1355", {"start": v(20.06, -5.44) * mm, "end": v(20.06, -5.6) * mm});
            skLineSegment(sketch, "E1356", {"start": v(20.06, -5.6) * mm, "end": v(20.06, -5.77) * mm});
            skLineSegment(sketch, "E1357", {"start": v(20.06, -5.77) * mm, "end": v(20.06, -5.93) * mm});
            skLineSegment(sketch, "E1358", {"start": v(20.06, -5.93) * mm, "end": v(20.06, -6.1) * mm});
            skLineSegment(sketch, "E1359", {"start": v(20.06, -6.1) * mm, "end": v(20.06, -6.26) * mm});
            skLineSegment(sketch, "E1360", {"start": v(20.06, -6.26) * mm, "end": v(20.06, -6.43) * mm});
            skLineSegment(sketch, "E1361", {"start": v(20.06, -6.43) * mm, "end": v(20.06, -6.59) * mm});
            skLineSegment(sketch, "E1362", {"start": v(20.06, -6.59) * mm, "end": v(20.06, -6.75) * mm});
            skLineSegment(sketch, "E1363", {"start": v(20.06, -6.75) * mm, "end": v(20.06, -6.92) * mm});
            skLineSegment(sketch, "E1364", {"start": v(20.06, -6.92) * mm, "end": v(20.06, -7.08) * mm});
            skLineSegment(sketch, "E1365", {"start": v(20.06, -7.08) * mm, "end": v(20.06, -7.24) * mm});
            skLineSegment(sketch, "E1366", {"start": v(20.06, -7.24) * mm, "end": v(20.06, -7.4) * mm});
            skLineSegment(sketch, "E1367", {"start": v(20.06, -7.4) * mm, "end": v(20.06, -7.57) * mm});
            skLineSegment(sketch, "E1368", {"start": v(20.06, -7.57) * mm, "end": v(20.06, -7.74) * mm});
            skLineSegment(sketch, "E1369", {"start": v(20.06, -7.74) * mm, "end": v(20.06, -7.9) * mm});
            skLineSegment(sketch, "E1370", {"start": v(20.06, -7.9) * mm, "end": v(20.06, -8.06) * mm});
            skLineSegment(sketch, "E1371", {"start": v(20.06, -8.06) * mm, "end": v(20.06, -8.23) * mm});
            skLineSegment(sketch, "E1372", {"start": v(20.06, -8.23) * mm, "end": v(20.06, -8.4) * mm});
            skLineSegment(sketch, "E1373", {"start": v(20.06, -8.4) * mm, "end": v(20.06, -8.56) * mm});
            skLineSegment(sketch, "E1374", {"start": v(20.06, -8.56) * mm, "end": v(20.06, -9.54) * mm});
            skLineSegment(sketch, "E1375", {"start": v(20.06, -9.54) * mm, "end": v(21.37, -9.54) * mm});
            skLineSegment(sketch, "E1376", {"start": v(21.37, -9.54) * mm, "end": v(21.37, -7.9) * mm});
            skLineSegment(sketch, "E1377", {"start": v(21.37, -7.9) * mm, "end": v(22.52, -7.9) * mm});
            skLineSegment(sketch, "E1378", {"start": v(22.52, -7.9) * mm, "end": v(22.85, -8.23) * mm});
            skLineSegment(sketch, "E1379", {"start": v(22.85, -8.23) * mm, "end": v(22.85, -8.4) * mm});
            skLineSegment(sketch, "E1380", {"start": v(22.85, -8.4) * mm, "end": v(23.01, -8.4) * mm});
            skLineSegment(sketch, "E1381", {"start": v(23.01, -8.4) * mm, "end": v(23.01, -8.56) * mm});
            skLineSegment(sketch, "E1382", {"start": v(23.01, -8.56) * mm, "end": v(23.18, -8.56) * mm});
            skLineSegment(sketch, "E1383", {"start": v(23.18, -8.56) * mm, "end": v(23.18, -8.72) * mm});
            skLineSegment(sketch, "E1384", {"start": v(23.18, -8.72) * mm, "end": v(23.34, -8.72) * mm});
            skLineSegment(sketch, "E1385", {"start": v(23.34, -8.72) * mm, "end": v(23.34, -8.88) * mm});
            skLineSegment(sketch, "E1386", {"start": v(23.34, -8.88) * mm, "end": v(24.16, -9.54) * mm});
            skLineSegment(sketch, "E1387", {"start": v(24.16, -9.54) * mm, "end": v(24.82, -9.54) * mm});
            skLineSegment(sketch, "E1388", {"start": v(24.82, -9.54) * mm, "end": v(24.98, -9.54) * mm});
            skLineSegment(sketch, "E1389", {"start": v(24.98, -9.54) * mm, "end": v(25.15, -9.54) * mm});
            skLineSegment(sketch, "E1390", {"start": v(25.15, -9.54) * mm, "end": v(25.3, -9.54) * mm});
            skLineSegment(sketch, "E1391", {"start": v(25.3, -9.54) * mm, "end": v(26.13, -9.54) * mm});
            skLineSegment(sketch, "E1392", {"start": v(26.13, -9.54) * mm, "end": v(25.8, -9.05) * mm});
            skLineSegment(sketch, "E1393", {"start": v(25.8, -9.05) * mm, "end": v(25.47, -9.05) * mm});
            skLineSegment(sketch, "E1394", {"start": v(25.47, -9.05) * mm, "end": v(25.15, -8.56) * mm});
            skLineSegment(sketch, "E1395", {"start": v(25.15, -8.56) * mm, "end": v(24.82, -8.56) * mm});
            skLineSegment(sketch, "E1396", {"start": v(24.82, -8.56) * mm, "end": v(24.33, -7.9) * mm});
            skLineSegment(sketch, "E1397", {"start": v(24.33, -7.9) * mm, "end": v(25.47, -7.4) * mm});
            skLineSegment(sketch, "E1398", {"start": v(25.47, -7.4) * mm, "end": v(25.64, -6.92) * mm});
            skLineSegment(sketch, "E1399", {"start": v(25.64, -6.92) * mm, "end": v(25.47, -6.1) * mm});
            skLineSegment(sketch, "E1400", {"start": v(25.47, -6.1) * mm, "end": v(25.64, -5.6) * mm});
            skLineSegment(sketch, "E1401", {"start": v(25.64, -5.6) * mm, "end": v(25.47, -5.11) * mm});
            skLineSegment(sketch, "E1402", {"start": v(25.47, -5.11) * mm, "end": v(25.15, -4.79) * mm});
            skLineSegment(sketch, "E1403", {"start": v(25.15, -4.79) * mm, "end": v(24.49, -4.79) * mm});
            skLineSegment(sketch, "E1404", {"start": v(24.49, -4.79) * mm, "end": v(24.33, -4.79) * mm});
            skLineSegment(sketch, "E1405", {"start": v(24.33, -4.79) * mm, "end": v(24.16, -4.79) * mm});
            skLineSegment(sketch, "E1406", {"start": v(24.16, -4.79) * mm, "end": v(24, -4.79) * mm});
            skLineSegment(sketch, "E1407", {"start": v(24, -4.79) * mm, "end": v(23.83, -4.79) * mm});
            skLineSegment(sketch, "E1408", {"start": v(23.83, -4.79) * mm, "end": v(23.67, -4.79) * mm});
            skLineSegment(sketch, "E1409", {"start": v(23.67, -4.79) * mm, "end": v(23.5, -4.79) * mm});
            skLineSegment(sketch, "E1410", {"start": v(23.5, -4.79) * mm, "end": v(23.34, -4.79) * mm});
            skLineSegment(sketch, "E1411", {"start": v(23.34, -4.79) * mm, "end": v(23.18, -4.79) * mm});
            skLineSegment(sketch, "E1412", {"start": v(23.18, -4.79) * mm, "end": v(23.01, -4.79) * mm});
            skLineSegment(sketch, "E1413", {"start": v(23.01, -4.79) * mm, "end": v(22.85, -4.79) * mm});
            skLineSegment(sketch, "E1414", {"start": v(22.85, -4.79) * mm, "end": v(22.69, -4.79) * mm});
            skLineSegment(sketch, "E1415", {"start": v(22.69, -4.79) * mm, "end": v(22.52, -4.79) * mm});
            skLineSegment(sketch, "E1416", {"start": v(22.52, -4.79) * mm, "end": v(22.36, -4.79) * mm});
            skLineSegment(sketch, "E1417", {"start": v(22.36, -4.79) * mm, "end": v(22.2, -4.79) * mm});
            skLineSegment(sketch, "E1418", {"start": v(22.2, -4.79) * mm, "end": v(22.03, -4.79) * mm});
            skLineSegment(sketch, "E1419", {"start": v(22.03, -4.79) * mm, "end": v(21.87, -4.79) * mm});
            skLineSegment(sketch, "E1420", {"start": v(21.87, -4.79) * mm, "end": v(21.7, -4.79) * mm});
            skLineSegment(sketch, "E1421", {"start": v(21.7, -4.79) * mm, "end": v(21.54, -4.79) * mm});
            skLineSegment(sketch, "E1422", {"start": v(21.54, -4.79) * mm, "end": v(21.37, -4.79) * mm});
            skLineSegment(sketch, "E1423", {"start": v(21.37, -4.79) * mm, "end": v(21.21, -4.79) * mm});
            skLineSegment(sketch, "E1424", {"start": v(21.21, -4.79) * mm, "end": v(21.05, -4.79) * mm});
            skLineSegment(sketch, "E1425", {"start": v(21.05, -4.79) * mm, "end": v(20.88, -4.79) * mm});
            skLineSegment(sketch, "E1426", {"start": v(20.88, -4.79) * mm, "end": v(20.72, -4.79) * mm});
            skLineSegment(sketch, "E1427", {"start": v(20.72, -4.79) * mm, "end": v(20.06, -4.79) * mm});
            skLineSegment(sketch, "E1428", {"start": v(6.13, -5.93) * mm, "end": v(6.13, -6.59) * mm});
            skLineSegment(sketch, "E1429", {"start": v(6.13, -6.59) * mm, "end": v(6.13, -6.75) * mm});
            skLineSegment(sketch, "E1430", {"start": v(6.13, -6.75) * mm, "end": v(6.13, -6.92) * mm});
            skLineSegment(sketch, "E1431", {"start": v(6.13, -6.92) * mm, "end": v(6.13, -7.08) * mm});
            skLineSegment(sketch, "E1432", {"start": v(6.13, -7.08) * mm, "end": v(6.13, -7.24) * mm});
            skLineSegment(sketch, "E1433", {"start": v(6.13, -7.24) * mm, "end": v(6.13, -7.4) * mm});
            skLineSegment(sketch, "E1434", {"start": v(6.13, -7.4) * mm, "end": v(6.13, -7.57) * mm});
            skLineSegment(sketch, "E1435", {"start": v(6.13, -7.57) * mm, "end": v(6.13, -7.74) * mm});
            skLineSegment(sketch, "E1436", {"start": v(6.13, -7.74) * mm, "end": v(6.13, -8.4) * mm});
            skLineSegment(sketch, "E1437", {"start": v(6.13, -8.4) * mm, "end": v(6.78, -8.4) * mm});
            skLineSegment(sketch, "E1438", {"start": v(6.78, -8.4) * mm, "end": v(6.95, -8.4) * mm});
            skLineSegment(sketch, "E1439", {"start": v(6.95, -8.4) * mm, "end": v(7.11, -8.4) * mm});
            skLineSegment(sketch, "E1440", {"start": v(7.11, -8.4) * mm, "end": v(7.28, -8.4) * mm});
            skLineSegment(sketch, "E1441", {"start": v(7.28, -8.4) * mm, "end": v(7.44, -8.4) * mm});
            skLineSegment(sketch, "E1442", {"start": v(7.44, -8.4) * mm, "end": v(7.6, -8.4) * mm});
            skLineSegment(sketch, "E1443", {"start": v(7.6, -8.4) * mm, "end": v(7.77, -8.4) * mm});
            skLineSegment(sketch, "E1444", {"start": v(7.77, -8.4) * mm, "end": v(7.93, -8.4) * mm});
            skLineSegment(sketch, "E1445", {"start": v(7.93, -8.4) * mm, "end": v(8.1, -8.4) * mm});
            skLineSegment(sketch, "E1446", {"start": v(8.1, -8.4) * mm, "end": v(8.26, -8.4) * mm});
            skLineSegment(sketch, "E1447", {"start": v(8.26, -8.4) * mm, "end": v(8.42, -8.4) * mm});
            skLineSegment(sketch, "E1448", {"start": v(8.42, -8.4) * mm, "end": v(8.59, -8.4) * mm});
            skLineSegment(sketch, "E1449", {"start": v(8.59, -8.4) * mm, "end": v(9.57, -8.4) * mm});
            skLineSegment(sketch, "E1450", {"start": v(9.57, -8.4) * mm, "end": v(9.57, -7.74) * mm});
            skLineSegment(sketch, "E1451", {"start": v(9.57, -7.74) * mm, "end": v(9.57, -7.57) * mm});
            skLineSegment(sketch, "E1452", {"start": v(9.57, -7.57) * mm, "end": v(9.57, -7.4) * mm});
            skLineSegment(sketch, "E1453", {"start": v(9.57, -7.4) * mm, "end": v(9.57, -7.24) * mm});
            skLineSegment(sketch, "E1454", {"start": v(9.57, -7.24) * mm, "end": v(9.57, -7.08) * mm});
            skLineSegment(sketch, "E1455", {"start": v(9.57, -7.08) * mm, "end": v(9.57, -6.92) * mm});
            skLineSegment(sketch, "E1456", {"start": v(9.57, -6.92) * mm, "end": v(9.57, -6.75) * mm});
            skLineSegment(sketch, "E1457", {"start": v(9.57, -6.75) * mm, "end": v(9.57, -6.59) * mm});
            skLineSegment(sketch, "E1458", {"start": v(9.57, -6.59) * mm, "end": v(9.57, -5.93) * mm});
            skLineSegment(sketch, "E1459", {"start": v(9.57, -5.93) * mm, "end": v(8.92, -5.93) * mm});
            skLineSegment(sketch, "E1460", {"start": v(8.92, -5.93) * mm, "end": v(8.75, -5.93) * mm});
            skLineSegment(sketch, "E1461", {"start": v(8.75, -5.93) * mm, "end": v(8.59, -5.93) * mm});
            skLineSegment(sketch, "E1462", {"start": v(8.59, -5.93) * mm, "end": v(8.42, -5.93) * mm});
            skLineSegment(sketch, "E1463", {"start": v(8.42, -5.93) * mm, "end": v(8.26, -5.93) * mm});
            skLineSegment(sketch, "E1464", {"start": v(8.26, -5.93) * mm, "end": v(8.1, -5.93) * mm});
            skLineSegment(sketch, "E1465", {"start": v(8.1, -5.93) * mm, "end": v(7.93, -5.93) * mm});
            skLineSegment(sketch, "E1466", {"start": v(7.93, -5.93) * mm, "end": v(7.77, -5.93) * mm});
            skLineSegment(sketch, "E1467", {"start": v(7.77, -5.93) * mm, "end": v(7.11, -5.77) * mm});
            skLineSegment(sketch, "E1468", {"start": v(7.11, -5.77) * mm, "end": v(6.13, -5.93) * mm});
            skLineSegment(sketch, "E1469", {"start": v(21.54, -5.77) * mm, "end": v(21.37, -5.93) * mm});
            skLineSegment(sketch, "E1470", {"start": v(21.37, -5.93) * mm, "end": v(21.37, -6.75) * mm});
            skLineSegment(sketch, "E1471", {"start": v(21.37, -6.75) * mm, "end": v(22.03, -6.75) * mm});
            skLineSegment(sketch, "E1472", {"start": v(22.03, -6.75) * mm, "end": v(22.2, -6.75) * mm});
            skLineSegment(sketch, "E1473", {"start": v(22.2, -6.75) * mm, "end": v(22.36, -6.75) * mm});
            skLineSegment(sketch, "E1474", {"start": v(22.36, -6.75) * mm, "end": v(22.52, -6.75) * mm});
            skLineSegment(sketch, "E1475", {"start": v(22.52, -6.75) * mm, "end": v(22.69, -6.75) * mm});
            skLineSegment(sketch, "E1476", {"start": v(22.69, -6.75) * mm, "end": v(22.85, -6.75) * mm});
            skLineSegment(sketch, "E1477", {"start": v(22.85, -6.75) * mm, "end": v(23.01, -6.75) * mm});
            skLineSegment(sketch, "E1478", {"start": v(23.01, -6.75) * mm, "end": v(23.18, -6.75) * mm});
            skLineSegment(sketch, "E1479", {"start": v(23.18, -6.75) * mm, "end": v(24.33, -6.59) * mm});
            skLineSegment(sketch, "E1480", {"start": v(24.33, -6.59) * mm, "end": v(24.33, -5.93) * mm});
            skLineSegment(sketch, "E1481", {"start": v(24.33, -5.93) * mm, "end": v(23.83, -5.77) * mm});
            skLineSegment(sketch, "E1482", {"start": v(23.83, -5.77) * mm, "end": v(23.18, -5.77) * mm});
            skLineSegment(sketch, "E1483", {"start": v(23.18, -5.77) * mm, "end": v(23.01, -5.77) * mm});
            skLineSegment(sketch, "E1484", {"start": v(23.01, -5.77) * mm, "end": v(22.85, -5.77) * mm});
            skLineSegment(sketch, "E1485", {"start": v(22.85, -5.77) * mm, "end": v(22.69, -5.77) * mm});
            skLineSegment(sketch, "E1486", {"start": v(22.69, -5.77) * mm, "end": v(21.54, -5.77) * mm});
            skSolve(sketch);
        }
        {
            var Q0;
            Q0 = qSketchRegion(id + "F4", true);
            extrude(context, id + "F5", {"entities" : qUnion([Q0]), "operationType" : NewBodyOperationType.ADD, "depth" : 1 * mm, "offsetDistance" : 25 * mm});
        }
    });
